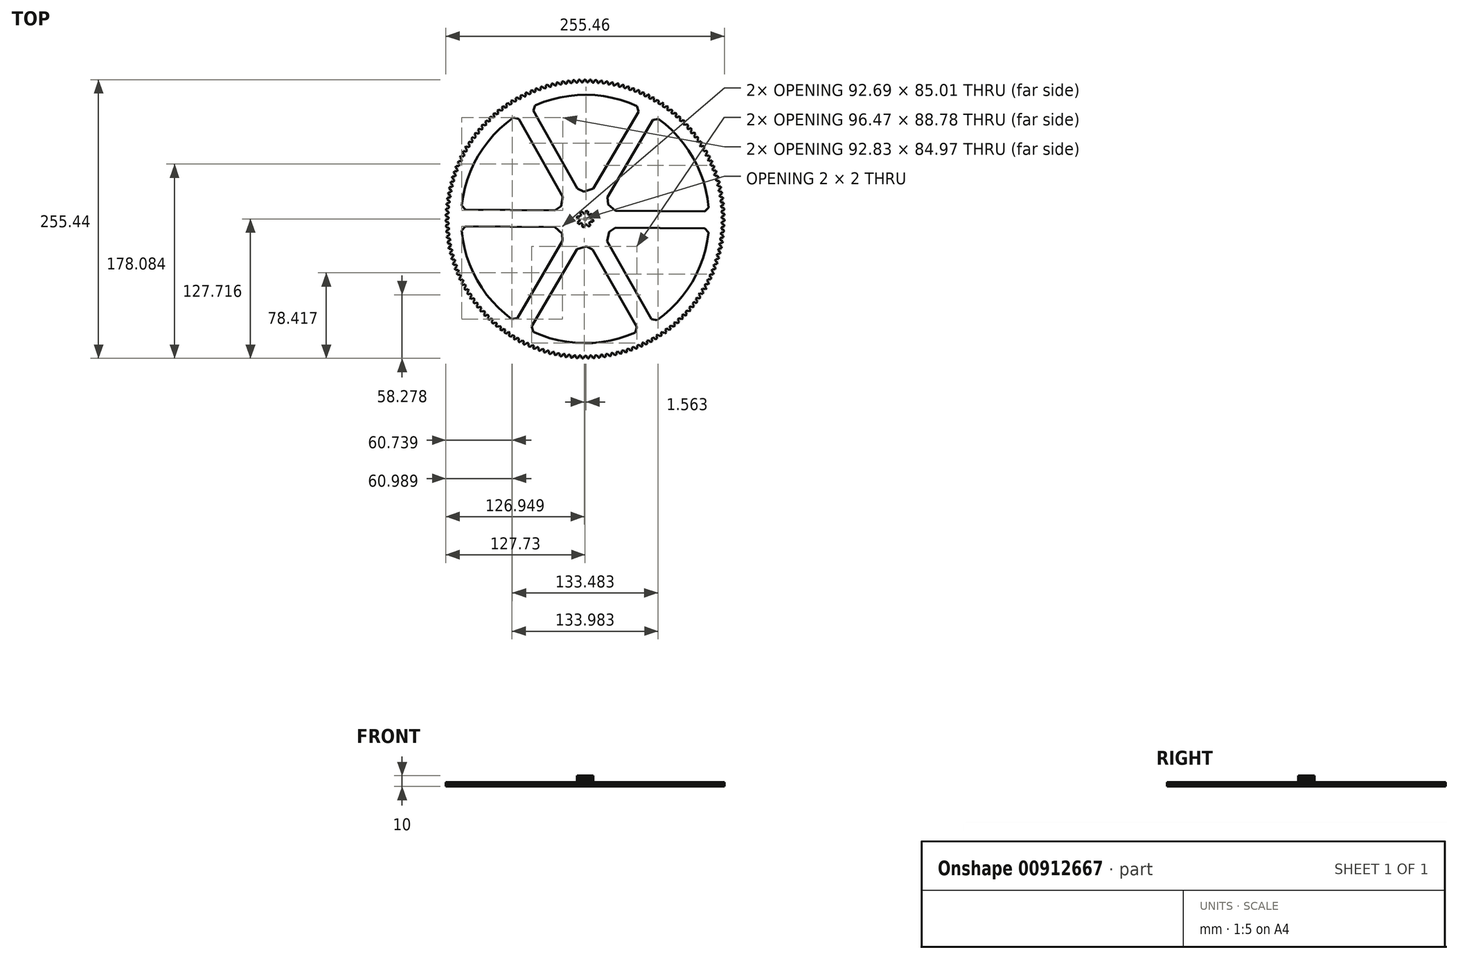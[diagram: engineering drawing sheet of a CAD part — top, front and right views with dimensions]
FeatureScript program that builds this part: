
annotation { "Feature Type Name" : "Feature", "Feature Type Description" : "" }
export const myFeature = defineFeature(function(context is Context, id is Id, definition is map)
    precondition{}
    {
        {
            var Q0;
            Q0=qCreatedBy(makeId("Top.planeOp"),FACE);
            var sketch = newSketch(context, id + "F0", { "sketchPlane" : qUnion([Q0])});
            skLineSegment(sketch, "E0", {"start": v(117.3, 0.66) * mm, "end": v(117.9, 0.46) * mm});
            skLineSegment(sketch, "E1", {"start": v(117.9, 0.46) * mm, "end": v(119.1, 0.02) * mm});
            skLineSegment(sketch, "E2", {"start": v(119.1, 0.02) * mm, "end": v(119.7, -0.2) * mm});
            skLineSegment(sketch, "E3", {"start": v(119.7, -0.2) * mm, "end": v(119.68, -1.82) * mm});
            skLineSegment(sketch, "E4", {"start": v(119.68, -1.82) * mm, "end": v(119.08, -2.04) * mm});
            skLineSegment(sketch, "E5", {"start": v(119.08, -2.04) * mm, "end": v(117.87, -2.46) * mm});
            skLineSegment(sketch, "E6", {"start": v(117.87, -2.46) * mm, "end": v(117.27, -2.65) * mm});
            skLineSegment(sketch, "E7", {"start": v(117.27, -2.65) * mm, "end": v(117.23, -4.3) * mm});
            skLineSegment(sketch, "E8", {"start": v(117.23, -4.3) * mm, "end": v(117.82, -4.52) * mm});
            skLineSegment(sketch, "E9", {"start": v(117.82, -4.52) * mm, "end": v(119, -5) * mm});
            skLineSegment(sketch, "E10", {"start": v(119, -5) * mm, "end": v(119.59, -5.25) * mm});
            skLineSegment(sketch, "E11", {"start": v(119.59, -5.25) * mm, "end": v(119.51, -6.86) * mm});
            skLineSegment(sketch, "E12", {"start": v(119.51, -6.86) * mm, "end": v(118.9, -7.06) * mm});
            skLineSegment(sketch, "E13", {"start": v(118.9, -7.06) * mm, "end": v(117.68, -7.43) * mm});
            skLineSegment(sketch, "E14", {"start": v(117.68, -7.43) * mm, "end": v(117.07, -7.6) * mm});
            skLineSegment(sketch, "E15", {"start": v(117.07, -7.6) * mm, "end": v(116.96, -9.24) * mm});
            skLineSegment(sketch, "E16", {"start": v(116.96, -9.24) * mm, "end": v(117.54, -9.49) * mm});
            skLineSegment(sketch, "E17", {"start": v(117.54, -9.49) * mm, "end": v(118.7, -10.01) * mm});
            skLineSegment(sketch, "E18", {"start": v(118.7, -10.01) * mm, "end": v(119.28, -10.3) * mm});
            skLineSegment(sketch, "E19", {"start": v(119.28, -10.3) * mm, "end": v(119.14, -11.9) * mm});
            skLineSegment(sketch, "E20", {"start": v(119.14, -11.9) * mm, "end": v(118.52, -12.07) * mm});
            skLineSegment(sketch, "E21", {"start": v(118.52, -12.07) * mm, "end": v(117.29, -12.39) * mm});
            skLineSegment(sketch, "E22", {"start": v(117.29, -12.39) * mm, "end": v(116.67, -12.53) * mm});
            skLineSegment(sketch, "E23", {"start": v(116.67, -12.53) * mm, "end": v(116.5, -14.17) * mm});
            skLineSegment(sketch, "E24", {"start": v(116.5, -14.17) * mm, "end": v(117.07, -14.44) * mm});
            skLineSegment(sketch, "E25", {"start": v(117.07, -14.44) * mm, "end": v(118.2, -15.01) * mm});
            skLineSegment(sketch, "E26", {"start": v(118.2, -15.01) * mm, "end": v(118.78, -15.31) * mm});
            skLineSegment(sketch, "E27", {"start": v(118.78, -15.31) * mm, "end": v(118.57, -16.91) * mm});
            skLineSegment(sketch, "E28", {"start": v(118.57, -16.91) * mm, "end": v(117.95, -17.06) * mm});
            skLineSegment(sketch, "E29", {"start": v(117.95, -17.06) * mm, "end": v(116.7, -17.33) * mm});
            skLineSegment(sketch, "E30", {"start": v(116.7, -17.33) * mm, "end": v(116.08, -17.45) * mm});
            skLineSegment(sketch, "E31", {"start": v(116.08, -17.45) * mm, "end": v(115.84, -19.08) * mm});
            skLineSegment(sketch, "E32", {"start": v(115.84, -19.08) * mm, "end": v(116.4, -19.37) * mm});
            skLineSegment(sketch, "E33", {"start": v(116.4, -19.37) * mm, "end": v(117.52, -19.99) * mm});
            skLineSegment(sketch, "E34", {"start": v(117.52, -19.99) * mm, "end": v(118.07, -20.31) * mm});
            skLineSegment(sketch, "E35", {"start": v(118.07, -20.31) * mm, "end": v(117.8, -21.9) * mm});
            skLineSegment(sketch, "E36", {"start": v(117.8, -21.9) * mm, "end": v(117.18, -22.02) * mm});
            skLineSegment(sketch, "E37", {"start": v(117.18, -22.02) * mm, "end": v(115.92, -22.24) * mm});
            skLineSegment(sketch, "E38", {"start": v(115.92, -22.24) * mm, "end": v(115.3, -22.34) * mm});
            skLineSegment(sketch, "E39", {"start": v(115.3, -22.34) * mm, "end": v(114.99, -23.95) * mm});
            skLineSegment(sketch, "E40", {"start": v(114.99, -23.95) * mm, "end": v(115.54, -24.27) * mm});
            skLineSegment(sketch, "E41", {"start": v(115.54, -24.27) * mm, "end": v(116.63, -24.93) * mm});
            skLineSegment(sketch, "E42", {"start": v(116.63, -24.93) * mm, "end": v(117.17, -25.28) * mm});
            skLineSegment(sketch, "E43", {"start": v(117.17, -25.28) * mm, "end": v(116.84, -26.85) * mm});
            skLineSegment(sketch, "E44", {"start": v(116.84, -26.85) * mm, "end": v(116.2, -26.95) * mm});
            skLineSegment(sketch, "E45", {"start": v(116.2, -26.95) * mm, "end": v(114.94, -27.12) * mm});
            skLineSegment(sketch, "E46", {"start": v(114.94, -27.12) * mm, "end": v(114.31, -27.2) * mm});
            skLineSegment(sketch, "E47", {"start": v(114.31, -27.2) * mm, "end": v(113.95, -28.8) * mm});
            skLineSegment(sketch, "E48", {"start": v(113.95, -28.8) * mm, "end": v(114.48, -29.13) * mm});
            skLineSegment(sketch, "E49", {"start": v(114.48, -29.13) * mm, "end": v(115.55, -29.84) * mm});
            skLineSegment(sketch, "E50", {"start": v(115.55, -29.84) * mm, "end": v(116.08, -30.2) * mm});
            skLineSegment(sketch, "E51", {"start": v(116.08, -30.2) * mm, "end": v(115.69, -31.77) * mm});
            skLineSegment(sketch, "E52", {"start": v(115.69, -31.77) * mm, "end": v(115.05, -31.84) * mm});
            skLineSegment(sketch, "E53", {"start": v(115.05, -31.84) * mm, "end": v(113.78, -31.96) * mm});
            skLineSegment(sketch, "E54", {"start": v(113.78, -31.96) * mm, "end": v(113.14, -32) * mm});
            skLineSegment(sketch, "E55", {"start": v(113.14, -32) * mm, "end": v(112.71, -33.6) * mm});
            skLineSegment(sketch, "E56", {"start": v(112.71, -33.6) * mm, "end": v(113.24, -33.95) * mm});
            skLineSegment(sketch, "E57", {"start": v(113.24, -33.95) * mm, "end": v(114.27, -34.7) * mm});
            skLineSegment(sketch, "E58", {"start": v(114.27, -34.7) * mm, "end": v(114.79, -35.08) * mm});
            skLineSegment(sketch, "E59", {"start": v(114.79, -35.08) * mm, "end": v(114.33, -36.63) * mm});
            skLineSegment(sketch, "E60", {"start": v(114.33, -36.63) * mm, "end": v(113.7, -36.68) * mm});
            skLineSegment(sketch, "E61", {"start": v(113.7, -36.68) * mm, "end": v(112.42, -36.75) * mm});
            skLineSegment(sketch, "E62", {"start": v(112.42, -36.75) * mm, "end": v(111.79, -36.77) * mm});
            skLineSegment(sketch, "E63", {"start": v(111.79, -36.77) * mm, "end": v(111.3, -38.34) * mm});
            skLineSegment(sketch, "E64", {"start": v(111.3, -38.34) * mm, "end": v(111.8, -38.71) * mm});
            skLineSegment(sketch, "E65", {"start": v(111.8, -38.71) * mm, "end": v(112.8, -39.5) * mm});
            skLineSegment(sketch, "E66", {"start": v(112.8, -39.5) * mm, "end": v(113.3, -39.9) * mm});
            skLineSegment(sketch, "E67", {"start": v(113.3, -39.9) * mm, "end": v(112.8, -41.43) * mm});
            skLineSegment(sketch, "E68", {"start": v(112.8, -41.43) * mm, "end": v(112.15, -41.46) * mm});
            skLineSegment(sketch, "E69", {"start": v(112.15, -41.46) * mm, "end": v(110.87, -41.48) * mm});
            skLineSegment(sketch, "E70", {"start": v(110.87, -41.48) * mm, "end": v(110.24, -41.47) * mm});
            skLineSegment(sketch, "E71", {"start": v(110.24, -41.47) * mm, "end": v(109.69, -43.02) * mm});
            skLineSegment(sketch, "E72", {"start": v(109.69, -43.02) * mm, "end": v(110.18, -43.42) * mm});
            skLineSegment(sketch, "E73", {"start": v(110.18, -43.42) * mm, "end": v(111.15, -44.24) * mm});
            skLineSegment(sketch, "E74", {"start": v(111.15, -44.24) * mm, "end": v(111.63, -44.67) * mm});
            skLineSegment(sketch, "E75", {"start": v(111.63, -44.67) * mm, "end": v(111.06, -46.18) * mm});
            skLineSegment(sketch, "E76", {"start": v(111.06, -46.18) * mm, "end": v(110.42, -46.17) * mm});
            skLineSegment(sketch, "E77", {"start": v(110.42, -46.17) * mm, "end": v(109.14, -46.14) * mm});
            skLineSegment(sketch, "E78", {"start": v(109.14, -46.14) * mm, "end": v(108.5, -46.11) * mm});
            skLineSegment(sketch, "E79", {"start": v(108.5, -46.11) * mm, "end": v(107.9, -47.64) * mm});
            skLineSegment(sketch, "E80", {"start": v(107.9, -47.64) * mm, "end": v(108.37, -48.05) * mm});
            skLineSegment(sketch, "E81", {"start": v(108.37, -48.05) * mm, "end": v(109.31, -48.92) * mm});
            skLineSegment(sketch, "E82", {"start": v(109.31, -48.92) * mm, "end": v(109.78, -49.36) * mm});
            skLineSegment(sketch, "E83", {"start": v(109.78, -49.36) * mm, "end": v(109.14, -50.84) * mm});
            skLineSegment(sketch, "E84", {"start": v(109.14, -50.84) * mm, "end": v(108.5, -50.82) * mm});
            skLineSegment(sketch, "E85", {"start": v(108.5, -50.82) * mm, "end": v(107.23, -50.74) * mm});
            skLineSegment(sketch, "E86", {"start": v(107.23, -50.74) * mm, "end": v(106.6, -50.68) * mm});
            skLineSegment(sketch, "E87", {"start": v(106.6, -50.68) * mm, "end": v(105.92, -52.18) * mm});
            skLineSegment(sketch, "E88", {"start": v(105.92, -52.18) * mm, "end": v(106.38, -52.62) * mm});
            skLineSegment(sketch, "E89", {"start": v(106.38, -52.62) * mm, "end": v(107.29, -53.52) * mm});
            skLineSegment(sketch, "E90", {"start": v(107.29, -53.52) * mm, "end": v(107.73, -53.98) * mm});
            skLineSegment(sketch, "E91", {"start": v(107.73, -53.98) * mm, "end": v(107.04, -55.43) * mm});
            skLineSegment(sketch, "E92", {"start": v(107.04, -55.43) * mm, "end": v(106.4, -55.38) * mm});
            skLineSegment(sketch, "E93", {"start": v(106.4, -55.38) * mm, "end": v(105.13, -55.25) * mm});
            skLineSegment(sketch, "E94", {"start": v(105.13, -55.25) * mm, "end": v(104.5, -55.17) * mm});
            skLineSegment(sketch, "E95", {"start": v(104.5, -55.17) * mm, "end": v(103.77, -56.64) * mm});
            skLineSegment(sketch, "E96", {"start": v(103.77, -56.64) * mm, "end": v(104.21, -57.1) * mm});
            skLineSegment(sketch, "E97", {"start": v(104.21, -57.1) * mm, "end": v(105.08, -58.03) * mm});
            skLineSegment(sketch, "E98", {"start": v(105.08, -58.03) * mm, "end": v(105.51, -58.5) * mm});
            skLineSegment(sketch, "E99", {"start": v(105.51, -58.5) * mm, "end": v(104.76, -59.94) * mm});
            skLineSegment(sketch, "E100", {"start": v(104.76, -59.94) * mm, "end": v(104.13, -59.86) * mm});
            skLineSegment(sketch, "E101", {"start": v(104.13, -59.86) * mm, "end": v(102.86, -59.68) * mm});
            skLineSegment(sketch, "E102", {"start": v(102.86, -59.68) * mm, "end": v(102.24, -59.57) * mm});
            skLineSegment(sketch, "E103", {"start": v(102.24, -59.57) * mm, "end": v(101.45, -61.01) * mm});
            skLineSegment(sketch, "E104", {"start": v(101.45, -61.01) * mm, "end": v(101.87, -61.48) * mm});
            skLineSegment(sketch, "E105", {"start": v(101.87, -61.48) * mm, "end": v(102.7, -62.45) * mm});
            skLineSegment(sketch, "E106", {"start": v(102.7, -62.45) * mm, "end": v(103.11, -62.95) * mm});
            skLineSegment(sketch, "E107", {"start": v(103.11, -62.95) * mm, "end": v(102.3, -64.35) * mm});
            skLineSegment(sketch, "E108", {"start": v(102.3, -64.35) * mm, "end": v(101.67, -64.24) * mm});
            skLineSegment(sketch, "E109", {"start": v(101.67, -64.24) * mm, "end": v(100.42, -64.01) * mm});
            skLineSegment(sketch, "E110", {"start": v(100.42, -64.01) * mm, "end": v(99.8, -63.88) * mm});
            skLineSegment(sketch, "E111", {"start": v(99.8, -63.88) * mm, "end": v(98.95, -65.3) * mm});
            skLineSegment(sketch, "E112", {"start": v(98.95, -65.3) * mm, "end": v(99.36, -65.78) * mm});
            skLineSegment(sketch, "E113", {"start": v(99.36, -65.78) * mm, "end": v(100.15, -66.78) * mm});
            skLineSegment(sketch, "E114", {"start": v(100.15, -66.78) * mm, "end": v(100.54, -67.3) * mm});
            skLineSegment(sketch, "E115", {"start": v(100.54, -67.3) * mm, "end": v(99.68, -68.66) * mm});
            skLineSegment(sketch, "E116", {"start": v(99.68, -68.66) * mm, "end": v(99.05, -68.53) * mm});
            skLineSegment(sketch, "E117", {"start": v(99.05, -68.53) * mm, "end": v(97.8, -68.25) * mm});
            skLineSegment(sketch, "E118", {"start": v(97.8, -68.25) * mm, "end": v(97.19, -68.1) * mm});
            skLineSegment(sketch, "E119", {"start": v(97.19, -68.1) * mm, "end": v(96.29, -69.47) * mm});
            skLineSegment(sketch, "E120", {"start": v(96.29, -69.47) * mm, "end": v(96.67, -69.97) * mm});
            skLineSegment(sketch, "E121", {"start": v(96.67, -69.97) * mm, "end": v(97.43, -71) * mm});
            skLineSegment(sketch, "E122", {"start": v(97.43, -71) * mm, "end": v(97.8, -71.53) * mm});
            skLineSegment(sketch, "E123", {"start": v(97.8, -71.53) * mm, "end": v(96.88, -72.86) * mm});
            skLineSegment(sketch, "E124", {"start": v(96.88, -72.86) * mm, "end": v(96.26, -72.7) * mm});
            skLineSegment(sketch, "E125", {"start": v(96.26, -72.7) * mm, "end": v(95.03, -72.37) * mm});
            skLineSegment(sketch, "E126", {"start": v(95.03, -72.37) * mm, "end": v(94.42, -72.2) * mm});
            skLineSegment(sketch, "E127", {"start": v(94.42, -72.2) * mm, "end": v(93.46, -73.53) * mm});
            skLineSegment(sketch, "E128", {"start": v(93.46, -73.53) * mm, "end": v(93.83, -74.05) * mm});
            skLineSegment(sketch, "E129", {"start": v(93.83, -74.05) * mm, "end": v(94.54, -75.11) * mm});
            skLineSegment(sketch, "E130", {"start": v(94.54, -75.11) * mm, "end": v(94.89, -75.65) * mm});
            skLineSegment(sketch, "E131", {"start": v(94.89, -75.65) * mm, "end": v(93.92, -76.94) * mm});
            skLineSegment(sketch, "E132", {"start": v(93.92, -76.94) * mm, "end": v(93.3, -76.77) * mm});
            skLineSegment(sketch, "E133", {"start": v(93.3, -76.77) * mm, "end": v(92.09, -76.39) * mm});
            skLineSegment(sketch, "E134", {"start": v(92.09, -76.39) * mm, "end": v(91.49, -76.19) * mm});
            skLineSegment(sketch, "E135", {"start": v(91.49, -76.19) * mm, "end": v(90.48, -77.49) * mm});
            skLineSegment(sketch, "E136", {"start": v(90.48, -77.49) * mm, "end": v(90.82, -78.02) * mm});
            skLineSegment(sketch, "E137", {"start": v(90.82, -78.02) * mm, "end": v(91.5, -79.1) * mm});
            skLineSegment(sketch, "E138", {"start": v(91.5, -79.1) * mm, "end": v(91.82, -79.66) * mm});
            skLineSegment(sketch, "E139", {"start": v(91.82, -79.66) * mm, "end": v(90.8, -80.91) * mm});
            skLineSegment(sketch, "E140", {"start": v(90.8, -80.91) * mm, "end": v(90.2, -80.71) * mm});
            skLineSegment(sketch, "E141", {"start": v(90.2, -80.71) * mm, "end": v(89, -80.28) * mm});
            skLineSegment(sketch, "E142", {"start": v(89, -80.28) * mm, "end": v(88.4, -80.06) * mm});
            skLineSegment(sketch, "E143", {"start": v(88.4, -80.06) * mm, "end": v(87.34, -81.32) * mm});
            skLineSegment(sketch, "E144", {"start": v(87.34, -81.32) * mm, "end": v(87.66, -81.86) * mm});
            skLineSegment(sketch, "E145", {"start": v(87.66, -81.86) * mm, "end": v(88.29, -82.97) * mm});
            skLineSegment(sketch, "E146", {"start": v(88.29, -82.97) * mm, "end": v(88.6, -83.54) * mm});
            skLineSegment(sketch, "E147", {"start": v(88.6, -83.54) * mm, "end": v(87.53, -84.75) * mm});
            skLineSegment(sketch, "E148", {"start": v(87.53, -84.75) * mm, "end": v(86.93, -84.53) * mm});
            skLineSegment(sketch, "E149", {"start": v(86.93, -84.53) * mm, "end": v(85.74, -84.05) * mm});
            skLineSegment(sketch, "E150", {"start": v(85.74, -84.05) * mm, "end": v(85.16, -83.8) * mm});
            skLineSegment(sketch, "E151", {"start": v(85.16, -83.8) * mm, "end": v(84.05, -85.02) * mm});
            skLineSegment(sketch, "E152", {"start": v(84.05, -85.02) * mm, "end": v(84.35, -85.58) * mm});
            skLineSegment(sketch, "E153", {"start": v(84.35, -85.58) * mm, "end": v(84.94, -86.71) * mm});
            skLineSegment(sketch, "E154", {"start": v(84.94, -86.71) * mm, "end": v(85.22, -87.3) * mm});
            skLineSegment(sketch, "E155", {"start": v(85.22, -87.3) * mm, "end": v(84.1, -88.46) * mm});
            skLineSegment(sketch, "E156", {"start": v(84.1, -88.46) * mm, "end": v(83.52, -88.21) * mm});
            skLineSegment(sketch, "E157", {"start": v(83.52, -88.21) * mm, "end": v(82.35, -87.7) * mm});
            skLineSegment(sketch, "E158", {"start": v(82.35, -87.7) * mm, "end": v(81.78, -87.42) * mm});
            skLineSegment(sketch, "E159", {"start": v(81.78, -87.42) * mm, "end": v(80.62, -88.6) * mm});
            skLineSegment(sketch, "E160", {"start": v(80.62, -88.6) * mm, "end": v(80.9, -89.16) * mm});
            skLineSegment(sketch, "E161", {"start": v(80.9, -89.16) * mm, "end": v(81.44, -90.32) * mm});
            skLineSegment(sketch, "E162", {"start": v(81.44, -90.32) * mm, "end": v(81.7, -90.9) * mm});
            skLineSegment(sketch, "E163", {"start": v(81.7, -90.9) * mm, "end": v(80.54, -92.03) * mm});
            skLineSegment(sketch, "E164", {"start": v(80.54, -92.03) * mm, "end": v(79.96, -91.76) * mm});
            skLineSegment(sketch, "E165", {"start": v(79.96, -91.76) * mm, "end": v(78.81, -91.2) * mm});
            skLineSegment(sketch, "E166", {"start": v(78.81, -91.2) * mm, "end": v(78.25, -90.9) * mm});
            skLineSegment(sketch, "E167", {"start": v(78.25, -90.9) * mm, "end": v(77.05, -92.03) * mm});
            skLineSegment(sketch, "E168", {"start": v(77.05, -92.03) * mm, "end": v(77.31, -92.6) * mm});
            skLineSegment(sketch, "E169", {"start": v(77.31, -92.6) * mm, "end": v(77.8, -93.78) * mm});
            skLineSegment(sketch, "E170", {"start": v(77.8, -93.78) * mm, "end": v(78.03, -94.38) * mm});
            skLineSegment(sketch, "E171", {"start": v(78.03, -94.38) * mm, "end": v(76.84, -95.46) * mm});
            skLineSegment(sketch, "E172", {"start": v(76.84, -95.46) * mm, "end": v(76.27, -95.17) * mm});
            skLineSegment(sketch, "E173", {"start": v(76.27, -95.17) * mm, "end": v(75.14, -94.56) * mm});
            skLineSegment(sketch, "E174", {"start": v(75.14, -94.56) * mm, "end": v(74.6, -94.24) * mm});
            skLineSegment(sketch, "E175", {"start": v(74.6, -94.24) * mm, "end": v(73.35, -95.32) * mm});
            skLineSegment(sketch, "E176", {"start": v(73.35, -95.32) * mm, "end": v(73.59, -95.9) * mm});
            skLineSegment(sketch, "E177", {"start": v(73.59, -95.9) * mm, "end": v(74.03, -97.1) * mm});
            skLineSegment(sketch, "E178", {"start": v(74.03, -97.1) * mm, "end": v(74.24, -97.7) * mm});
            skLineSegment(sketch, "E179", {"start": v(74.24, -97.7) * mm, "end": v(73, -98.74) * mm});
            skLineSegment(sketch, "E180", {"start": v(73, -98.74) * mm, "end": v(72.44, -98.42) * mm});
            skLineSegment(sketch, "E181", {"start": v(72.44, -98.42) * mm, "end": v(71.34, -97.77) * mm});
            skLineSegment(sketch, "E182", {"start": v(71.34, -97.77) * mm, "end": v(70.8, -97.43) * mm});
            skLineSegment(sketch, "E183", {"start": v(70.8, -97.43) * mm, "end": v(69.52, -98.46) * mm});
            skLineSegment(sketch, "E184", {"start": v(69.52, -98.46) * mm, "end": v(69.73, -99.05) * mm});
            skLineSegment(sketch, "E185", {"start": v(69.73, -99.05) * mm, "end": v(70.13, -100.27) * mm});
            skLineSegment(sketch, "E186", {"start": v(70.13, -100.27) * mm, "end": v(70.31, -100.88) * mm});
            skLineSegment(sketch, "E187", {"start": v(70.31, -100.88) * mm, "end": v(69.03, -101.86) * mm});
            skLineSegment(sketch, "E188", {"start": v(69.03, -101.86) * mm, "end": v(68.49, -101.52) * mm});
            skLineSegment(sketch, "E189", {"start": v(68.49, -101.52) * mm, "end": v(67.42, -100.83) * mm});
            skLineSegment(sketch, "E190", {"start": v(67.42, -100.83) * mm, "end": v(66.9, -100.47) * mm});
            skLineSegment(sketch, "E191", {"start": v(66.9, -100.47) * mm, "end": v(65.57, -101.44) * mm});
            skLineSegment(sketch, "E192", {"start": v(65.57, -101.44) * mm, "end": v(65.76, -102.05) * mm});
            skLineSegment(sketch, "E193", {"start": v(65.76, -102.05) * mm, "end": v(66.1, -103.28) * mm});
            skLineSegment(sketch, "E194", {"start": v(66.1, -103.28) * mm, "end": v(66.27, -103.9) * mm});
            skLineSegment(sketch, "E195", {"start": v(66.27, -103.9) * mm, "end": v(64.95, -104.83) * mm});
            skLineSegment(sketch, "E196", {"start": v(64.95, -104.83) * mm, "end": v(64.42, -104.47) * mm});
            skLineSegment(sketch, "E197", {"start": v(64.42, -104.47) * mm, "end": v(63.38, -103.73) * mm});
            skLineSegment(sketch, "E198", {"start": v(63.38, -103.73) * mm, "end": v(62.87, -103.35) * mm});
            skLineSegment(sketch, "E199", {"start": v(62.87, -103.35) * mm, "end": v(61.5, -104.27) * mm});
            skLineSegment(sketch, "E200", {"start": v(61.5, -104.27) * mm, "end": v(61.67, -104.88) * mm});
            skLineSegment(sketch, "E201", {"start": v(61.67, -104.88) * mm, "end": v(61.97, -106.13) * mm});
            skLineSegment(sketch, "E202", {"start": v(61.97, -106.13) * mm, "end": v(62.1, -106.75) * mm});
            skLineSegment(sketch, "E203", {"start": v(62.1, -106.75) * mm, "end": v(60.75, -107.63) * mm});
            skLineSegment(sketch, "E204", {"start": v(60.75, -107.63) * mm, "end": v(60.23, -107.25) * mm});
            skLineSegment(sketch, "E205", {"start": v(60.23, -107.25) * mm, "end": v(59.22, -106.47) * mm});
            skLineSegment(sketch, "E206", {"start": v(59.22, -106.47) * mm, "end": v(58.73, -106.07) * mm});
            skLineSegment(sketch, "E207", {"start": v(58.73, -106.07) * mm, "end": v(57.33, -106.94) * mm});
            skLineSegment(sketch, "E208", {"start": v(57.33, -106.94) * mm, "end": v(57.47, -107.56) * mm});
            skLineSegment(sketch, "E209", {"start": v(57.47, -107.56) * mm, "end": v(57.72, -108.8) * mm});
            skLineSegment(sketch, "E210", {"start": v(57.72, -108.8) * mm, "end": v(57.83, -109.44) * mm});
            skLineSegment(sketch, "E211", {"start": v(57.83, -109.44) * mm, "end": v(56.45, -110.26) * mm});
            skLineSegment(sketch, "E212", {"start": v(56.45, -110.26) * mm, "end": v(55.94, -109.86) * mm});
            skLineSegment(sketch, "E213", {"start": v(55.94, -109.86) * mm, "end": v(54.97, -109.04) * mm});
            skLineSegment(sketch, "E214", {"start": v(54.97, -109.04) * mm, "end": v(54.49, -108.63) * mm});
            skLineSegment(sketch, "E215", {"start": v(54.49, -108.63) * mm, "end": v(53.06, -109.44) * mm});
            skLineSegment(sketch, "E216", {"start": v(53.06, -109.44) * mm, "end": v(53.17, -110.06) * mm});
            skLineSegment(sketch, "E217", {"start": v(53.17, -110.06) * mm, "end": v(53.37, -111.32) * mm});
            skLineSegment(sketch, "E218", {"start": v(53.37, -111.32) * mm, "end": v(53.46, -111.96) * mm});
            skLineSegment(sketch, "E219", {"start": v(53.46, -111.96) * mm, "end": v(52.04, -112.72) * mm});
            skLineSegment(sketch, "E220", {"start": v(52.04, -112.72) * mm, "end": v(51.55, -112.3) * mm});
            skLineSegment(sketch, "E221", {"start": v(51.55, -112.3) * mm, "end": v(50.6, -111.45) * mm});
            skLineSegment(sketch, "E222", {"start": v(50.6, -111.45) * mm, "end": v(50.15, -111.01) * mm});
            skLineSegment(sketch, "E223", {"start": v(50.15, -111.01) * mm, "end": v(48.69, -111.76) * mm});
            skLineSegment(sketch, "E224", {"start": v(48.69, -111.76) * mm, "end": v(48.78, -112.4) * mm});
            skLineSegment(sketch, "E225", {"start": v(48.78, -112.4) * mm, "end": v(48.93, -113.66) * mm});
            skLineSegment(sketch, "E226", {"start": v(48.93, -113.66) * mm, "end": v(48.99, -114.3) * mm});
            skLineSegment(sketch, "E227", {"start": v(48.99, -114.3) * mm, "end": v(47.54, -115) * mm});
            skLineSegment(sketch, "E228", {"start": v(47.54, -115) * mm, "end": v(47.07, -114.57) * mm});
            skLineSegment(sketch, "E229", {"start": v(47.07, -114.57) * mm, "end": v(46.16, -113.68) * mm});
            skLineSegment(sketch, "E230", {"start": v(46.16, -113.68) * mm, "end": v(45.72, -113.22) * mm});
            skLineSegment(sketch, "E231", {"start": v(45.72, -113.22) * mm, "end": v(44.23, -113.92) * mm});
            skLineSegment(sketch, "E232", {"start": v(44.23, -113.92) * mm, "end": v(44.3, -114.55) * mm});
            skLineSegment(sketch, "E233", {"start": v(44.3, -114.55) * mm, "end": v(44.4, -115.82) * mm});
            skLineSegment(sketch, "E234", {"start": v(44.4, -115.82) * mm, "end": v(44.43, -116.46) * mm});
            skLineSegment(sketch, "E235", {"start": v(44.43, -116.46) * mm, "end": v(42.95, -117.12) * mm});
            skLineSegment(sketch, "E236", {"start": v(42.95, -117.12) * mm, "end": v(42.5, -116.66) * mm});
            skLineSegment(sketch, "E237", {"start": v(42.5, -116.66) * mm, "end": v(41.63, -115.73) * mm});
            skLineSegment(sketch, "E238", {"start": v(41.63, -115.73) * mm, "end": v(41.2, -115.26) * mm});
            skLineSegment(sketch, "E239", {"start": v(41.2, -115.26) * mm, "end": v(39.69, -115.9) * mm});
            skLineSegment(sketch, "E240", {"start": v(39.69, -115.9) * mm, "end": v(39.73, -116.53) * mm});
            skLineSegment(sketch, "E241", {"start": v(39.73, -116.53) * mm, "end": v(39.77, -117.8) * mm});
            skLineSegment(sketch, "E242", {"start": v(39.77, -117.8) * mm, "end": v(39.79, -118.44) * mm});
            skLineSegment(sketch, "E243", {"start": v(39.79, -118.44) * mm, "end": v(38.29, -119.04) * mm});
            skLineSegment(sketch, "E244", {"start": v(38.29, -119.04) * mm, "end": v(37.85, -118.56) * mm});
            skLineSegment(sketch, "E245", {"start": v(37.85, -118.56) * mm, "end": v(37.02, -117.6) * mm});
            skLineSegment(sketch, "E246", {"start": v(37.02, -117.6) * mm, "end": v(36.61, -117.11) * mm});
            skLineSegment(sketch, "E247", {"start": v(36.61, -117.11) * mm, "end": v(35.07, -117.69) * mm});
            skLineSegment(sketch, "E248", {"start": v(35.07, -117.69) * mm, "end": v(35.08, -118.32) * mm});
            skLineSegment(sketch, "E249", {"start": v(35.08, -118.32) * mm, "end": v(35.08, -119.6) * mm});
            skLineSegment(sketch, "E250", {"start": v(35.08, -119.6) * mm, "end": v(35.07, -120.24) * mm});
            skLineSegment(sketch, "E251", {"start": v(35.07, -120.24) * mm, "end": v(33.55, -120.77) * mm});
            skLineSegment(sketch, "E252", {"start": v(33.55, -120.77) * mm, "end": v(33.13, -120.28) * mm});
            skLineSegment(sketch, "E253", {"start": v(33.13, -120.28) * mm, "end": v(32.33, -119.29) * mm});
            skLineSegment(sketch, "E254", {"start": v(32.33, -119.29) * mm, "end": v(31.95, -118.78) * mm});
            skLineSegment(sketch, "E255", {"start": v(31.95, -118.78) * mm, "end": v(30.39, -119.3) * mm});
            skLineSegment(sketch, "E256", {"start": v(30.39, -119.3) * mm, "end": v(30.38, -119.93) * mm});
            skLineSegment(sketch, "E257", {"start": v(30.38, -119.93) * mm, "end": v(30.32, -121.2) * mm});
            skLineSegment(sketch, "E258", {"start": v(30.32, -121.2) * mm, "end": v(30.28, -121.85) * mm});
            skLineSegment(sketch, "E259", {"start": v(30.28, -121.85) * mm, "end": v(28.74, -122.32) * mm});
            skLineSegment(sketch, "E260", {"start": v(28.74, -122.32) * mm, "end": v(28.35, -121.81) * mm});
            skLineSegment(sketch, "E261", {"start": v(28.35, -121.81) * mm, "end": v(27.6, -120.79) * mm});
            skLineSegment(sketch, "E262", {"start": v(27.6, -120.79) * mm, "end": v(27.23, -120.27) * mm});
            skLineSegment(sketch, "E263", {"start": v(27.23, -120.27) * mm, "end": v(25.65, -120.72) * mm});
            skLineSegment(sketch, "E264", {"start": v(25.65, -120.72) * mm, "end": v(25.6, -121.36) * mm});
            skLineSegment(sketch, "E265", {"start": v(25.6, -121.36) * mm, "end": v(25.5, -122.63) * mm});
            skLineSegment(sketch, "E266", {"start": v(25.5, -122.63) * mm, "end": v(25.44, -123.27) * mm});
            skLineSegment(sketch, "E267", {"start": v(25.44, -123.27) * mm, "end": v(23.88, -123.68) * mm});
            skLineSegment(sketch, "E268", {"start": v(23.88, -123.68) * mm, "end": v(23.5, -123.16) * mm});
            skLineSegment(sketch, "E269", {"start": v(23.5, -123.16) * mm, "end": v(22.8, -122.1) * mm});
            skLineSegment(sketch, "E270", {"start": v(22.8, -122.1) * mm, "end": v(22.45, -121.57) * mm});
            skLineSegment(sketch, "E271", {"start": v(22.45, -121.57) * mm, "end": v(20.85, -121.96) * mm});
            skLineSegment(sketch, "E272", {"start": v(20.85, -121.96) * mm, "end": v(20.79, -122.6) * mm});
            skLineSegment(sketch, "E273", {"start": v(20.79, -122.6) * mm, "end": v(20.64, -123.86) * mm});
            skLineSegment(sketch, "E274", {"start": v(20.64, -123.86) * mm, "end": v(20.55, -124.5) * mm});
            skLineSegment(sketch, "E275", {"start": v(20.55, -124.5) * mm, "end": v(18.97, -124.84) * mm});
            skLineSegment(sketch, "E276", {"start": v(18.97, -124.84) * mm, "end": v(18.62, -124.3) * mm});
            skLineSegment(sketch, "E277", {"start": v(18.62, -124.3) * mm, "end": v(17.94, -123.22) * mm});
            skLineSegment(sketch, "E278", {"start": v(17.94, -123.22) * mm, "end": v(17.62, -122.68) * mm});
            skLineSegment(sketch, "E279", {"start": v(17.62, -122.68) * mm, "end": v(16, -123) * mm});
            skLineSegment(sketch, "E280", {"start": v(16, -123) * mm, "end": v(15.92, -123.63) * mm});
            skLineSegment(sketch, "E281", {"start": v(15.92, -123.63) * mm, "end": v(15.72, -124.9) * mm});
            skLineSegment(sketch, "E282", {"start": v(15.72, -124.9) * mm, "end": v(15.6, -125.53) * mm});
            skLineSegment(sketch, "E283", {"start": v(15.6, -125.53) * mm, "end": v(14.02, -125.81) * mm});
            skLineSegment(sketch, "E284", {"start": v(14.02, -125.81) * mm, "end": v(13.69, -125.26) * mm});
            skLineSegment(sketch, "E285", {"start": v(13.69, -125.26) * mm, "end": v(13.06, -124.15) * mm});
            skLineSegment(sketch, "E286", {"start": v(13.06, -124.15) * mm, "end": v(12.75, -123.6) * mm});
            skLineSegment(sketch, "E287", {"start": v(12.75, -123.6) * mm, "end": v(11.13, -123.86) * mm});
            skLineSegment(sketch, "E288", {"start": v(11.13, -123.86) * mm, "end": v(11.02, -124.48) * mm});
            skLineSegment(sketch, "E289", {"start": v(11.02, -124.48) * mm, "end": v(10.77, -125.73) * mm});
            skLineSegment(sketch, "E290", {"start": v(10.77, -125.73) * mm, "end": v(10.63, -126.36) * mm});
            skLineSegment(sketch, "E291", {"start": v(10.63, -126.36) * mm, "end": v(9.03, -126.59) * mm});
            skLineSegment(sketch, "E292", {"start": v(9.03, -126.59) * mm, "end": v(8.72, -126.02) * mm});
            skLineSegment(sketch, "E293", {"start": v(8.72, -126.02) * mm, "end": v(8.13, -124.9) * mm});
            skLineSegment(sketch, "E294", {"start": v(8.13, -124.9) * mm, "end": v(7.85, -124.32) * mm});
            skLineSegment(sketch, "E295", {"start": v(7.85, -124.32) * mm, "end": v(6.22, -124.52) * mm});
            skLineSegment(sketch, "E296", {"start": v(6.22, -124.52) * mm, "end": v(6.09, -125.14) * mm});
            skLineSegment(sketch, "E297", {"start": v(6.09, -125.14) * mm, "end": v(5.79, -126.38) * mm});
            skLineSegment(sketch, "E298", {"start": v(5.79, -126.38) * mm, "end": v(5.62, -127) * mm});
            skLineSegment(sketch, "E299", {"start": v(5.62, -127) * mm, "end": v(4.02, -127.16) * mm});
            skLineSegment(sketch, "E300", {"start": v(4.02, -127.16) * mm, "end": v(3.73, -126.59) * mm});
            skLineSegment(sketch, "E301", {"start": v(3.73, -126.59) * mm, "end": v(3.19, -125.43) * mm});
            skLineSegment(sketch, "E302", {"start": v(3.19, -125.43) * mm, "end": v(2.93, -124.85) * mm});
            skLineSegment(sketch, "E303", {"start": v(2.93, -124.85) * mm, "end": v(1.3, -124.99) * mm});
            skLineSegment(sketch, "E304", {"start": v(1.3, -124.99) * mm, "end": v(1.13, -125.6) * mm});
            skLineSegment(sketch, "E305", {"start": v(1.13, -125.6) * mm, "end": v(0.78, -126.83) * mm});
            skLineSegment(sketch, "E306", {"start": v(0.78, -126.83) * mm, "end": v(0.6, -127.44) * mm});
            skLineSegment(sketch, "E307", {"start": v(0.6, -127.44) * mm, "end": v(-1.02, -127.54) * mm});
            skLineSegment(sketch, "E308", {"start": v(-1.02, -127.54) * mm, "end": v(-1.28, -126.95) * mm});
            skLineSegment(sketch, "E309", {"start": v(-1.28, -126.95) * mm, "end": v(-1.78, -125.78) * mm});
            skLineSegment(sketch, "E310", {"start": v(-1.78, -125.78) * mm, "end": v(-2.01, -125.19) * mm});
            skLineSegment(sketch, "E311", {"start": v(-2.01, -125.19) * mm, "end": v(-3.65, -125.26) * mm});
            skLineSegment(sketch, "E312", {"start": v(-3.65, -125.26) * mm, "end": v(-3.84, -125.86) * mm});
            skLineSegment(sketch, "E313", {"start": v(-3.84, -125.86) * mm, "end": v(-4.23, -127.07) * mm});
            skLineSegment(sketch, "E314", {"start": v(-4.23, -127.07) * mm, "end": v(-4.45, -127.68) * mm});
            skLineSegment(sketch, "E315", {"start": v(-4.45, -127.68) * mm, "end": v(-6.06, -127.72) * mm});
            skLineSegment(sketch, "E316", {"start": v(-6.06, -127.72) * mm, "end": v(-6.3, -127.12) * mm});
            skLineSegment(sketch, "E317", {"start": v(-6.3, -127.12) * mm, "end": v(-6.75, -125.93) * mm});
            skLineSegment(sketch, "E318", {"start": v(-6.75, -125.93) * mm, "end": v(-6.96, -125.33) * mm});
            skLineSegment(sketch, "E319", {"start": v(-6.96, -125.33) * mm, "end": v(-8.6, -125.33) * mm});
            skLineSegment(sketch, "E320", {"start": v(-8.6, -125.33) * mm, "end": v(-8.81, -125.93) * mm});
            skLineSegment(sketch, "E321", {"start": v(-8.81, -125.93) * mm, "end": v(-9.26, -127.13) * mm});
            skLineSegment(sketch, "E322", {"start": v(-9.26, -127.13) * mm, "end": v(-9.5, -127.72) * mm});
            skLineSegment(sketch, "E323", {"start": v(-9.5, -127.72) * mm, "end": v(-11.1, -127.7) * mm});
            skLineSegment(sketch, "E324", {"start": v(-11.1, -127.7) * mm, "end": v(-11.32, -127.09) * mm});
            skLineSegment(sketch, "E325", {"start": v(-11.32, -127.09) * mm, "end": v(-11.73, -125.88) * mm});
            skLineSegment(sketch, "E326", {"start": v(-11.73, -125.88) * mm, "end": v(-11.91, -125.27) * mm});
            skLineSegment(sketch, "E327", {"start": v(-11.91, -125.27) * mm, "end": v(-13.55, -125.21) * mm});
            skLineSegment(sketch, "E328", {"start": v(-13.55, -125.21) * mm, "end": v(-13.79, -125.8) * mm});
            skLineSegment(sketch, "E329", {"start": v(-13.79, -125.8) * mm, "end": v(-14.28, -126.98) * mm});
            skLineSegment(sketch, "E330", {"start": v(-14.28, -126.98) * mm, "end": v(-14.54, -127.57) * mm});
            skLineSegment(sketch, "E331", {"start": v(-14.54, -127.57) * mm, "end": v(-16.15, -127.47) * mm});
            skLineSegment(sketch, "E332", {"start": v(-16.15, -127.47) * mm, "end": v(-16.34, -126.86) * mm});
            skLineSegment(sketch, "E333", {"start": v(-16.34, -126.86) * mm, "end": v(-16.7, -125.63) * mm});
            skLineSegment(sketch, "E334", {"start": v(-16.7, -125.63) * mm, "end": v(-16.86, -125.02) * mm});
            skLineSegment(sketch, "E335", {"start": v(-16.86, -125.02) * mm, "end": v(-18.5, -124.9) * mm});
            skLineSegment(sketch, "E336", {"start": v(-18.5, -124.9) * mm, "end": v(-18.75, -125.47) * mm});
            skLineSegment(sketch, "E337", {"start": v(-18.75, -125.47) * mm, "end": v(-19.3, -126.63) * mm});
            skLineSegment(sketch, "E338", {"start": v(-19.3, -126.63) * mm, "end": v(-19.57, -127.2) * mm});
            skLineSegment(sketch, "E339", {"start": v(-19.57, -127.2) * mm, "end": v(-21.18, -127.05) * mm});
            skLineSegment(sketch, "E340", {"start": v(-21.18, -127.05) * mm, "end": v(-21.35, -126.43) * mm});
            skLineSegment(sketch, "E341", {"start": v(-21.35, -126.43) * mm, "end": v(-21.65, -125.2) * mm});
            skLineSegment(sketch, "E342", {"start": v(-21.65, -125.2) * mm, "end": v(-21.8, -124.57) * mm});
            skLineSegment(sketch, "E343", {"start": v(-21.8, -124.57) * mm, "end": v(-23.42, -124.38) * mm});
            skLineSegment(sketch, "E344", {"start": v(-23.42, -124.38) * mm, "end": v(-23.7, -124.95) * mm});
            skLineSegment(sketch, "E345", {"start": v(-23.7, -124.95) * mm, "end": v(-24.28, -126.09) * mm});
            skLineSegment(sketch, "E346", {"start": v(-24.28, -126.09) * mm, "end": v(-24.6, -126.65) * mm});
            skLineSegment(sketch, "E347", {"start": v(-24.6, -126.65) * mm, "end": v(-26.19, -126.43) * mm});
            skLineSegment(sketch, "E348", {"start": v(-26.19, -126.43) * mm, "end": v(-26.33, -125.8) * mm});
            skLineSegment(sketch, "E349", {"start": v(-26.33, -125.8) * mm, "end": v(-26.59, -124.56) * mm});
            skLineSegment(sketch, "E350", {"start": v(-26.59, -124.56) * mm, "end": v(-26.7, -123.93) * mm});
            skLineSegment(sketch, "E351", {"start": v(-26.7, -123.93) * mm, "end": v(-28.32, -123.68) * mm});
            skLineSegment(sketch, "E352", {"start": v(-28.32, -123.68) * mm, "end": v(-28.62, -124.24) * mm});
            skLineSegment(sketch, "E353", {"start": v(-28.62, -124.24) * mm, "end": v(-29.25, -125.35) * mm});
            skLineSegment(sketch, "E354", {"start": v(-29.25, -125.35) * mm, "end": v(-29.58, -125.9) * mm});
            skLineSegment(sketch, "E355", {"start": v(-29.58, -125.9) * mm, "end": v(-31.17, -125.62) * mm});
            skLineSegment(sketch, "E356", {"start": v(-31.17, -125.62) * mm, "end": v(-31.29, -124.99) * mm});
            skLineSegment(sketch, "E357", {"start": v(-31.29, -124.99) * mm, "end": v(-31.5, -123.73) * mm});
            skLineSegment(sketch, "E358", {"start": v(-31.5, -123.73) * mm, "end": v(-31.58, -123.1) * mm});
            skLineSegment(sketch, "E359", {"start": v(-31.58, -123.1) * mm, "end": v(-33.2, -122.78) * mm});
            skLineSegment(sketch, "E360", {"start": v(-33.2, -122.78) * mm, "end": v(-33.52, -123.33) * mm});
            skLineSegment(sketch, "E361", {"start": v(-33.52, -123.33) * mm, "end": v(-34.19, -124.41) * mm});
            skLineSegment(sketch, "E362", {"start": v(-34.19, -124.41) * mm, "end": v(-34.54, -124.95) * mm});
            skLineSegment(sketch, "E363", {"start": v(-34.54, -124.95) * mm, "end": v(-36.11, -124.6) * mm});
            skLineSegment(sketch, "E364", {"start": v(-36.11, -124.6) * mm, "end": v(-36.2, -123.97) * mm});
            skLineSegment(sketch, "E365", {"start": v(-36.2, -123.97) * mm, "end": v(-36.36, -122.7) * mm});
            skLineSegment(sketch, "E366", {"start": v(-36.36, -122.7) * mm, "end": v(-36.43, -122.07) * mm});
            skLineSegment(sketch, "E367", {"start": v(-36.43, -122.07) * mm, "end": v(-38.03, -121.69) * mm});
            skLineSegment(sketch, "E368", {"start": v(-38.03, -121.69) * mm, "end": v(-38.37, -122.22) * mm});
            skLineSegment(sketch, "E369", {"start": v(-38.37, -122.22) * mm, "end": v(-39.08, -123.28) * mm});
            skLineSegment(sketch, "E370", {"start": v(-39.08, -123.28) * mm, "end": v(-39.45, -123.8) * mm});
            skLineSegment(sketch, "E371", {"start": v(-39.45, -123.8) * mm, "end": v(-41.01, -123.4) * mm});
            skLineSegment(sketch, "E372", {"start": v(-41.01, -123.4) * mm, "end": v(-41.08, -122.76) * mm});
            skLineSegment(sketch, "E373", {"start": v(-41.08, -122.76) * mm, "end": v(-41.19, -121.49) * mm});
            skLineSegment(sketch, "E374", {"start": v(-41.19, -121.49) * mm, "end": v(-41.23, -120.86) * mm});
            skLineSegment(sketch, "E375", {"start": v(-41.23, -120.86) * mm, "end": v(-42.8, -120.4) * mm});
            skLineSegment(sketch, "E376", {"start": v(-42.8, -120.4) * mm, "end": v(-43.17, -120.93) * mm});
            skLineSegment(sketch, "E377", {"start": v(-43.17, -120.93) * mm, "end": v(-43.93, -121.96) * mm});
            skLineSegment(sketch, "E378", {"start": v(-43.93, -121.96) * mm, "end": v(-44.32, -122.47) * mm});
            skLineSegment(sketch, "E379", {"start": v(-44.32, -122.47) * mm, "end": v(-45.86, -122) * mm});
            skLineSegment(sketch, "E380", {"start": v(-45.86, -122) * mm, "end": v(-45.9, -121.36) * mm});
            skLineSegment(sketch, "E381", {"start": v(-45.9, -121.36) * mm, "end": v(-45.96, -120.08) * mm});
            skLineSegment(sketch, "E382", {"start": v(-45.96, -120.08) * mm, "end": v(-45.98, -119.45) * mm});
            skLineSegment(sketch, "E383", {"start": v(-45.98, -119.45) * mm, "end": v(-47.54, -118.94) * mm});
            skLineSegment(sketch, "E384", {"start": v(-47.54, -118.94) * mm, "end": v(-47.92, -119.45) * mm});
            skLineSegment(sketch, "E385", {"start": v(-47.92, -119.45) * mm, "end": v(-48.72, -120.44) * mm});
            skLineSegment(sketch, "E386", {"start": v(-48.72, -120.44) * mm, "end": v(-49.13, -120.94) * mm});
            skLineSegment(sketch, "E387", {"start": v(-49.13, -120.94) * mm, "end": v(-50.65, -120.4) * mm});
            skLineSegment(sketch, "E388", {"start": v(-50.65, -120.4) * mm, "end": v(-50.67, -119.77) * mm});
            skLineSegment(sketch, "E389", {"start": v(-50.67, -119.77) * mm, "end": v(-50.68, -118.5) * mm});
            skLineSegment(sketch, "E390", {"start": v(-50.68, -118.5) * mm, "end": v(-50.67, -117.86) * mm});
            skLineSegment(sketch, "E391", {"start": v(-50.67, -117.86) * mm, "end": v(-52.2, -117.29) * mm});
            skLineSegment(sketch, "E392", {"start": v(-52.2, -117.29) * mm, "end": v(-52.61, -117.78) * mm});
            skLineSegment(sketch, "E393", {"start": v(-52.61, -117.78) * mm, "end": v(-53.44, -118.74) * mm});
            skLineSegment(sketch, "E394", {"start": v(-53.44, -118.74) * mm, "end": v(-53.88, -119.22) * mm});
            skLineSegment(sketch, "E395", {"start": v(-53.88, -119.22) * mm, "end": v(-55.38, -118.63) * mm});
            skLineSegment(sketch, "E396", {"start": v(-55.38, -118.63) * mm, "end": v(-55.37, -117.99) * mm});
            skLineSegment(sketch, "E397", {"start": v(-55.37, -117.99) * mm, "end": v(-55.32, -116.71) * mm});
            skLineSegment(sketch, "E398", {"start": v(-55.32, -116.71) * mm, "end": v(-55.29, -116.08) * mm});
            skLineSegment(sketch, "E399", {"start": v(-55.29, -116.08) * mm, "end": v(-56.8, -115.45) * mm});
            skLineSegment(sketch, "E400", {"start": v(-56.8, -115.45) * mm, "end": v(-57.23, -115.92) * mm});
            skLineSegment(sketch, "E401", {"start": v(-57.23, -115.92) * mm, "end": v(-58.1, -116.86) * mm});
            skLineSegment(sketch, "E402", {"start": v(-58.1, -116.86) * mm, "end": v(-58.55, -117.32) * mm});
            skLineSegment(sketch, "E403", {"start": v(-58.55, -117.32) * mm, "end": v(-60.03, -116.67) * mm});
            skLineSegment(sketch, "E404", {"start": v(-60.03, -116.67) * mm, "end": v(-60, -116.03) * mm});
            skLineSegment(sketch, "E405", {"start": v(-60, -116.03) * mm, "end": v(-59.9, -114.75) * mm});
            skLineSegment(sketch, "E406", {"start": v(-59.9, -114.75) * mm, "end": v(-59.84, -114.12) * mm});
            skLineSegment(sketch, "E407", {"start": v(-59.84, -114.12) * mm, "end": v(-61.33, -113.43) * mm});
            skLineSegment(sketch, "E408", {"start": v(-61.33, -113.43) * mm, "end": v(-61.77, -113.89) * mm});
            skLineSegment(sketch, "E409", {"start": v(-61.77, -113.89) * mm, "end": v(-62.68, -114.79) * mm});
            skLineSegment(sketch, "E410", {"start": v(-62.68, -114.79) * mm, "end": v(-63.14, -115.23) * mm});
            skLineSegment(sketch, "E411", {"start": v(-63.14, -115.23) * mm, "end": v(-64.6, -114.52) * mm});
            skLineSegment(sketch, "E412", {"start": v(-64.6, -114.52) * mm, "end": v(-64.54, -113.88) * mm});
            skLineSegment(sketch, "E413", {"start": v(-64.54, -113.88) * mm, "end": v(-64.4, -112.62) * mm});
            skLineSegment(sketch, "E414", {"start": v(-64.4, -112.62) * mm, "end": v(-64.3, -111.99) * mm});
            skLineSegment(sketch, "E415", {"start": v(-64.3, -111.99) * mm, "end": v(-65.77, -111.24) * mm});
            skLineSegment(sketch, "E416", {"start": v(-65.77, -111.24) * mm, "end": v(-66.23, -111.68) * mm});
            skLineSegment(sketch, "E417", {"start": v(-66.23, -111.68) * mm, "end": v(-67.17, -112.54) * mm});
            skLineSegment(sketch, "E418", {"start": v(-67.17, -112.54) * mm, "end": v(-67.65, -112.96) * mm});
            skLineSegment(sketch, "E419", {"start": v(-67.65, -112.96) * mm, "end": v(-69.07, -112.2) * mm});
            skLineSegment(sketch, "E420", {"start": v(-69.07, -112.2) * mm, "end": v(-69, -111.56) * mm});
            skLineSegment(sketch, "E421", {"start": v(-69, -111.56) * mm, "end": v(-68.8, -110.3) * mm});
            skLineSegment(sketch, "E422", {"start": v(-68.8, -110.3) * mm, "end": v(-68.69, -109.68) * mm});
            skLineSegment(sketch, "E423", {"start": v(-68.69, -109.68) * mm, "end": v(-70.12, -108.87) * mm});
            skLineSegment(sketch, "E424", {"start": v(-70.12, -108.87) * mm, "end": v(-70.6, -109.3) * mm});
            skLineSegment(sketch, "E425", {"start": v(-70.6, -109.3) * mm, "end": v(-71.57, -110.11) * mm});
            skLineSegment(sketch, "E426", {"start": v(-71.57, -110.11) * mm, "end": v(-72.07, -110.52) * mm});
            skLineSegment(sketch, "E427", {"start": v(-72.07, -110.52) * mm, "end": v(-73.46, -109.7) * mm});
            skLineSegment(sketch, "E428", {"start": v(-73.46, -109.7) * mm, "end": v(-73.35, -109.07) * mm});
            skLineSegment(sketch, "E429", {"start": v(-73.35, -109.07) * mm, "end": v(-73.1, -107.81) * mm});
            skLineSegment(sketch, "E430", {"start": v(-73.1, -107.81) * mm, "end": v(-72.97, -107.2) * mm});
            skLineSegment(sketch, "E431", {"start": v(-72.97, -107.2) * mm, "end": v(-74.37, -106.33) * mm});
            skLineSegment(sketch, "E432", {"start": v(-74.37, -106.33) * mm, "end": v(-74.86, -106.73) * mm});
            skLineSegment(sketch, "E433", {"start": v(-74.86, -106.73) * mm, "end": v(-75.87, -107.52) * mm});
            skLineSegment(sketch, "E434", {"start": v(-75.87, -107.52) * mm, "end": v(-76.39, -107.9) * mm});
            skLineSegment(sketch, "E435", {"start": v(-76.39, -107.9) * mm, "end": v(-77.74, -107.03) * mm});
            skLineSegment(sketch, "E436", {"start": v(-77.74, -107.03) * mm, "end": v(-77.6, -106.4) * mm});
            skLineSegment(sketch, "E437", {"start": v(-77.6, -106.4) * mm, "end": v(-77.31, -105.16) * mm});
            skLineSegment(sketch, "E438", {"start": v(-77.31, -105.16) * mm, "end": v(-77.15, -104.55) * mm});
            skLineSegment(sketch, "E439", {"start": v(-77.15, -104.55) * mm, "end": v(-78.52, -103.63) * mm});
            skLineSegment(sketch, "E440", {"start": v(-78.52, -103.63) * mm, "end": v(-79.03, -104.01) * mm});
            skLineSegment(sketch, "E441", {"start": v(-79.03, -104.01) * mm, "end": v(-80.06, -104.75) * mm});
            skLineSegment(sketch, "E442", {"start": v(-80.06, -104.75) * mm, "end": v(-80.6, -105.12) * mm});
            skLineSegment(sketch, "E443", {"start": v(-80.6, -105.12) * mm, "end": v(-81.92, -104.2) * mm});
            skLineSegment(sketch, "E444", {"start": v(-81.92, -104.2) * mm, "end": v(-81.76, -103.57) * mm});
            skLineSegment(sketch, "E445", {"start": v(-81.76, -103.57) * mm, "end": v(-81.41, -102.34) * mm});
            skLineSegment(sketch, "E446", {"start": v(-81.41, -102.34) * mm, "end": v(-81.23, -101.73) * mm});
            skLineSegment(sketch, "E447", {"start": v(-81.23, -101.73) * mm, "end": v(-82.56, -100.76) * mm});
            skLineSegment(sketch, "E448", {"start": v(-82.56, -100.76) * mm, "end": v(-83.08, -101.12) * mm});
            skLineSegment(sketch, "E449", {"start": v(-83.08, -101.12) * mm, "end": v(-84.15, -101.83) * mm});
            skLineSegment(sketch, "E450", {"start": v(-84.15, -101.83) * mm, "end": v(-84.7, -102.17) * mm});
            skLineSegment(sketch, "E451", {"start": v(-84.7, -102.17) * mm, "end": v(-85.97, -101.2) * mm});
            skLineSegment(sketch, "E452", {"start": v(-85.97, -101.2) * mm, "end": v(-85.8, -100.58) * mm});
            skLineSegment(sketch, "E453", {"start": v(-85.8, -100.58) * mm, "end": v(-85.4, -99.36) * mm});
            skLineSegment(sketch, "E454", {"start": v(-85.4, -99.36) * mm, "end": v(-85.2, -98.76) * mm});
            skLineSegment(sketch, "E455", {"start": v(-85.2, -98.76) * mm, "end": v(-86.48, -97.74) * mm});
            skLineSegment(sketch, "E456", {"start": v(-86.48, -97.74) * mm, "end": v(-87.02, -98.08) * mm});
            skLineSegment(sketch, "E457", {"start": v(-87.02, -98.08) * mm, "end": v(-88.1, -98.74) * mm});
            skLineSegment(sketch, "E458", {"start": v(-88.1, -98.74) * mm, "end": v(-88.67, -99.06) * mm});
            skLineSegment(sketch, "E459", {"start": v(-88.67, -99.06) * mm, "end": v(-89.91, -98.03) * mm});
            skLineSegment(sketch, "E460", {"start": v(-89.91, -98.03) * mm, "end": v(-89.7, -97.43) * mm});
            skLineSegment(sketch, "E461", {"start": v(-89.7, -97.43) * mm, "end": v(-89.27, -96.23) * mm});
            skLineSegment(sketch, "E462", {"start": v(-89.27, -96.23) * mm, "end": v(-89.03, -95.64) * mm});
            skLineSegment(sketch, "E463", {"start": v(-89.03, -95.64) * mm, "end": v(-90.28, -94.57) * mm});
            skLineSegment(sketch, "E464", {"start": v(-90.28, -94.57) * mm, "end": v(-90.83, -94.88) * mm});
            skLineSegment(sketch, "E465", {"start": v(-90.83, -94.88) * mm, "end": v(-91.95, -95.5) * mm});
            skLineSegment(sketch, "E466", {"start": v(-91.95, -95.5) * mm, "end": v(-92.52, -95.8) * mm});
            skLineSegment(sketch, "E467", {"start": v(-92.52, -95.8) * mm, "end": v(-93.72, -94.72) * mm});
            skLineSegment(sketch, "E468", {"start": v(-93.72, -94.72) * mm, "end": v(-93.49, -94.12) * mm});
            skLineSegment(sketch, "E469", {"start": v(-93.49, -94.12) * mm, "end": v(-93, -92.94) * mm});
            skLineSegment(sketch, "E470", {"start": v(-93, -92.94) * mm, "end": v(-92.75, -92.36) * mm});
            skLineSegment(sketch, "E471", {"start": v(-92.75, -92.36) * mm, "end": v(-93.95, -91.24) * mm});
            skLineSegment(sketch, "E472", {"start": v(-93.95, -91.24) * mm, "end": v(-94.51, -91.54) * mm});
            skLineSegment(sketch, "E473", {"start": v(-94.51, -91.54) * mm, "end": v(-95.66, -92.1) * mm});
            skLineSegment(sketch, "E474", {"start": v(-95.66, -92.1) * mm, "end": v(-96.24, -92.38) * mm});
            skLineSegment(sketch, "E475", {"start": v(-96.24, -92.38) * mm, "end": v(-97.4, -91.26) * mm});
            skLineSegment(sketch, "E476", {"start": v(-97.4, -91.26) * mm, "end": v(-97.14, -90.67) * mm});
            skLineSegment(sketch, "E477", {"start": v(-97.14, -90.67) * mm, "end": v(-96.6, -89.51) * mm});
            skLineSegment(sketch, "E478", {"start": v(-96.6, -89.51) * mm, "end": v(-96.33, -88.94) * mm});
            skLineSegment(sketch, "E479", {"start": v(-96.33, -88.94) * mm, "end": v(-97.5, -87.78) * mm});
            skLineSegment(sketch, "E480", {"start": v(-97.5, -87.78) * mm, "end": v(-98.06, -88.05) * mm});
            skLineSegment(sketch, "E481", {"start": v(-98.06, -88.05) * mm, "end": v(-99.23, -88.57) * mm});
            skLineSegment(sketch, "E482", {"start": v(-99.23, -88.57) * mm, "end": v(-99.82, -88.83) * mm});
            skLineSegment(sketch, "E483", {"start": v(-99.82, -88.83) * mm, "end": v(-100.93, -87.66) * mm});
            skLineSegment(sketch, "E484", {"start": v(-100.93, -87.66) * mm, "end": v(-100.65, -87.08) * mm});
            skLineSegment(sketch, "E485", {"start": v(-100.65, -87.08) * mm, "end": v(-100.08, -85.94) * mm});
            skLineSegment(sketch, "E486", {"start": v(-100.08, -85.94) * mm, "end": v(-99.78, -85.38) * mm});
            skLineSegment(sketch, "E487", {"start": v(-99.78, -85.38) * mm, "end": v(-100.89, -84.17) * mm});
            skLineSegment(sketch, "E488", {"start": v(-100.89, -84.17) * mm, "end": v(-101.47, -84.42) * mm});
            skLineSegment(sketch, "E489", {"start": v(-101.47, -84.42) * mm, "end": v(-102.65, -84.9) * mm});
            skLineSegment(sketch, "E490", {"start": v(-102.65, -84.9) * mm, "end": v(-103.25, -85.13) * mm});
            skLineSegment(sketch, "E491", {"start": v(-103.25, -85.13) * mm, "end": v(-104.32, -83.92) * mm});
            skLineSegment(sketch, "E492", {"start": v(-104.32, -83.92) * mm, "end": v(-104.02, -83.35) * mm});
            skLineSegment(sketch, "E493", {"start": v(-104.02, -83.35) * mm, "end": v(-103.4, -82.24) * mm});
            skLineSegment(sketch, "E494", {"start": v(-103.4, -82.24) * mm, "end": v(-103.08, -81.7) * mm});
            skLineSegment(sketch, "E495", {"start": v(-103.08, -81.7) * mm, "end": v(-104.14, -80.44) * mm});
            skLineSegment(sketch, "E496", {"start": v(-104.14, -80.44) * mm, "end": v(-104.73, -80.67) * mm});
            skLineSegment(sketch, "E497", {"start": v(-104.73, -80.67) * mm, "end": v(-105.93, -81.1) * mm});
            skLineSegment(sketch, "E498", {"start": v(-105.93, -81.1) * mm, "end": v(-106.54, -81.3) * mm});
            skLineSegment(sketch, "E499", {"start": v(-106.54, -81.3) * mm, "end": v(-107.56, -80.05) * mm});
            skLineSegment(sketch, "E500", {"start": v(-107.56, -80.05) * mm, "end": v(-107.24, -79.5) * mm});
            skLineSegment(sketch, "E501", {"start": v(-107.24, -79.5) * mm, "end": v(-106.57, -78.4) * mm});
            skLineSegment(sketch, "E502", {"start": v(-106.57, -78.4) * mm, "end": v(-106.23, -77.87) * mm});
            skLineSegment(sketch, "E503", {"start": v(-106.23, -77.87) * mm, "end": v(-107.24, -76.58) * mm});
            skLineSegment(sketch, "E504", {"start": v(-107.24, -76.58) * mm, "end": v(-107.84, -76.78) * mm});
            skLineSegment(sketch, "E505", {"start": v(-107.84, -76.78) * mm, "end": v(-109.06, -77.17) * mm});
            skLineSegment(sketch, "E506", {"start": v(-109.06, -77.17) * mm, "end": v(-109.68, -77.35) * mm});
            skLineSegment(sketch, "E507", {"start": v(-109.68, -77.35) * mm, "end": v(-110.65, -76.06) * mm});
            skLineSegment(sketch, "E508", {"start": v(-110.65, -76.06) * mm, "end": v(-110.3, -75.52) * mm});
            skLineSegment(sketch, "E509", {"start": v(-110.3, -75.52) * mm, "end": v(-109.6, -74.45) * mm});
            skLineSegment(sketch, "E510", {"start": v(-109.6, -74.45) * mm, "end": v(-109.23, -73.93) * mm});
            skLineSegment(sketch, "E511", {"start": v(-109.23, -73.93) * mm, "end": v(-110.2, -72.6) * mm});
            skLineSegment(sketch, "E512", {"start": v(-110.2, -72.6) * mm, "end": v(-110.8, -72.78) * mm});
            skLineSegment(sketch, "E513", {"start": v(-110.8, -72.78) * mm, "end": v(-112.03, -73.12) * mm});
            skLineSegment(sketch, "E514", {"start": v(-112.03, -73.12) * mm, "end": v(-112.65, -73.27) * mm});
            skLineSegment(sketch, "E515", {"start": v(-112.65, -73.27) * mm, "end": v(-113.57, -71.94) * mm});
            skLineSegment(sketch, "E516", {"start": v(-113.57, -71.94) * mm, "end": v(-113.2, -71.42) * mm});
            skLineSegment(sketch, "E517", {"start": v(-113.2, -71.42) * mm, "end": v(-112.46, -70.38) * mm});
            skLineSegment(sketch, "E518", {"start": v(-112.46, -70.38) * mm, "end": v(-112.07, -69.88) * mm});
            skLineSegment(sketch, "E519", {"start": v(-112.07, -69.88) * mm, "end": v(-112.98, -68.5) * mm});
            skLineSegment(sketch, "E520", {"start": v(-112.98, -68.5) * mm, "end": v(-113.6, -68.66) * mm});
            skLineSegment(sketch, "E521", {"start": v(-113.6, -68.66) * mm, "end": v(-114.84, -68.95) * mm});
            skLineSegment(sketch, "E522", {"start": v(-114.84, -68.95) * mm, "end": v(-115.47, -69.08) * mm});
            skLineSegment(sketch, "E523", {"start": v(-115.47, -69.08) * mm, "end": v(-116.33, -67.72) * mm});
            skLineSegment(sketch, "E524", {"start": v(-116.33, -67.72) * mm, "end": v(-115.94, -67.2) * mm});
            skLineSegment(sketch, "E525", {"start": v(-115.94, -67.2) * mm, "end": v(-115.15, -66.2) * mm});
            skLineSegment(sketch, "E526", {"start": v(-115.15, -66.2) * mm, "end": v(-114.75, -65.71) * mm});
            skLineSegment(sketch, "E527", {"start": v(-114.75, -65.71) * mm, "end": v(-115.6, -64.3) * mm});
            skLineSegment(sketch, "E528", {"start": v(-115.6, -64.3) * mm, "end": v(-116.22, -64.44) * mm});
            skLineSegment(sketch, "E529", {"start": v(-116.22, -64.44) * mm, "end": v(-117.48, -64.68) * mm});
            skLineSegment(sketch, "E530", {"start": v(-117.48, -64.68) * mm, "end": v(-118.11, -64.78) * mm});
            skLineSegment(sketch, "E531", {"start": v(-118.11, -64.78) * mm, "end": v(-118.92, -63.39) * mm});
            skLineSegment(sketch, "E532", {"start": v(-118.92, -63.39) * mm, "end": v(-118.51, -62.89) * mm});
            skLineSegment(sketch, "E533", {"start": v(-118.51, -62.89) * mm, "end": v(-117.69, -61.92) * mm});
            skLineSegment(sketch, "E534", {"start": v(-117.69, -61.92) * mm, "end": v(-117.26, -61.45) * mm});
            skLineSegment(sketch, "E535", {"start": v(-117.26, -61.45) * mm, "end": v(-118.06, -60) * mm});
            skLineSegment(sketch, "E536", {"start": v(-118.06, -60) * mm, "end": v(-118.69, -60.11) * mm});
            skLineSegment(sketch, "E537", {"start": v(-118.69, -60.11) * mm, "end": v(-119.95, -60.3) * mm});
            skLineSegment(sketch, "E538", {"start": v(-119.95, -60.3) * mm, "end": v(-120.59, -60.38) * mm});
            skLineSegment(sketch, "E539", {"start": v(-120.59, -60.38) * mm, "end": v(-121.34, -58.96) * mm});
            skLineSegment(sketch, "E540", {"start": v(-121.34, -58.96) * mm, "end": v(-120.91, -58.48) * mm});
            skLineSegment(sketch, "E541", {"start": v(-120.91, -58.48) * mm, "end": v(-120.05, -57.54) * mm});
            skLineSegment(sketch, "E542", {"start": v(-120.05, -57.54) * mm, "end": v(-119.6, -57.08) * mm});
            skLineSegment(sketch, "E543", {"start": v(-119.6, -57.08) * mm, "end": v(-120.35, -55.61) * mm});
            skLineSegment(sketch, "E544", {"start": v(-120.35, -55.61) * mm, "end": v(-120.97, -55.7) * mm});
            skLineSegment(sketch, "E545", {"start": v(-120.97, -55.7) * mm, "end": v(-122.24, -55.83) * mm});
            skLineSegment(sketch, "E546", {"start": v(-122.24, -55.83) * mm, "end": v(-122.88, -55.89) * mm});
            skLineSegment(sketch, "E547", {"start": v(-122.88, -55.89) * mm, "end": v(-123.58, -54.43) * mm});
            skLineSegment(sketch, "E548", {"start": v(-123.58, -54.43) * mm, "end": v(-123.13, -53.97) * mm});
            skLineSegment(sketch, "E549", {"start": v(-123.13, -53.97) * mm, "end": v(-122.23, -53.07) * mm});
            skLineSegment(sketch, "E550", {"start": v(-122.23, -53.07) * mm, "end": v(-121.77, -52.63) * mm});
            skLineSegment(sketch, "E551", {"start": v(-121.77, -52.63) * mm, "end": v(-122.45, -51.13) * mm});
            skLineSegment(sketch, "E552", {"start": v(-122.45, -51.13) * mm, "end": v(-123.09, -51.2) * mm});
            skLineSegment(sketch, "E553", {"start": v(-123.09, -51.2) * mm, "end": v(-124.36, -51.28) * mm});
            skLineSegment(sketch, "E554", {"start": v(-124.36, -51.28) * mm, "end": v(-125, -51.3) * mm});
            skLineSegment(sketch, "E555", {"start": v(-125, -51.3) * mm, "end": v(-125.64, -49.83) * mm});
            skLineSegment(sketch, "E556", {"start": v(-125.64, -49.83) * mm, "end": v(-125.18, -49.38) * mm});
            skLineSegment(sketch, "E557", {"start": v(-125.18, -49.38) * mm, "end": v(-124.24, -48.51) * mm});
            skLineSegment(sketch, "E558", {"start": v(-124.24, -48.51) * mm, "end": v(-123.76, -48.1) * mm});
            skLineSegment(sketch, "E559", {"start": v(-123.76, -48.1) * mm, "end": v(-124.39, -46.57) * mm});
            skLineSegment(sketch, "E560", {"start": v(-124.39, -46.57) * mm, "end": v(-125.02, -46.6) * mm});
            skLineSegment(sketch, "E561", {"start": v(-125.02, -46.6) * mm, "end": v(-126.3, -46.64) * mm});
            skLineSegment(sketch, "E562", {"start": v(-126.3, -46.64) * mm, "end": v(-126.94, -46.65) * mm});
            skLineSegment(sketch, "E563", {"start": v(-126.94, -46.65) * mm, "end": v(-127.52, -45.14) * mm});
            skLineSegment(sketch, "E564", {"start": v(-127.52, -45.14) * mm, "end": v(-127.04, -44.71) * mm});
            skLineSegment(sketch, "E565", {"start": v(-127.04, -44.71) * mm, "end": v(-126.07, -43.89) * mm});
            skLineSegment(sketch, "E566", {"start": v(-126.07, -43.89) * mm, "end": v(-125.57, -43.48) * mm});
            skLineSegment(sketch, "E567", {"start": v(-125.57, -43.48) * mm, "end": v(-126.13, -41.94) * mm});
            skLineSegment(sketch, "E568", {"start": v(-126.13, -41.94) * mm, "end": v(-126.77, -41.95) * mm});
            skLineSegment(sketch, "E569", {"start": v(-126.77, -41.95) * mm, "end": v(-128.04, -41.93) * mm});
            skLineSegment(sketch, "E570", {"start": v(-128.04, -41.93) * mm, "end": v(-128.69, -41.91) * mm});
            skLineSegment(sketch, "E571", {"start": v(-128.69, -41.91) * mm, "end": v(-129.2, -40.39) * mm});
            skLineSegment(sketch, "E572", {"start": v(-129.2, -40.39) * mm, "end": v(-128.7, -39.98) * mm});
            skLineSegment(sketch, "E573", {"start": v(-128.7, -39.98) * mm, "end": v(-127.7, -39.19) * mm});
            skLineSegment(sketch, "E574", {"start": v(-127.7, -39.19) * mm, "end": v(-127.2, -38.8) * mm});
            skLineSegment(sketch, "E575", {"start": v(-127.2, -38.8) * mm, "end": v(-127.7, -37.24) * mm});
            skLineSegment(sketch, "E576", {"start": v(-127.7, -37.24) * mm, "end": v(-128.33, -37.22) * mm});
            skLineSegment(sketch, "E577", {"start": v(-128.33, -37.22) * mm, "end": v(-129.6, -37.16) * mm});
            skLineSegment(sketch, "E578", {"start": v(-129.6, -37.16) * mm, "end": v(-130.25, -37.11) * mm});
            skLineSegment(sketch, "E579", {"start": v(-130.25, -37.11) * mm, "end": v(-130.7, -35.57) * mm});
            skLineSegment(sketch, "E580", {"start": v(-130.7, -35.57) * mm, "end": v(-130.2, -35.18) * mm});
            skLineSegment(sketch, "E581", {"start": v(-130.2, -35.18) * mm, "end": v(-129.16, -34.43) * mm});
            skLineSegment(sketch, "E582", {"start": v(-129.16, -34.43) * mm, "end": v(-128.64, -34.07) * mm});
            skLineSegment(sketch, "E583", {"start": v(-128.64, -34.07) * mm, "end": v(-129.08, -32.48) * mm});
            skLineSegment(sketch, "E584", {"start": v(-129.08, -32.48) * mm, "end": v(-129.7, -32.44) * mm});
            skLineSegment(sketch, "E585", {"start": v(-129.7, -32.44) * mm, "end": v(-130.98, -32.33) * mm});
            skLineSegment(sketch, "E586", {"start": v(-130.98, -32.33) * mm, "end": v(-131.62, -32.26) * mm});
            skLineSegment(sketch, "E587", {"start": v(-131.62, -32.26) * mm, "end": v(-132.02, -30.7) * mm});
            skLineSegment(sketch, "E588", {"start": v(-132.02, -30.7) * mm, "end": v(-131.49, -30.33) * mm});
            skLineSegment(sketch, "E589", {"start": v(-131.49, -30.33) * mm, "end": v(-130.43, -29.62) * mm});
            skLineSegment(sketch, "E590", {"start": v(-130.43, -29.62) * mm, "end": v(-129.9, -29.28) * mm});
            skLineSegment(sketch, "E591", {"start": v(-129.9, -29.28) * mm, "end": v(-130.27, -27.68) * mm});
            skLineSegment(sketch, "E592", {"start": v(-130.27, -27.68) * mm, "end": v(-130.9, -27.6) * mm});
            skLineSegment(sketch, "E593", {"start": v(-130.9, -27.6) * mm, "end": v(-132.16, -27.44) * mm});
            skLineSegment(sketch, "E594", {"start": v(-132.16, -27.44) * mm, "end": v(-132.8, -27.35) * mm});
            skLineSegment(sketch, "E595", {"start": v(-132.8, -27.35) * mm, "end": v(-133.13, -25.77) * mm});
            skLineSegment(sketch, "E596", {"start": v(-133.13, -25.77) * mm, "end": v(-132.6, -25.42) * mm});
            skLineSegment(sketch, "E597", {"start": v(-132.6, -25.42) * mm, "end": v(-131.5, -24.76) * mm});
            skLineSegment(sketch, "E598", {"start": v(-131.5, -24.76) * mm, "end": v(-130.95, -24.44) * mm});
            skLineSegment(sketch, "E599", {"start": v(-130.95, -24.44) * mm, "end": v(-131.26, -22.83) * mm});
            skLineSegment(sketch, "E600", {"start": v(-131.26, -22.83) * mm, "end": v(-131.89, -22.73) * mm});
            skLineSegment(sketch, "E601", {"start": v(-131.89, -22.73) * mm, "end": v(-133.15, -22.52) * mm});
            skLineSegment(sketch, "E602", {"start": v(-133.15, -22.52) * mm, "end": v(-133.78, -22.4) * mm});
            skLineSegment(sketch, "E603", {"start": v(-133.78, -22.4) * mm, "end": v(-134.05, -20.8) * mm});
            skLineSegment(sketch, "E604", {"start": v(-134.05, -20.8) * mm, "end": v(-133.5, -20.48) * mm});
            skLineSegment(sketch, "E605", {"start": v(-133.5, -20.48) * mm, "end": v(-132.38, -19.86) * mm});
            skLineSegment(sketch, "E606", {"start": v(-132.38, -19.86) * mm, "end": v(-131.82, -19.56) * mm});
            skLineSegment(sketch, "E607", {"start": v(-131.82, -19.56) * mm, "end": v(-132.07, -17.94) * mm});
            skLineSegment(sketch, "E608", {"start": v(-132.07, -17.94) * mm, "end": v(-132.7, -17.82) * mm});
            skLineSegment(sketch, "E609", {"start": v(-132.7, -17.82) * mm, "end": v(-133.94, -17.56) * mm});
            skLineSegment(sketch, "E610", {"start": v(-133.94, -17.56) * mm, "end": v(-134.57, -17.41) * mm});
            skLineSegment(sketch, "E611", {"start": v(-134.57, -17.41) * mm, "end": v(-134.78, -15.81) * mm});
            skLineSegment(sketch, "E612", {"start": v(-134.78, -15.81) * mm, "end": v(-134.2, -15.51) * mm});
            skLineSegment(sketch, "E613", {"start": v(-134.2, -15.51) * mm, "end": v(-133.07, -14.93) * mm});
            skLineSegment(sketch, "E614", {"start": v(-133.07, -14.93) * mm, "end": v(-132.5, -14.66) * mm});
            skLineSegment(sketch, "E615", {"start": v(-132.5, -14.66) * mm, "end": v(-132.68, -13.03) * mm});
            skLineSegment(sketch, "E616", {"start": v(-132.68, -13.03) * mm, "end": v(-133.3, -12.88) * mm});
            skLineSegment(sketch, "E617", {"start": v(-133.3, -12.88) * mm, "end": v(-134.54, -12.57) * mm});
            skLineSegment(sketch, "E618", {"start": v(-134.54, -12.57) * mm, "end": v(-135.15, -12.4) * mm});
            skLineSegment(sketch, "E619", {"start": v(-135.15, -12.4) * mm, "end": v(-135.3, -10.8) * mm});
            skLineSegment(sketch, "E620", {"start": v(-135.3, -10.8) * mm, "end": v(-134.72, -10.51) * mm});
            skLineSegment(sketch, "E621", {"start": v(-134.72, -10.51) * mm, "end": v(-133.56, -9.98) * mm});
            skLineSegment(sketch, "E622", {"start": v(-133.56, -9.98) * mm, "end": v(-132.98, -9.73) * mm});
            skLineSegment(sketch, "E623", {"start": v(-132.98, -9.73) * mm, "end": v(-133.1, -8.1) * mm});
            skLineSegment(sketch, "E624", {"start": v(-133.1, -8.1) * mm, "end": v(-133.7, -7.92) * mm});
            skLineSegment(sketch, "E625", {"start": v(-133.7, -7.92) * mm, "end": v(-134.93, -7.56) * mm});
            skLineSegment(sketch, "E626", {"start": v(-134.93, -7.56) * mm, "end": v(-135.55, -7.37) * mm});
            skLineSegment(sketch, "E627", {"start": v(-135.55, -7.37) * mm, "end": v(-135.63, -5.76) * mm});
            skLineSegment(sketch, "E628", {"start": v(-135.63, -5.76) * mm, "end": v(-135.04, -5.5) * mm});
            skLineSegment(sketch, "E629", {"start": v(-135.04, -5.5) * mm, "end": v(-133.86, -5.01) * mm});
            skLineSegment(sketch, "E630", {"start": v(-133.86, -5.01) * mm, "end": v(-133.27, -4.79) * mm});
            skLineSegment(sketch, "E631", {"start": v(-133.27, -4.79) * mm, "end": v(-133.32, -3.14) * mm});
            skLineSegment(sketch, "E632", {"start": v(-133.32, -3.14) * mm, "end": v(-133.92, -2.95) * mm});
            skLineSegment(sketch, "E633", {"start": v(-133.92, -2.95) * mm, "end": v(-135.13, -2.54) * mm});
            skLineSegment(sketch, "E634", {"start": v(-135.13, -2.54) * mm, "end": v(-135.74, -2.32) * mm});
            skLineSegment(sketch, "E635", {"start": v(-135.74, -2.32) * mm, "end": v(-135.76, -0.71) * mm});
            skLineSegment(sketch, "E636", {"start": v(-135.76, -0.71) * mm, "end": v(-135.16, -0.48) * mm});
            skLineSegment(sketch, "E637", {"start": v(-135.16, -0.48) * mm, "end": v(-133.96, -0.04) * mm});
            skLineSegment(sketch, "E638", {"start": v(-133.96, -0.04) * mm, "end": v(-133.36, 0.17) * mm});
            skLineSegment(sketch, "E639", {"start": v(-133.36, 0.17) * mm, "end": v(-133.35, 1.8) * mm});
            skLineSegment(sketch, "E640", {"start": v(-133.35, 1.8) * mm, "end": v(-133.94, 2.02) * mm});
            skLineSegment(sketch, "E641", {"start": v(-133.94, 2.02) * mm, "end": v(-135.13, 2.48) * mm});
            skLineSegment(sketch, "E642", {"start": v(-135.13, 2.48) * mm, "end": v(-135.73, 2.72) * mm});
            skLineSegment(sketch, "E643", {"start": v(-135.73, 2.72) * mm, "end": v(-135.68, 4.33) * mm});
            skLineSegment(sketch, "E644", {"start": v(-135.68, 4.33) * mm, "end": v(-135.08, 4.54) * mm});
            skLineSegment(sketch, "E645", {"start": v(-135.08, 4.54) * mm, "end": v(-133.86, 4.94) * mm});
            skLineSegment(sketch, "E646", {"start": v(-133.86, 4.94) * mm, "end": v(-133.25, 5.12) * mm});
            skLineSegment(sketch, "E647", {"start": v(-133.25, 5.12) * mm, "end": v(-133.18, 6.76) * mm});
            skLineSegment(sketch, "E648", {"start": v(-133.18, 6.76) * mm, "end": v(-133.76, 7) * mm});
            skLineSegment(sketch, "E649", {"start": v(-133.76, 7) * mm, "end": v(-134.94, 7.5) * mm});
            skLineSegment(sketch, "E650", {"start": v(-134.94, 7.5) * mm, "end": v(-135.52, 7.77) * mm});
            skLineSegment(sketch, "E651", {"start": v(-135.52, 7.77) * mm, "end": v(-135.41, 9.37) * mm});
            skLineSegment(sketch, "E652", {"start": v(-135.41, 9.37) * mm, "end": v(-134.8, 9.56) * mm});
            skLineSegment(sketch, "E653", {"start": v(-134.8, 9.56) * mm, "end": v(-133.57, 9.9) * mm});
            skLineSegment(sketch, "E654", {"start": v(-133.57, 9.9) * mm, "end": v(-132.95, 10.06) * mm});
            skLineSegment(sketch, "E655", {"start": v(-132.95, 10.06) * mm, "end": v(-132.81, 11.7) * mm});
            skLineSegment(sketch, "E656", {"start": v(-132.81, 11.7) * mm, "end": v(-133.39, 11.96) * mm});
            skLineSegment(sketch, "E657", {"start": v(-133.39, 11.96) * mm, "end": v(-134.54, 12.5) * mm});
            skLineSegment(sketch, "E658", {"start": v(-134.54, 12.5) * mm, "end": v(-135.11, 12.8) * mm});
            skLineSegment(sketch, "E659", {"start": v(-135.11, 12.8) * mm, "end": v(-134.94, 14.4) * mm});
            skLineSegment(sketch, "E660", {"start": v(-134.94, 14.4) * mm, "end": v(-134.32, 14.56) * mm});
            skLineSegment(sketch, "E661", {"start": v(-134.32, 14.56) * mm, "end": v(-133.08, 14.86) * mm});
            skLineSegment(sketch, "E662", {"start": v(-133.08, 14.86) * mm, "end": v(-132.46, 14.99) * mm});
            skLineSegment(sketch, "E663", {"start": v(-132.46, 14.99) * mm, "end": v(-132.25, 16.62) * mm});
            skLineSegment(sketch, "E664", {"start": v(-132.25, 16.62) * mm, "end": v(-132.82, 16.9) * mm});
            skLineSegment(sketch, "E665", {"start": v(-132.82, 16.9) * mm, "end": v(-133.95, 17.5) * mm});
            skLineSegment(sketch, "E666", {"start": v(-133.95, 17.5) * mm, "end": v(-134.5, 17.8) * mm});
            skLineSegment(sketch, "E667", {"start": v(-134.5, 17.8) * mm, "end": v(-134.27, 19.4) * mm});
            skLineSegment(sketch, "E668", {"start": v(-134.27, 19.4) * mm, "end": v(-133.65, 19.54) * mm});
            skLineSegment(sketch, "E669", {"start": v(-133.65, 19.54) * mm, "end": v(-132.4, 19.78) * mm});
            skLineSegment(sketch, "E670", {"start": v(-132.4, 19.78) * mm, "end": v(-131.77, 19.9) * mm});
            skLineSegment(sketch, "E671", {"start": v(-131.77, 19.9) * mm, "end": v(-131.5, 21.51) * mm});
            skLineSegment(sketch, "E672", {"start": v(-131.5, 21.51) * mm, "end": v(-132.05, 21.82) * mm});
            skLineSegment(sketch, "E673", {"start": v(-132.05, 21.82) * mm, "end": v(-133.16, 22.46) * mm});
            skLineSegment(sketch, "E674", {"start": v(-133.16, 22.46) * mm, "end": v(-133.7, 22.8) * mm});
            skLineSegment(sketch, "E675", {"start": v(-133.7, 22.8) * mm, "end": v(-133.4, 24.37) * mm});
            skLineSegment(sketch, "E676", {"start": v(-133.4, 24.37) * mm, "end": v(-132.78, 24.49) * mm});
            skLineSegment(sketch, "E677", {"start": v(-132.78, 24.49) * mm, "end": v(-131.52, 24.68) * mm});
            skLineSegment(sketch, "E678", {"start": v(-131.52, 24.68) * mm, "end": v(-130.89, 24.76) * mm});
            skLineSegment(sketch, "E679", {"start": v(-130.89, 24.76) * mm, "end": v(-130.55, 26.37) * mm});
            skLineSegment(sketch, "E680", {"start": v(-130.55, 26.37) * mm, "end": v(-131.1, 26.7) * mm});
            skLineSegment(sketch, "E681", {"start": v(-131.1, 26.7) * mm, "end": v(-132.17, 27.38) * mm});
            skLineSegment(sketch, "E682", {"start": v(-132.17, 27.38) * mm, "end": v(-132.7, 27.74) * mm});
            skLineSegment(sketch, "E683", {"start": v(-132.7, 27.74) * mm, "end": v(-132.35, 29.3) * mm});
            skLineSegment(sketch, "E684", {"start": v(-132.35, 29.3) * mm, "end": v(-131.71, 29.4) * mm});
            skLineSegment(sketch, "E685", {"start": v(-131.71, 29.4) * mm, "end": v(-130.44, 29.54) * mm});
            skLineSegment(sketch, "E686", {"start": v(-130.44, 29.54) * mm, "end": v(-129.81, 29.6) * mm});
            skLineSegment(sketch, "E687", {"start": v(-129.81, 29.6) * mm, "end": v(-129.41, 31.2) * mm});
            skLineSegment(sketch, "E688", {"start": v(-129.41, 31.2) * mm, "end": v(-129.94, 31.54) * mm});
            skLineSegment(sketch, "E689", {"start": v(-129.94, 31.54) * mm, "end": v(-131, 32.27) * mm});
            skLineSegment(sketch, "E690", {"start": v(-131, 32.27) * mm, "end": v(-131.52, 32.64) * mm});
            skLineSegment(sketch, "E691", {"start": v(-131.52, 32.64) * mm, "end": v(-131.1, 34.2) * mm});
            skLineSegment(sketch, "E692", {"start": v(-131.1, 34.2) * mm, "end": v(-130.45, 34.26) * mm});
            skLineSegment(sketch, "E693", {"start": v(-130.45, 34.26) * mm, "end": v(-129.18, 34.35) * mm});
            skLineSegment(sketch, "E694", {"start": v(-129.18, 34.35) * mm, "end": v(-128.55, 34.39) * mm});
            skLineSegment(sketch, "E695", {"start": v(-128.55, 34.39) * mm, "end": v(-128.09, 35.96) * mm});
            skLineSegment(sketch, "E696", {"start": v(-128.09, 35.96) * mm, "end": v(-128.6, 36.33) * mm});
            skLineSegment(sketch, "E697", {"start": v(-128.6, 36.33) * mm, "end": v(-129.62, 37.1) * mm});
            skLineSegment(sketch, "E698", {"start": v(-129.62, 37.1) * mm, "end": v(-130.13, 37.5) * mm});
            skLineSegment(sketch, "E699", {"start": v(-130.13, 37.5) * mm, "end": v(-129.65, 39.03) * mm});
            skLineSegment(sketch, "E700", {"start": v(-129.65, 39.03) * mm, "end": v(-129, 39.07) * mm});
            skLineSegment(sketch, "E701", {"start": v(-129, 39.07) * mm, "end": v(-127.73, 39.11) * mm});
            skLineSegment(sketch, "E702", {"start": v(-127.73, 39.11) * mm, "end": v(-127.1, 39.12) * mm});
            skLineSegment(sketch, "E703", {"start": v(-127.1, 39.12) * mm, "end": v(-126.57, 40.68) * mm});
            skLineSegment(sketch, "E704", {"start": v(-126.57, 40.68) * mm, "end": v(-127.07, 41.07) * mm});
            skLineSegment(sketch, "E705", {"start": v(-127.07, 41.07) * mm, "end": v(-128.06, 41.87) * mm});
            skLineSegment(sketch, "E706", {"start": v(-128.06, 41.87) * mm, "end": v(-128.55, 42.29) * mm});
            skLineSegment(sketch, "E707", {"start": v(-128.55, 42.29) * mm, "end": v(-128, 43.8) * mm});
            skLineSegment(sketch, "E708", {"start": v(-128, 43.8) * mm, "end": v(-127.37, 43.82) * mm});
            skLineSegment(sketch, "E709", {"start": v(-127.37, 43.82) * mm, "end": v(-126.09, 43.81) * mm});
            skLineSegment(sketch, "E710", {"start": v(-126.09, 43.81) * mm, "end": v(-125.46, 43.8) * mm});
            skLineSegment(sketch, "E711", {"start": v(-125.46, 43.8) * mm, "end": v(-124.87, 45.33) * mm});
            skLineSegment(sketch, "E712", {"start": v(-124.87, 45.33) * mm, "end": v(-125.36, 45.74) * mm});
            skLineSegment(sketch, "E713", {"start": v(-125.36, 45.74) * mm, "end": v(-126.31, 46.58) * mm});
            skLineSegment(sketch, "E714", {"start": v(-126.31, 46.58) * mm, "end": v(-126.79, 47.02) * mm});
            skLineSegment(sketch, "E715", {"start": v(-126.79, 47.02) * mm, "end": v(-126.18, 48.51) * mm});
            skLineSegment(sketch, "E716", {"start": v(-126.18, 48.51) * mm, "end": v(-125.54, 48.5) * mm});
            skLineSegment(sketch, "E717", {"start": v(-125.54, 48.5) * mm, "end": v(-124.27, 48.44) * mm});
            skLineSegment(sketch, "E718", {"start": v(-124.27, 48.44) * mm, "end": v(-123.63, 48.4) * mm});
            skLineSegment(sketch, "E719", {"start": v(-123.63, 48.4) * mm, "end": v(-122.99, 49.91) * mm});
            skLineSegment(sketch, "E720", {"start": v(-122.99, 49.91) * mm, "end": v(-123.46, 50.34) * mm});
            skLineSegment(sketch, "E721", {"start": v(-123.46, 50.34) * mm, "end": v(-124.38, 51.22) * mm});
            skLineSegment(sketch, "E722", {"start": v(-124.38, 51.22) * mm, "end": v(-124.84, 51.67) * mm});
            skLineSegment(sketch, "E723", {"start": v(-124.84, 51.67) * mm, "end": v(-124.18, 53.14) * mm});
            skLineSegment(sketch, "E724", {"start": v(-124.18, 53.14) * mm, "end": v(-123.53, 53.1) * mm});
            skLineSegment(sketch, "E725", {"start": v(-123.53, 53.1) * mm, "end": v(-122.26, 53) * mm});
            skLineSegment(sketch, "E726", {"start": v(-122.26, 53) * mm, "end": v(-121.63, 52.93) * mm});
            skLineSegment(sketch, "E727", {"start": v(-121.63, 52.93) * mm, "end": v(-120.93, 54.41) * mm});
            skLineSegment(sketch, "E728", {"start": v(-120.93, 54.41) * mm, "end": v(-121.38, 54.86) * mm});
            skLineSegment(sketch, "E729", {"start": v(-121.38, 54.86) * mm, "end": v(-122.27, 55.78) * mm});
            skLineSegment(sketch, "E730", {"start": v(-122.27, 55.78) * mm, "end": v(-122.7, 56.25) * mm});
            skLineSegment(sketch, "E731", {"start": v(-122.7, 56.25) * mm, "end": v(-121.99, 57.69) * mm});
            skLineSegment(sketch, "E732", {"start": v(-121.99, 57.69) * mm, "end": v(-121.35, 57.62) * mm});
            skLineSegment(sketch, "E733", {"start": v(-121.35, 57.62) * mm, "end": v(-120.08, 57.47) * mm});
            skLineSegment(sketch, "E734", {"start": v(-120.08, 57.47) * mm, "end": v(-119.45, 57.38) * mm});
            skLineSegment(sketch, "E735", {"start": v(-119.45, 57.38) * mm, "end": v(-118.7, 58.83) * mm});
            skLineSegment(sketch, "E736", {"start": v(-118.7, 58.83) * mm, "end": v(-119.12, 59.3) * mm});
            skLineSegment(sketch, "E737", {"start": v(-119.12, 59.3) * mm, "end": v(-119.97, 60.25) * mm});
            skLineSegment(sketch, "E738", {"start": v(-119.97, 60.25) * mm, "end": v(-120.4, 60.73) * mm});
            skLineSegment(sketch, "E739", {"start": v(-120.4, 60.73) * mm, "end": v(-119.62, 62.15) * mm});
            skLineSegment(sketch, "E740", {"start": v(-119.62, 62.15) * mm, "end": v(-118.98, 62.06) * mm});
            skLineSegment(sketch, "E741", {"start": v(-118.98, 62.06) * mm, "end": v(-117.72, 61.85) * mm});
            skLineSegment(sketch, "E742", {"start": v(-117.72, 61.85) * mm, "end": v(-117.1, 61.73) * mm});
            skLineSegment(sketch, "E743", {"start": v(-117.1, 61.73) * mm, "end": v(-116.28, 63.16) * mm});
            skLineSegment(sketch, "E744", {"start": v(-116.28, 63.16) * mm, "end": v(-116.7, 63.64) * mm});
            skLineSegment(sketch, "E745", {"start": v(-116.7, 63.64) * mm, "end": v(-117.5, 64.62) * mm});
            skLineSegment(sketch, "E746", {"start": v(-117.5, 64.62) * mm, "end": v(-117.9, 65.13) * mm});
            skLineSegment(sketch, "E747", {"start": v(-117.9, 65.13) * mm, "end": v(-117.07, 66.5) * mm});
            skLineSegment(sketch, "E748", {"start": v(-117.07, 66.5) * mm, "end": v(-116.44, 66.4) * mm});
            skLineSegment(sketch, "E749", {"start": v(-116.44, 66.4) * mm, "end": v(-115.2, 66.13) * mm});
            skLineSegment(sketch, "E750", {"start": v(-115.2, 66.13) * mm, "end": v(-114.57, 66) * mm});
            skLineSegment(sketch, "E751", {"start": v(-114.57, 66) * mm, "end": v(-113.7, 67.38) * mm});
            skLineSegment(sketch, "E752", {"start": v(-113.7, 67.38) * mm, "end": v(-114.1, 67.88) * mm});
            skLineSegment(sketch, "E753", {"start": v(-114.1, 67.88) * mm, "end": v(-114.87, 68.9) * mm});
            skLineSegment(sketch, "E754", {"start": v(-114.87, 68.9) * mm, "end": v(-115.25, 69.42) * mm});
            skLineSegment(sketch, "E755", {"start": v(-115.25, 69.42) * mm, "end": v(-114.36, 70.76) * mm});
            skLineSegment(sketch, "E756", {"start": v(-114.36, 70.76) * mm, "end": v(-113.73, 70.62) * mm});
            skLineSegment(sketch, "E757", {"start": v(-113.73, 70.62) * mm, "end": v(-112.5, 70.32) * mm});
            skLineSegment(sketch, "E758", {"start": v(-112.5, 70.32) * mm, "end": v(-111.88, 70.15) * mm});
            skLineSegment(sketch, "E759", {"start": v(-111.88, 70.15) * mm, "end": v(-110.95, 71.5) * mm});
            skLineSegment(sketch, "E760", {"start": v(-110.95, 71.5) * mm, "end": v(-111.33, 72.02) * mm});
            skLineSegment(sketch, "E761", {"start": v(-111.33, 72.02) * mm, "end": v(-112.06, 73.06) * mm});
            skLineSegment(sketch, "E762", {"start": v(-112.06, 73.06) * mm, "end": v(-112.42, 73.6) * mm});
            skLineSegment(sketch, "E763", {"start": v(-112.42, 73.6) * mm, "end": v(-111.48, 74.9) * mm});
            skLineSegment(sketch, "E764", {"start": v(-111.48, 74.9) * mm, "end": v(-110.86, 74.74) * mm});
            skLineSegment(sketch, "E765", {"start": v(-110.86, 74.74) * mm, "end": v(-109.64, 74.39) * mm});
            skLineSegment(sketch, "E766", {"start": v(-109.64, 74.39) * mm, "end": v(-109.03, 74.2) * mm});
            skLineSegment(sketch, "E767", {"start": v(-109.03, 74.2) * mm, "end": v(-108.05, 75.52) * mm});
            skLineSegment(sketch, "E768", {"start": v(-108.05, 75.52) * mm, "end": v(-108.4, 76.04) * mm});
            skLineSegment(sketch, "E769", {"start": v(-108.4, 76.04) * mm, "end": v(-109.1, 77.12) * mm});
            skLineSegment(sketch, "E770", {"start": v(-109.1, 77.12) * mm, "end": v(-109.43, 77.66) * mm});
            skLineSegment(sketch, "E771", {"start": v(-109.43, 77.66) * mm, "end": v(-108.44, 78.94) * mm});
            skLineSegment(sketch, "E772", {"start": v(-108.44, 78.94) * mm, "end": v(-107.83, 78.75) * mm});
            skLineSegment(sketch, "E773", {"start": v(-107.83, 78.75) * mm, "end": v(-106.62, 78.34) * mm});
            skLineSegment(sketch, "E774", {"start": v(-106.62, 78.34) * mm, "end": v(-106.02, 78.13) * mm});
            skLineSegment(sketch, "E775", {"start": v(-106.02, 78.13) * mm, "end": v(-104.99, 79.4) * mm});
            skLineSegment(sketch, "E776", {"start": v(-104.99, 79.4) * mm, "end": v(-105.32, 79.95) * mm});
            skLineSegment(sketch, "E777", {"start": v(-105.32, 79.95) * mm, "end": v(-105.97, 81.05) * mm});
            skLineSegment(sketch, "E778", {"start": v(-105.97, 81.05) * mm, "end": v(-106.28, 81.6) * mm});
            skLineSegment(sketch, "E779", {"start": v(-106.28, 81.6) * mm, "end": v(-105.25, 82.84) * mm});
            skLineSegment(sketch, "E780", {"start": v(-105.25, 82.84) * mm, "end": v(-104.64, 82.63) * mm});
            skLineSegment(sketch, "E781", {"start": v(-104.64, 82.63) * mm, "end": v(-103.45, 82.18) * mm});
            skLineSegment(sketch, "E782", {"start": v(-103.45, 82.18) * mm, "end": v(-102.86, 81.94) * mm});
            skLineSegment(sketch, "E783", {"start": v(-102.86, 81.94) * mm, "end": v(-101.77, 83.18) * mm});
            skLineSegment(sketch, "E784", {"start": v(-101.77, 83.18) * mm, "end": v(-102.09, 83.73) * mm});
            skLineSegment(sketch, "E785", {"start": v(-102.09, 83.73) * mm, "end": v(-102.7, 84.85) * mm});
            skLineSegment(sketch, "E786", {"start": v(-102.7, 84.85) * mm, "end": v(-102.98, 85.43) * mm});
            skLineSegment(sketch, "E787", {"start": v(-102.98, 85.43) * mm, "end": v(-101.9, 86.62) * mm});
            skLineSegment(sketch, "E788", {"start": v(-101.9, 86.62) * mm, "end": v(-101.3, 86.38) * mm});
            skLineSegment(sketch, "E789", {"start": v(-101.3, 86.38) * mm, "end": v(-100.12, 85.88) * mm});
            skLineSegment(sketch, "E790", {"start": v(-100.12, 85.88) * mm, "end": v(-99.55, 85.62) * mm});
            skLineSegment(sketch, "E791", {"start": v(-99.55, 85.62) * mm, "end": v(-98.42, 86.82) * mm});
            skLineSegment(sketch, "E792", {"start": v(-98.42, 86.82) * mm, "end": v(-98.7, 87.38) * mm});
            skLineSegment(sketch, "E793", {"start": v(-98.7, 87.38) * mm, "end": v(-99.26, 88.53) * mm});
            skLineSegment(sketch, "E794", {"start": v(-99.26, 88.53) * mm, "end": v(-99.53, 89.11) * mm});
            skLineSegment(sketch, "E795", {"start": v(-99.53, 89.11) * mm, "end": v(-98.4, 90.26) * mm});
            skLineSegment(sketch, "E796", {"start": v(-98.4, 90.26) * mm, "end": v(-97.81, 90) * mm});
            skLineSegment(sketch, "E797", {"start": v(-97.81, 90) * mm, "end": v(-96.66, 89.46) * mm});
            skLineSegment(sketch, "E798", {"start": v(-96.66, 89.46) * mm, "end": v(-96.1, 89.17) * mm});
            skLineSegment(sketch, "E799", {"start": v(-96.1, 89.17) * mm, "end": v(-94.91, 90.32) * mm});
            skLineSegment(sketch, "E800", {"start": v(-94.91, 90.32) * mm, "end": v(-95.18, 90.9) * mm});
            skLineSegment(sketch, "E801", {"start": v(-95.18, 90.9) * mm, "end": v(-95.7, 92.06) * mm});
            skLineSegment(sketch, "E802", {"start": v(-95.7, 92.06) * mm, "end": v(-95.94, 92.66) * mm});
            skLineSegment(sketch, "E803", {"start": v(-95.94, 92.66) * mm, "end": v(-94.77, 93.76) * mm});
            skLineSegment(sketch, "E804", {"start": v(-94.77, 93.76) * mm, "end": v(-94.19, 93.47) * mm});
            skLineSegment(sketch, "E805", {"start": v(-94.19, 93.47) * mm, "end": v(-93.06, 92.89) * mm});
            skLineSegment(sketch, "E806", {"start": v(-93.06, 92.89) * mm, "end": v(-92.5, 92.58) * mm});
            skLineSegment(sketch, "E807", {"start": v(-92.5, 92.58) * mm, "end": v(-91.28, 93.68) * mm});
            skLineSegment(sketch, "E808", {"start": v(-91.28, 93.68) * mm, "end": v(-91.52, 94.27) * mm});
            skLineSegment(sketch, "E809", {"start": v(-91.52, 94.27) * mm, "end": v(-92, 95.45) * mm});
            skLineSegment(sketch, "E810", {"start": v(-92, 95.45) * mm, "end": v(-92.21, 96.06) * mm});
            skLineSegment(sketch, "E811", {"start": v(-92.21, 96.06) * mm, "end": v(-91, 97.11) * mm});
            skLineSegment(sketch, "E812", {"start": v(-91, 97.11) * mm, "end": v(-90.43, 96.8) * mm});
            skLineSegment(sketch, "E813", {"start": v(-90.43, 96.8) * mm, "end": v(-89.32, 96.17) * mm});
            skLineSegment(sketch, "E814", {"start": v(-89.32, 96.17) * mm, "end": v(-88.78, 95.85) * mm});
            skLineSegment(sketch, "E815", {"start": v(-88.78, 95.85) * mm, "end": v(-87.51, 96.9) * mm});
            skLineSegment(sketch, "E816", {"start": v(-87.51, 96.9) * mm, "end": v(-87.73, 97.5) * mm});
            skLineSegment(sketch, "E817", {"start": v(-87.73, 97.5) * mm, "end": v(-88.15, 98.7) * mm});
            skLineSegment(sketch, "E818", {"start": v(-88.15, 98.7) * mm, "end": v(-88.35, 99.3) * mm});
            skLineSegment(sketch, "E819", {"start": v(-88.35, 99.3) * mm, "end": v(-87.1, 100.31) * mm});
            skLineSegment(sketch, "E820", {"start": v(-87.1, 100.31) * mm, "end": v(-86.54, 99.99) * mm});
            skLineSegment(sketch, "E821", {"start": v(-86.54, 99.99) * mm, "end": v(-85.46, 99.3) * mm});
            skLineSegment(sketch, "E822", {"start": v(-85.46, 99.3) * mm, "end": v(-84.93, 98.96) * mm});
            skLineSegment(sketch, "E823", {"start": v(-84.93, 98.96) * mm, "end": v(-83.62, 99.96) * mm});
            skLineSegment(sketch, "E824", {"start": v(-83.62, 99.96) * mm, "end": v(-83.82, 100.56) * mm});
            skLineSegment(sketch, "E825", {"start": v(-83.82, 100.56) * mm, "end": v(-84.2, 101.78) * mm});
            skLineSegment(sketch, "E826", {"start": v(-84.2, 101.78) * mm, "end": v(-84.37, 102.4) * mm});
            skLineSegment(sketch, "E827", {"start": v(-84.37, 102.4) * mm, "end": v(-83.07, 103.36) * mm});
            skLineSegment(sketch, "E828", {"start": v(-83.07, 103.36) * mm, "end": v(-82.53, 103) * mm});
            skLineSegment(sketch, "E829", {"start": v(-82.53, 103) * mm, "end": v(-81.47, 102.3) * mm});
            skLineSegment(sketch, "E830", {"start": v(-81.47, 102.3) * mm, "end": v(-80.96, 101.92) * mm});
            skLineSegment(sketch, "E831", {"start": v(-80.96, 101.92) * mm, "end": v(-79.61, 102.87) * mm});
            skLineSegment(sketch, "E832", {"start": v(-79.61, 102.87) * mm, "end": v(-79.79, 103.48) * mm});
            skLineSegment(sketch, "E833", {"start": v(-79.79, 103.48) * mm, "end": v(-80.11, 104.71) * mm});
            skLineSegment(sketch, "E834", {"start": v(-80.11, 104.71) * mm, "end": v(-80.26, 105.34) * mm});
            skLineSegment(sketch, "E835", {"start": v(-80.26, 105.34) * mm, "end": v(-78.92, 106.24) * mm});
            skLineSegment(sketch, "E836", {"start": v(-78.92, 106.24) * mm, "end": v(-78.4, 105.87) * mm});
            skLineSegment(sketch, "E837", {"start": v(-78.4, 105.87) * mm, "end": v(-77.37, 105.11) * mm});
            skLineSegment(sketch, "E838", {"start": v(-77.37, 105.11) * mm, "end": v(-76.87, 104.72) * mm});
            skLineSegment(sketch, "E839", {"start": v(-76.87, 104.72) * mm, "end": v(-75.5, 105.62) * mm});
            skLineSegment(sketch, "E840", {"start": v(-75.5, 105.62) * mm, "end": v(-75.64, 106.23) * mm});
            skLineSegment(sketch, "E841", {"start": v(-75.64, 106.23) * mm, "end": v(-75.92, 107.48) * mm});
            skLineSegment(sketch, "E842", {"start": v(-75.92, 107.48) * mm, "end": v(-76.04, 108.11) * mm});
            skLineSegment(sketch, "E843", {"start": v(-76.04, 108.11) * mm, "end": v(-74.67, 108.96) * mm});
            skLineSegment(sketch, "E844", {"start": v(-74.67, 108.96) * mm, "end": v(-74.16, 108.57) * mm});
            skLineSegment(sketch, "E845", {"start": v(-74.16, 108.57) * mm, "end": v(-73.17, 107.77) * mm});
            skLineSegment(sketch, "E846", {"start": v(-73.17, 107.77) * mm, "end": v(-72.68, 107.36) * mm});
            skLineSegment(sketch, "E847", {"start": v(-72.68, 107.36) * mm, "end": v(-71.27, 108.2) * mm});
            skLineSegment(sketch, "E848", {"start": v(-71.27, 108.2) * mm, "end": v(-71.4, 108.82) * mm});
            skLineSegment(sketch, "E849", {"start": v(-71.4, 108.82) * mm, "end": v(-71.62, 110.08) * mm});
            skLineSegment(sketch, "E850", {"start": v(-71.62, 110.08) * mm, "end": v(-71.72, 110.71) * mm});
            skLineSegment(sketch, "E851", {"start": v(-71.72, 110.71) * mm, "end": v(-70.32, 111.5) * mm});
            skLineSegment(sketch, "E852", {"start": v(-70.32, 111.5) * mm, "end": v(-69.82, 111.1) * mm});
            skLineSegment(sketch, "E853", {"start": v(-69.82, 111.1) * mm, "end": v(-68.86, 110.26) * mm});
            skLineSegment(sketch, "E854", {"start": v(-68.86, 110.26) * mm, "end": v(-68.39, 109.83) * mm});
            skLineSegment(sketch, "E855", {"start": v(-68.39, 109.83) * mm, "end": v(-66.94, 110.61) * mm});
            skLineSegment(sketch, "E856", {"start": v(-66.94, 110.61) * mm, "end": v(-67.05, 111.24) * mm});
            skLineSegment(sketch, "E857", {"start": v(-67.05, 111.24) * mm, "end": v(-67.22, 112.5) * mm});
            skLineSegment(sketch, "E858", {"start": v(-67.22, 112.5) * mm, "end": v(-67.3, 113.14) * mm});
            skLineSegment(sketch, "E859", {"start": v(-67.3, 113.14) * mm, "end": v(-65.86, 113.88) * mm});
            skLineSegment(sketch, "E860", {"start": v(-65.86, 113.88) * mm, "end": v(-65.38, 113.45) * mm});
            skLineSegment(sketch, "E861", {"start": v(-65.38, 113.45) * mm, "end": v(-64.45, 112.58) * mm});
            skLineSegment(sketch, "E862", {"start": v(-64.45, 112.58) * mm, "end": v(-64, 112.13) * mm});
            skLineSegment(sketch, "E863", {"start": v(-64, 112.13) * mm, "end": v(-62.53, 112.86) * mm});
            skLineSegment(sketch, "E864", {"start": v(-62.53, 112.86) * mm, "end": v(-62.6, 113.48) * mm});
            skLineSegment(sketch, "E865", {"start": v(-62.6, 113.48) * mm, "end": v(-62.73, 114.76) * mm});
            skLineSegment(sketch, "E866", {"start": v(-62.73, 114.76) * mm, "end": v(-62.78, 115.4) * mm});
            skLineSegment(sketch, "E867", {"start": v(-62.78, 115.4) * mm, "end": v(-61.32, 116.08) * mm});
            skLineSegment(sketch, "E868", {"start": v(-61.32, 116.08) * mm, "end": v(-60.86, 115.63) * mm});
            skLineSegment(sketch, "E869", {"start": v(-60.86, 115.63) * mm, "end": v(-59.96, 114.72) * mm});
            skLineSegment(sketch, "E870", {"start": v(-59.96, 114.72) * mm, "end": v(-59.53, 114.26) * mm});
            skLineSegment(sketch, "E871", {"start": v(-59.53, 114.26) * mm, "end": v(-58.03, 114.92) * mm});
            skLineSegment(sketch, "E872", {"start": v(-58.03, 114.92) * mm, "end": v(-58.08, 115.55) * mm});
            skLineSegment(sketch, "E873", {"start": v(-58.08, 115.55) * mm, "end": v(-58.15, 116.83) * mm});
            skLineSegment(sketch, "E874", {"start": v(-58.15, 116.83) * mm, "end": v(-58.18, 117.47) * mm});
            skLineSegment(sketch, "E875", {"start": v(-58.18, 117.47) * mm, "end": v(-56.69, 118.1) * mm});
            skLineSegment(sketch, "E876", {"start": v(-56.69, 118.1) * mm, "end": v(-56.25, 117.63) * mm});
            skLineSegment(sketch, "E877", {"start": v(-56.25, 117.63) * mm, "end": v(-55.4, 116.68) * mm});
            skLineSegment(sketch, "E878", {"start": v(-55.4, 116.68) * mm, "end": v(-54.98, 116.2) * mm});
            skLineSegment(sketch, "E879", {"start": v(-54.98, 116.2) * mm, "end": v(-53.45, 116.8) * mm});
            skLineSegment(sketch, "E880", {"start": v(-53.45, 116.8) * mm, "end": v(-53.47, 117.44) * mm});
            skLineSegment(sketch, "E881", {"start": v(-53.47, 117.44) * mm, "end": v(-53.5, 118.72) * mm});
            skLineSegment(sketch, "E882", {"start": v(-53.5, 118.72) * mm, "end": v(-53.5, 119.36) * mm});
            skLineSegment(sketch, "E883", {"start": v(-53.5, 119.36) * mm, "end": v(-51.99, 119.92) * mm});
            skLineSegment(sketch, "E884", {"start": v(-51.99, 119.92) * mm, "end": v(-51.56, 119.44) * mm});
            skLineSegment(sketch, "E885", {"start": v(-51.56, 119.44) * mm, "end": v(-50.74, 118.46) * mm});
            skLineSegment(sketch, "E886", {"start": v(-50.74, 118.46) * mm, "end": v(-50.35, 117.96) * mm});
            skLineSegment(sketch, "E887", {"start": v(-50.35, 117.96) * mm, "end": v(-48.8, 118.5) * mm});
            skLineSegment(sketch, "E888", {"start": v(-48.8, 118.5) * mm, "end": v(-48.8, 119.14) * mm});
            skLineSegment(sketch, "E889", {"start": v(-48.8, 119.14) * mm, "end": v(-48.77, 120.42) * mm});
            skLineSegment(sketch, "E890", {"start": v(-48.77, 120.42) * mm, "end": v(-48.74, 121.06) * mm});
            skLineSegment(sketch, "E891", {"start": v(-48.74, 121.06) * mm, "end": v(-47.21, 121.57) * mm});
            skLineSegment(sketch, "E892", {"start": v(-47.21, 121.57) * mm, "end": v(-46.8, 121.07) * mm});
            skLineSegment(sketch, "E893", {"start": v(-46.8, 121.07) * mm, "end": v(-46.03, 120.05) * mm});
            skLineSegment(sketch, "E894", {"start": v(-46.03, 120.05) * mm, "end": v(-45.65, 119.54) * mm});
            skLineSegment(sketch, "E895", {"start": v(-45.65, 119.54) * mm, "end": v(-44.08, 120.03) * mm});
            skLineSegment(sketch, "E896", {"start": v(-44.08, 120.03) * mm, "end": v(-44.06, 120.66) * mm});
            skLineSegment(sketch, "E897", {"start": v(-44.06, 120.66) * mm, "end": v(-43.98, 121.93) * mm});
            skLineSegment(sketch, "E898", {"start": v(-43.98, 121.93) * mm, "end": v(-43.93, 122.58) * mm});
            skLineSegment(sketch, "E899", {"start": v(-43.93, 122.58) * mm, "end": v(-42.38, 123.02) * mm});
            skLineSegment(sketch, "E900", {"start": v(-42.38, 123.02) * mm, "end": v(-42, 122.5) * mm});
            skLineSegment(sketch, "E901", {"start": v(-42, 122.5) * mm, "end": v(-41.26, 121.46) * mm});
            skLineSegment(sketch, "E902", {"start": v(-41.26, 121.46) * mm, "end": v(-40.9, 120.94) * mm});
            skLineSegment(sketch, "E903", {"start": v(-40.9, 120.94) * mm, "end": v(-39.31, 121.36) * mm});
            skLineSegment(sketch, "E904", {"start": v(-39.31, 121.36) * mm, "end": v(-39.26, 121.99) * mm});
            skLineSegment(sketch, "E905", {"start": v(-39.26, 121.99) * mm, "end": v(-39.14, 123.26) * mm});
            skLineSegment(sketch, "E906", {"start": v(-39.14, 123.26) * mm, "end": v(-39.06, 123.9) * mm});
            skLineSegment(sketch, "E907", {"start": v(-39.06, 123.9) * mm, "end": v(-37.5, 124.28) * mm});
            skLineSegment(sketch, "E908", {"start": v(-37.5, 124.28) * mm, "end": v(-37.13, 123.75) * mm});
            skLineSegment(sketch, "E909", {"start": v(-37.13, 123.75) * mm, "end": v(-36.43, 122.68) * mm});
            skLineSegment(sketch, "E910", {"start": v(-36.43, 122.68) * mm, "end": v(-36.1, 122.14) * mm});
            skLineSegment(sketch, "E911", {"start": v(-36.1, 122.14) * mm, "end": v(-34.5, 122.5) * mm});
            skLineSegment(sketch, "E912", {"start": v(-34.5, 122.5) * mm, "end": v(-34.42, 123.13) * mm});
            skLineSegment(sketch, "E913", {"start": v(-34.42, 123.13) * mm, "end": v(-34.24, 124.4) * mm});
            skLineSegment(sketch, "E914", {"start": v(-34.24, 124.4) * mm, "end": v(-34.14, 125.03) * mm});
            skLineSegment(sketch, "E915", {"start": v(-34.14, 125.03) * mm, "end": v(-32.56, 125.35) * mm});
            skLineSegment(sketch, "E916", {"start": v(-32.56, 125.35) * mm, "end": v(-32.22, 124.8) * mm});
            skLineSegment(sketch, "E917", {"start": v(-32.22, 124.8) * mm, "end": v(-31.56, 123.7) * mm});
            skLineSegment(sketch, "E918", {"start": v(-31.56, 123.7) * mm, "end": v(-31.25, 123.16) * mm});
            skLineSegment(sketch, "E919", {"start": v(-31.25, 123.16) * mm, "end": v(-29.63, 123.45) * mm});
            skLineSegment(sketch, "E920", {"start": v(-29.63, 123.45) * mm, "end": v(-29.54, 124.07) * mm});
            skLineSegment(sketch, "E921", {"start": v(-29.54, 124.07) * mm, "end": v(-29.3, 125.33) * mm});
            skLineSegment(sketch, "E922", {"start": v(-29.3, 125.33) * mm, "end": v(-29.18, 125.96) * mm});
            skLineSegment(sketch, "E923", {"start": v(-29.18, 125.96) * mm, "end": v(-27.59, 126.22) * mm});
            skLineSegment(sketch, "E924", {"start": v(-27.59, 126.22) * mm, "end": v(-27.27, 125.66) * mm});
            skLineSegment(sketch, "E925", {"start": v(-27.27, 125.66) * mm, "end": v(-26.66, 124.54) * mm});
            skLineSegment(sketch, "E926", {"start": v(-26.66, 124.54) * mm, "end": v(-26.37, 123.98) * mm});
            skLineSegment(sketch, "E927", {"start": v(-26.37, 123.98) * mm, "end": v(-24.74, 124.2) * mm});
            skLineSegment(sketch, "E928", {"start": v(-24.74, 124.2) * mm, "end": v(-24.62, 124.83) * mm});
            skLineSegment(sketch, "E929", {"start": v(-24.62, 124.83) * mm, "end": v(-24.34, 126.07) * mm});
            skLineSegment(sketch, "E930", {"start": v(-24.34, 126.07) * mm, "end": v(-24.19, 126.7) * mm});
            skLineSegment(sketch, "E931", {"start": v(-24.19, 126.7) * mm, "end": v(-22.59, 126.9) * mm});
            skLineSegment(sketch, "E932", {"start": v(-22.59, 126.9) * mm, "end": v(-22.29, 126.32) * mm});
            skLineSegment(sketch, "E933", {"start": v(-22.29, 126.32) * mm, "end": v(-21.72, 125.18) * mm});
            skLineSegment(sketch, "E934", {"start": v(-21.72, 125.18) * mm, "end": v(-21.45, 124.6) * mm});
            skLineSegment(sketch, "E935", {"start": v(-21.45, 124.6) * mm, "end": v(-19.82, 124.77) * mm});
            skLineSegment(sketch, "E936", {"start": v(-19.82, 124.77) * mm, "end": v(-19.67, 125.39) * mm});
            skLineSegment(sketch, "E937", {"start": v(-19.67, 125.39) * mm, "end": v(-19.35, 126.62) * mm});
            skLineSegment(sketch, "E938", {"start": v(-19.35, 126.62) * mm, "end": v(-19.17, 127.24) * mm});
            skLineSegment(sketch, "E939", {"start": v(-19.17, 127.24) * mm, "end": v(-17.56, 127.37) * mm});
            skLineSegment(sketch, "E940", {"start": v(-17.56, 127.37) * mm, "end": v(-17.29, 126.79) * mm});
            skLineSegment(sketch, "E941", {"start": v(-17.29, 126.79) * mm, "end": v(-16.77, 125.62) * mm});
            skLineSegment(sketch, "E942", {"start": v(-16.77, 125.62) * mm, "end": v(-16.52, 125.04) * mm});
            skLineSegment(sketch, "E943", {"start": v(-16.52, 125.04) * mm, "end": v(-14.88, 125.14) * mm});
            skLineSegment(sketch, "E944", {"start": v(-14.88, 125.14) * mm, "end": v(-14.7, 125.75) * mm});
            skLineSegment(sketch, "E945", {"start": v(-14.7, 125.75) * mm, "end": v(-14.33, 126.97) * mm});
            skLineSegment(sketch, "E946", {"start": v(-14.33, 126.97) * mm, "end": v(-14.13, 127.58) * mm});
            skLineSegment(sketch, "E947", {"start": v(-14.13, 127.58) * mm, "end": v(-12.52, 127.65) * mm});
            skLineSegment(sketch, "E948", {"start": v(-12.52, 127.65) * mm, "end": v(-12.27, 127.05) * mm});
            skLineSegment(sketch, "E949", {"start": v(-12.27, 127.05) * mm, "end": v(-11.8, 125.87) * mm});
            skLineSegment(sketch, "E950", {"start": v(-11.8, 125.87) * mm, "end": v(-11.57, 125.27) * mm});
            skLineSegment(sketch, "E951", {"start": v(-11.57, 125.27) * mm, "end": v(-9.93, 125.31) * mm});
            skLineSegment(sketch, "E952", {"start": v(-9.93, 125.31) * mm, "end": v(-9.74, 125.91) * mm});
            skLineSegment(sketch, "E953", {"start": v(-9.74, 125.91) * mm, "end": v(-9.31, 127.12) * mm});
            skLineSegment(sketch, "E954", {"start": v(-9.31, 127.12) * mm, "end": v(-9.09, 127.72) * mm});
            skLineSegment(sketch, "E955", {"start": v(-9.09, 127.72) * mm, "end": v(-7.48, 127.72) * mm});
            skLineSegment(sketch, "E956", {"start": v(-7.48, 127.72) * mm, "end": v(-7.25, 127.12) * mm});
            skLineSegment(sketch, "E957", {"start": v(-7.25, 127.12) * mm, "end": v(-6.82, 125.92) * mm});
            skLineSegment(sketch, "E958", {"start": v(-6.82, 125.92) * mm, "end": v(-6.62, 125.32) * mm});
            skLineSegment(sketch, "E959", {"start": v(-6.62, 125.32) * mm, "end": v(-4.98, 125.29) * mm});
            skLineSegment(sketch, "E960", {"start": v(-4.98, 125.29) * mm, "end": v(-4.76, 125.88) * mm});
            skLineSegment(sketch, "E961", {"start": v(-4.76, 125.88) * mm, "end": v(-4.3, 127.07) * mm});
            skLineSegment(sketch, "E962", {"start": v(-4.3, 127.07) * mm, "end": v(-4.04, 127.66) * mm});
            skLineSegment(sketch, "E963", {"start": v(-4.04, 127.66) * mm, "end": v(-2.43, 127.6) * mm});
            skLineSegment(sketch, "E964", {"start": v(-2.43, 127.6) * mm, "end": v(-2.23, 127) * mm});
            skLineSegment(sketch, "E965", {"start": v(-2.23, 127) * mm, "end": v(-1.85, 125.77) * mm});
            skLineSegment(sketch, "E966", {"start": v(-1.85, 125.77) * mm, "end": v(-1.67, 125.16) * mm});
            skLineSegment(sketch, "E967", {"start": v(-1.67, 125.16) * mm, "end": v(-0.03, 125.07) * mm});
            skLineSegment(sketch, "E968", {"start": v(-0.03, 125.07) * mm, "end": v(0.21, 125.65) * mm});
            skLineSegment(sketch, "E969", {"start": v(0.21, 125.65) * mm, "end": v(0.73, 126.82) * mm});
            skLineSegment(sketch, "E970", {"start": v(0.73, 126.82) * mm, "end": v(1, 127.4) * mm});
            skLineSegment(sketch, "E971", {"start": v(1, 127.4) * mm, "end": v(2.6, 127.28) * mm});
            skLineSegment(sketch, "E972", {"start": v(2.6, 127.28) * mm, "end": v(2.79, 126.66) * mm});
            skLineSegment(sketch, "E973", {"start": v(2.79, 126.66) * mm, "end": v(3.12, 125.43) * mm});
            skLineSegment(sketch, "E974", {"start": v(3.12, 125.43) * mm, "end": v(3.27, 124.81) * mm});
            skLineSegment(sketch, "E975", {"start": v(3.27, 124.81) * mm, "end": v(4.9, 124.66) * mm});
            skLineSegment(sketch, "E976", {"start": v(4.9, 124.66) * mm, "end": v(5.17, 125.23) * mm});
            skLineSegment(sketch, "E977", {"start": v(5.17, 125.23) * mm, "end": v(5.73, 126.38) * mm});
            skLineSegment(sketch, "E978", {"start": v(5.73, 126.38) * mm, "end": v(6.03, 126.95) * mm});
            skLineSegment(sketch, "E979", {"start": v(6.03, 126.95) * mm, "end": v(7.63, 126.76) * mm});
            skLineSegment(sketch, "E980", {"start": v(7.63, 126.76) * mm, "end": v(7.78, 126.14) * mm});
            skLineSegment(sketch, "E981", {"start": v(7.78, 126.14) * mm, "end": v(8.06, 124.9) * mm});
            skLineSegment(sketch, "E982", {"start": v(8.06, 124.9) * mm, "end": v(8.19, 124.27) * mm});
            skLineSegment(sketch, "E983", {"start": v(8.19, 124.27) * mm, "end": v(9.82, 124.05) * mm});
            skLineSegment(sketch, "E984", {"start": v(9.82, 124.05) * mm, "end": v(10.1, 124.61) * mm});
            skLineSegment(sketch, "E985", {"start": v(10.1, 124.61) * mm, "end": v(10.71, 125.74) * mm});
            skLineSegment(sketch, "E986", {"start": v(10.71, 125.74) * mm, "end": v(11.03, 126.3) * mm});
            skLineSegment(sketch, "E987", {"start": v(11.03, 126.3) * mm, "end": v(12.62, 126.04) * mm});
            skLineSegment(sketch, "E988", {"start": v(12.62, 126.04) * mm, "end": v(12.75, 125.41) * mm});
            skLineSegment(sketch, "E989", {"start": v(12.75, 125.41) * mm, "end": v(12.99, 124.16) * mm});
            skLineSegment(sketch, "E990", {"start": v(12.99, 124.16) * mm, "end": v(13.09, 123.53) * mm});
            skLineSegment(sketch, "E991", {"start": v(13.09, 123.53) * mm, "end": v(14.7, 123.25) * mm});
            skLineSegment(sketch, "E992", {"start": v(14.7, 123.25) * mm, "end": v(15.01, 123.8) * mm});
            skLineSegment(sketch, "E993", {"start": v(15.01, 123.8) * mm, "end": v(15.67, 124.9) * mm});
            skLineSegment(sketch, "E994", {"start": v(15.67, 124.9) * mm, "end": v(16, 125.44) * mm});
            skLineSegment(sketch, "E995", {"start": v(16, 125.44) * mm, "end": v(17.59, 125.13) * mm});
            skLineSegment(sketch, "E996", {"start": v(17.59, 125.13) * mm, "end": v(17.7, 124.5) * mm});
            skLineSegment(sketch, "E997", {"start": v(17.7, 124.5) * mm, "end": v(17.87, 123.23) * mm});
            skLineSegment(sketch, "E998", {"start": v(17.87, 123.23) * mm, "end": v(17.95, 122.6) * mm});
            skLineSegment(sketch, "E999", {"start": v(17.95, 122.6) * mm, "end": v(19.56, 122.25) * mm});
            skLineSegment(sketch, "E1000", {"start": v(19.56, 122.25) * mm, "end": v(19.89, 122.8) * mm});
            skLineSegment(sketch, "E1001", {"start": v(19.89, 122.8) * mm, "end": v(20.58, 123.86) * mm});
            skLineSegment(sketch, "E1002", {"start": v(20.58, 123.86) * mm, "end": v(20.94, 124.4) * mm});
            skLineSegment(sketch, "E1003", {"start": v(20.94, 124.4) * mm, "end": v(22.5, 124.02) * mm});
            skLineSegment(sketch, "E1004", {"start": v(22.5, 124.02) * mm, "end": v(22.59, 123.38) * mm});
            skLineSegment(sketch, "E1005", {"start": v(22.59, 123.38) * mm, "end": v(22.72, 122.11) * mm});
            skLineSegment(sketch, "E1006", {"start": v(22.72, 122.11) * mm, "end": v(22.77, 121.48) * mm});
            skLineSegment(sketch, "E1007", {"start": v(22.77, 121.48) * mm, "end": v(24.36, 121.07) * mm});
            skLineSegment(sketch, "E1008", {"start": v(24.36, 121.07) * mm, "end": v(24.72, 121.6) * mm});
            skLineSegment(sketch, "E1009", {"start": v(24.72, 121.6) * mm, "end": v(25.45, 122.64) * mm});
            skLineSegment(sketch, "E1010", {"start": v(25.45, 122.64) * mm, "end": v(25.83, 123.15) * mm});
            skLineSegment(sketch, "E1011", {"start": v(25.83, 123.15) * mm, "end": v(27.39, 122.72) * mm});
            skLineSegment(sketch, "E1012", {"start": v(27.39, 122.72) * mm, "end": v(27.44, 122.08) * mm});
            skLineSegment(sketch, "E1013", {"start": v(27.44, 122.08) * mm, "end": v(27.52, 120.8) * mm});
            skLineSegment(sketch, "E1014", {"start": v(27.52, 120.8) * mm, "end": v(27.55, 120.17) * mm});
            skLineSegment(sketch, "E1015", {"start": v(27.55, 120.17) * mm, "end": v(29.12, 119.7) * mm});
            skLineSegment(sketch, "E1016", {"start": v(29.12, 119.7) * mm, "end": v(29.5, 120.2) * mm});
            skLineSegment(sketch, "E1017", {"start": v(29.5, 120.2) * mm, "end": v(30.27, 121.22) * mm});
            skLineSegment(sketch, "E1018", {"start": v(30.27, 121.22) * mm, "end": v(30.67, 121.72) * mm});
            skLineSegment(sketch, "E1019", {"start": v(30.67, 121.72) * mm, "end": v(32.2, 121.22) * mm});
            skLineSegment(sketch, "E1020", {"start": v(32.2, 121.22) * mm, "end": v(32.24, 120.58) * mm});
            skLineSegment(sketch, "E1021", {"start": v(32.24, 120.58) * mm, "end": v(32.27, 119.3) * mm});
            skLineSegment(sketch, "E1022", {"start": v(32.27, 119.3) * mm, "end": v(32.27, 118.67) * mm});
            skLineSegment(sketch, "E1023", {"start": v(32.27, 118.67) * mm, "end": v(33.82, 118.13) * mm});
            skLineSegment(sketch, "E1024", {"start": v(33.82, 118.13) * mm, "end": v(34.22, 118.63) * mm});
            skLineSegment(sketch, "E1025", {"start": v(34.22, 118.63) * mm, "end": v(35.03, 119.6) * mm});
            skLineSegment(sketch, "E1026", {"start": v(35.03, 119.6) * mm, "end": v(35.45, 120.1) * mm});
            skLineSegment(sketch, "E1027", {"start": v(35.45, 120.1) * mm, "end": v(36.96, 119.54) * mm});
            skLineSegment(sketch, "E1028", {"start": v(36.96, 119.54) * mm, "end": v(36.97, 118.9) * mm});
            skLineSegment(sketch, "E1029", {"start": v(36.97, 118.9) * mm, "end": v(36.95, 117.62) * mm});
            skLineSegment(sketch, "E1030", {"start": v(36.95, 117.62) * mm, "end": v(36.93, 116.98) * mm});
            skLineSegment(sketch, "E1031", {"start": v(36.93, 116.98) * mm, "end": v(38.46, 116.39) * mm});
            skLineSegment(sketch, "E1032", {"start": v(38.46, 116.39) * mm, "end": v(38.87, 116.87) * mm});
            skLineSegment(sketch, "E1033", {"start": v(38.87, 116.87) * mm, "end": v(39.72, 117.82) * mm});
            skLineSegment(sketch, "E1034", {"start": v(39.72, 117.82) * mm, "end": v(40.16, 118.28) * mm});
            skLineSegment(sketch, "E1035", {"start": v(40.16, 118.28) * mm, "end": v(41.65, 117.67) * mm});
            skLineSegment(sketch, "E1036", {"start": v(41.65, 117.67) * mm, "end": v(41.63, 117.02) * mm});
            skLineSegment(sketch, "E1037", {"start": v(41.63, 117.02) * mm, "end": v(41.56, 115.75) * mm});
            skLineSegment(sketch, "E1038", {"start": v(41.56, 115.75) * mm, "end": v(41.51, 115.12) * mm});
            skLineSegment(sketch, "E1039", {"start": v(41.51, 115.12) * mm, "end": v(43.02, 114.46) * mm});
            skLineSegment(sketch, "E1040", {"start": v(43.02, 114.46) * mm, "end": v(43.45, 114.92) * mm});
            skLineSegment(sketch, "E1041", {"start": v(43.45, 114.92) * mm, "end": v(44.34, 115.84) * mm});
            skLineSegment(sketch, "E1042", {"start": v(44.34, 115.84) * mm, "end": v(44.8, 116.29) * mm});
            skLineSegment(sketch, "E1043", {"start": v(44.8, 116.29) * mm, "end": v(46.26, 115.61) * mm});
            skLineSegment(sketch, "E1044", {"start": v(46.26, 115.61) * mm, "end": v(46.21, 114.97) * mm});
            skLineSegment(sketch, "E1045", {"start": v(46.21, 114.97) * mm, "end": v(46.1, 113.7) * mm});
            skLineSegment(sketch, "E1046", {"start": v(46.1, 113.7) * mm, "end": v(46.02, 113.07) * mm});
            skLineSegment(sketch, "E1047", {"start": v(46.02, 113.07) * mm, "end": v(47.5, 112.35) * mm});
            skLineSegment(sketch, "E1048", {"start": v(47.5, 112.35) * mm, "end": v(47.95, 112.8) * mm});
            skLineSegment(sketch, "E1049", {"start": v(47.95, 112.8) * mm, "end": v(48.88, 113.68) * mm});
            skLineSegment(sketch, "E1050", {"start": v(48.88, 113.68) * mm, "end": v(49.35, 114.1) * mm});
            skLineSegment(sketch, "E1051", {"start": v(49.35, 114.1) * mm, "end": v(50.79, 113.38) * mm});
            skLineSegment(sketch, "E1052", {"start": v(50.79, 113.38) * mm, "end": v(50.71, 112.74) * mm});
            skLineSegment(sketch, "E1053", {"start": v(50.71, 112.74) * mm, "end": v(50.55, 111.47) * mm});
            skLineSegment(sketch, "E1054", {"start": v(50.55, 111.47) * mm, "end": v(50.45, 110.85) * mm});
            skLineSegment(sketch, "E1055", {"start": v(50.45, 110.85) * mm, "end": v(51.9, 110.07) * mm});
            skLineSegment(sketch, "E1056", {"start": v(51.9, 110.07) * mm, "end": v(52.36, 110.5) * mm});
            skLineSegment(sketch, "E1057", {"start": v(52.36, 110.5) * mm, "end": v(53.32, 111.34) * mm});
            skLineSegment(sketch, "E1058", {"start": v(53.32, 111.34) * mm, "end": v(53.81, 111.75) * mm});
            skLineSegment(sketch, "E1059", {"start": v(53.81, 111.75) * mm, "end": v(55.22, 110.96) * mm});
            skLineSegment(sketch, "E1060", {"start": v(55.22, 110.96) * mm, "end": v(55.12, 110.33) * mm});
            skLineSegment(sketch, "E1061", {"start": v(55.12, 110.33) * mm, "end": v(54.9, 109.07) * mm});
            skLineSegment(sketch, "E1062", {"start": v(54.9, 109.07) * mm, "end": v(54.78, 108.45) * mm});
            skLineSegment(sketch, "E1063", {"start": v(54.78, 108.45) * mm, "end": v(56.2, 107.62) * mm});
            skLineSegment(sketch, "E1064", {"start": v(56.2, 107.62) * mm, "end": v(56.68, 108.03) * mm});
            skLineSegment(sketch, "E1065", {"start": v(56.68, 108.03) * mm, "end": v(57.67, 108.83) * mm});
            skLineSegment(sketch, "E1066", {"start": v(57.67, 108.83) * mm, "end": v(58.18, 109.22) * mm});
            skLineSegment(sketch, "E1067", {"start": v(58.18, 109.22) * mm, "end": v(59.55, 108.38) * mm});
            skLineSegment(sketch, "E1068", {"start": v(59.55, 108.38) * mm, "end": v(59.43, 107.75) * mm});
            skLineSegment(sketch, "E1069", {"start": v(59.43, 107.75) * mm, "end": v(59.16, 106.5) * mm});
            skLineSegment(sketch, "E1070", {"start": v(59.16, 106.5) * mm, "end": v(59.02, 105.88) * mm});
            skLineSegment(sketch, "E1071", {"start": v(59.02, 105.88) * mm, "end": v(60.4, 105) * mm});
            skLineSegment(sketch, "E1072", {"start": v(60.4, 105) * mm, "end": v(60.9, 105.39) * mm});
            skLineSegment(sketch, "E1073", {"start": v(60.9, 105.39) * mm, "end": v(61.92, 106.15) * mm});
            skLineSegment(sketch, "E1074", {"start": v(61.92, 106.15) * mm, "end": v(62.44, 106.52) * mm});
            skLineSegment(sketch, "E1075", {"start": v(62.44, 106.52) * mm, "end": v(63.78, 105.62) * mm});
            skLineSegment(sketch, "E1076", {"start": v(63.78, 105.62) * mm, "end": v(63.64, 105) * mm});
            skLineSegment(sketch, "E1077", {"start": v(63.64, 105) * mm, "end": v(63.32, 103.76) * mm});
            skLineSegment(sketch, "E1078", {"start": v(63.32, 103.76) * mm, "end": v(63.15, 103.15) * mm});
            skLineSegment(sketch, "E1079", {"start": v(63.15, 103.15) * mm, "end": v(64.5, 102.21) * mm});
            skLineSegment(sketch, "E1080", {"start": v(64.5, 102.21) * mm, "end": v(65, 102.58) * mm});
            skLineSegment(sketch, "E1081", {"start": v(65, 102.58) * mm, "end": v(66.06, 103.3) * mm});
            skLineSegment(sketch, "E1082", {"start": v(66.06, 103.3) * mm, "end": v(66.6, 103.65) * mm});
            skLineSegment(sketch, "E1083", {"start": v(66.6, 103.65) * mm, "end": v(67.9, 102.7) * mm});
            skLineSegment(sketch, "E1084", {"start": v(67.9, 102.7) * mm, "end": v(67.73, 102.09) * mm});
            skLineSegment(sketch, "E1085", {"start": v(67.73, 102.09) * mm, "end": v(67.36, 100.86) * mm});
            skLineSegment(sketch, "E1086", {"start": v(67.36, 100.86) * mm, "end": v(67.17, 100.26) * mm});
            skLineSegment(sketch, "E1087", {"start": v(67.17, 100.26) * mm, "end": v(68.48, 99.27) * mm});
            skLineSegment(sketch, "E1088", {"start": v(68.48, 99.27) * mm, "end": v(69, 99.61) * mm});
            skLineSegment(sketch, "E1089", {"start": v(69, 99.61) * mm, "end": v(70.08, 100.3) * mm});
            skLineSegment(sketch, "E1090", {"start": v(70.08, 100.3) * mm, "end": v(70.64, 100.63) * mm});
            skLineSegment(sketch, "E1091", {"start": v(70.64, 100.63) * mm, "end": v(71.9, 99.62) * mm});
            skLineSegment(sketch, "E1092", {"start": v(71.9, 99.62) * mm, "end": v(71.7, 99.01) * mm});
            skLineSegment(sketch, "E1093", {"start": v(71.7, 99.01) * mm, "end": v(71.29, 97.8) * mm});
            skLineSegment(sketch, "E1094", {"start": v(71.29, 97.8) * mm, "end": v(71.07, 97.21) * mm});
            skLineSegment(sketch, "E1095", {"start": v(71.07, 97.21) * mm, "end": v(72.34, 96.17) * mm});
            skLineSegment(sketch, "E1096", {"start": v(72.34, 96.17) * mm, "end": v(72.88, 96.5) * mm});
            skLineSegment(sketch, "E1097", {"start": v(72.88, 96.5) * mm, "end": v(73.99, 97.13) * mm});
            skLineSegment(sketch, "E1098", {"start": v(73.99, 97.13) * mm, "end": v(74.55, 97.44) * mm});
            skLineSegment(sketch, "E1099", {"start": v(74.55, 97.44) * mm, "end": v(75.77, 96.39) * mm});
            skLineSegment(sketch, "E1100", {"start": v(75.77, 96.39) * mm, "end": v(75.55, 95.79) * mm});
            skLineSegment(sketch, "E1101", {"start": v(75.55, 95.79) * mm, "end": v(75.1, 94.6) * mm});
            skLineSegment(sketch, "E1102", {"start": v(75.1, 94.6) * mm, "end": v(74.85, 94) * mm});
            skLineSegment(sketch, "E1103", {"start": v(74.85, 94) * mm, "end": v(76.07, 92.91) * mm});
            skLineSegment(sketch, "E1104", {"start": v(76.07, 92.91) * mm, "end": v(76.63, 93.22) * mm});
            skLineSegment(sketch, "E1105", {"start": v(76.63, 93.22) * mm, "end": v(77.76, 93.81) * mm});
            skLineSegment(sketch, "E1106", {"start": v(77.76, 93.81) * mm, "end": v(78.33, 94.1) * mm});
            skLineSegment(sketch, "E1107", {"start": v(78.33, 94.1) * mm, "end": v(79.51, 93) * mm});
            skLineSegment(sketch, "E1108", {"start": v(79.51, 93) * mm, "end": v(79.27, 92.4) * mm});
            skLineSegment(sketch, "E1109", {"start": v(79.27, 92.4) * mm, "end": v(78.76, 91.24) * mm});
            skLineSegment(sketch, "E1110", {"start": v(78.76, 91.24) * mm, "end": v(78.5, 90.66) * mm});
            skLineSegment(sketch, "E1111", {"start": v(78.5, 90.66) * mm, "end": v(79.68, 89.52) * mm});
            skLineSegment(sketch, "E1112", {"start": v(79.68, 89.52) * mm, "end": v(80.25, 89.8) * mm});
            skLineSegment(sketch, "E1113", {"start": v(80.25, 89.8) * mm, "end": v(81.4, 90.35) * mm});
            skLineSegment(sketch, "E1114", {"start": v(81.4, 90.35) * mm, "end": v(81.98, 90.62) * mm});
            skLineSegment(sketch, "E1115", {"start": v(81.98, 90.62) * mm, "end": v(83.12, 89.47) * mm});
            skLineSegment(sketch, "E1116", {"start": v(83.12, 89.47) * mm, "end": v(82.85, 88.89) * mm});
            skLineSegment(sketch, "E1117", {"start": v(82.85, 88.89) * mm, "end": v(82.3, 87.74) * mm});
            skLineSegment(sketch, "E1118", {"start": v(82.3, 87.74) * mm, "end": v(82.01, 87.17) * mm});
            skLineSegment(sketch, "E1119", {"start": v(82.01, 87.17) * mm, "end": v(83.15, 85.98) * mm});
            skLineSegment(sketch, "E1120", {"start": v(83.15, 85.98) * mm, "end": v(83.72, 86.25) * mm});
            skLineSegment(sketch, "E1121", {"start": v(83.72, 86.25) * mm, "end": v(84.9, 86.75) * mm});
            skLineSegment(sketch, "E1122", {"start": v(84.9, 86.75) * mm, "end": v(85.5, 86.99) * mm});
            skLineSegment(sketch, "E1123", {"start": v(85.5, 86.99) * mm, "end": v(86.58, 85.8) * mm});
            skLineSegment(sketch, "E1124", {"start": v(86.58, 85.8) * mm, "end": v(86.3, 85.23) * mm});
            skLineSegment(sketch, "E1125", {"start": v(86.3, 85.23) * mm, "end": v(85.7, 84.1) * mm});
            skLineSegment(sketch, "E1126", {"start": v(85.7, 84.1) * mm, "end": v(85.39, 83.55) * mm});
            skLineSegment(sketch, "E1127", {"start": v(85.39, 83.55) * mm, "end": v(86.47, 82.32) * mm});
            skLineSegment(sketch, "E1128", {"start": v(86.47, 82.32) * mm, "end": v(87.06, 82.55) * mm});
            skLineSegment(sketch, "E1129", {"start": v(87.06, 82.55) * mm, "end": v(88.25, 83) * mm});
            skLineSegment(sketch, "E1130", {"start": v(88.25, 83) * mm, "end": v(88.86, 83.23) * mm});
            skLineSegment(sketch, "E1131", {"start": v(88.86, 83.23) * mm, "end": v(89.9, 82) * mm});
            skLineSegment(sketch, "E1132", {"start": v(89.9, 82) * mm, "end": v(89.59, 81.43) * mm});
            skLineSegment(sketch, "E1133", {"start": v(89.59, 81.43) * mm, "end": v(88.95, 80.33) * mm});
            skLineSegment(sketch, "E1134", {"start": v(88.95, 80.33) * mm, "end": v(88.61, 79.8) * mm});
            skLineSegment(sketch, "E1135", {"start": v(88.61, 79.8) * mm, "end": v(89.65, 78.52) * mm});
            skLineSegment(sketch, "E1136", {"start": v(89.65, 78.52) * mm, "end": v(90.25, 78.73) * mm});
            skLineSegment(sketch, "E1137", {"start": v(90.25, 78.73) * mm, "end": v(91.46, 79.14) * mm});
            skLineSegment(sketch, "E1138", {"start": v(91.46, 79.14) * mm, "end": v(92.07, 79.33) * mm});
            skLineSegment(sketch, "E1139", {"start": v(92.07, 79.33) * mm, "end": v(93.06, 78.06) * mm});
            skLineSegment(sketch, "E1140", {"start": v(93.06, 78.06) * mm, "end": v(92.73, 77.51) * mm});
            skLineSegment(sketch, "E1141", {"start": v(92.73, 77.51) * mm, "end": v(92.04, 76.44) * mm});
            skLineSegment(sketch, "E1142", {"start": v(92.04, 76.44) * mm, "end": v(91.7, 75.91) * mm});
            skLineSegment(sketch, "E1143", {"start": v(91.7, 75.91) * mm, "end": v(92.68, 74.6) * mm});
            skLineSegment(sketch, "E1144", {"start": v(92.68, 74.6) * mm, "end": v(93.28, 74.79) * mm});
            skLineSegment(sketch, "E1145", {"start": v(93.28, 74.79) * mm, "end": v(94.5, 75.15) * mm});
            skLineSegment(sketch, "E1146", {"start": v(94.5, 75.15) * mm, "end": v(95.13, 75.32) * mm});
            skLineSegment(sketch, "E1147", {"start": v(95.13, 75.32) * mm, "end": v(96.07, 74) * mm});
            skLineSegment(sketch, "E1148", {"start": v(96.07, 74) * mm, "end": v(95.71, 73.47) * mm});
            skLineSegment(sketch, "E1149", {"start": v(95.71, 73.47) * mm, "end": v(94.99, 72.42) * mm});
            skLineSegment(sketch, "E1150", {"start": v(94.99, 72.42) * mm, "end": v(94.61, 71.91) * mm});
            skLineSegment(sketch, "E1151", {"start": v(94.61, 71.91) * mm, "end": v(95.55, 70.56) * mm});
            skLineSegment(sketch, "E1152", {"start": v(95.55, 70.56) * mm, "end": v(96.16, 70.73) * mm});
            skLineSegment(sketch, "E1153", {"start": v(96.16, 70.73) * mm, "end": v(97.4, 71.04) * mm});
            skLineSegment(sketch, "E1154", {"start": v(97.4, 71.04) * mm, "end": v(98.02, 71.18) * mm});
            skLineSegment(sketch, "E1155", {"start": v(98.02, 71.18) * mm, "end": v(98.91, 69.84) * mm});
            skLineSegment(sketch, "E1156", {"start": v(98.91, 69.84) * mm, "end": v(98.54, 69.32) * mm});
            skLineSegment(sketch, "E1157", {"start": v(98.54, 69.32) * mm, "end": v(97.77, 68.3) * mm});
            skLineSegment(sketch, "E1158", {"start": v(97.77, 68.3) * mm, "end": v(97.37, 67.8) * mm});
            skLineSegment(sketch, "E1159", {"start": v(97.37, 67.8) * mm, "end": v(98.25, 66.41) * mm});
            skLineSegment(sketch, "E1160", {"start": v(98.25, 66.41) * mm, "end": v(98.87, 66.56) * mm});
            skLineSegment(sketch, "E1161", {"start": v(98.87, 66.56) * mm, "end": v(100.12, 66.82) * mm});
            skLineSegment(sketch, "E1162", {"start": v(100.12, 66.82) * mm, "end": v(100.75, 66.94) * mm});
            skLineSegment(sketch, "E1163", {"start": v(100.75, 66.94) * mm, "end": v(101.59, 65.56) * mm});
            skLineSegment(sketch, "E1164", {"start": v(101.59, 65.56) * mm, "end": v(101.2, 65.05) * mm});
            skLineSegment(sketch, "E1165", {"start": v(101.2, 65.05) * mm, "end": v(100.38, 64.07) * mm});
            skLineSegment(sketch, "E1166", {"start": v(100.38, 64.07) * mm, "end": v(99.97, 63.58) * mm});
            skLineSegment(sketch, "E1167", {"start": v(99.97, 63.58) * mm, "end": v(100.8, 62.16) * mm});
            skLineSegment(sketch, "E1168", {"start": v(100.8, 62.16) * mm, "end": v(101.42, 62.28) * mm});
            skLineSegment(sketch, "E1169", {"start": v(101.42, 62.28) * mm, "end": v(102.68, 62.5) * mm});
            skLineSegment(sketch, "E1170", {"start": v(102.68, 62.5) * mm, "end": v(103.31, 62.59) * mm});
            skLineSegment(sketch, "E1171", {"start": v(103.31, 62.59) * mm, "end": v(104.1, 61.18) * mm});
            skLineSegment(sketch, "E1172", {"start": v(104.1, 61.18) * mm, "end": v(103.68, 60.69) * mm});
            skLineSegment(sketch, "E1173", {"start": v(103.68, 60.69) * mm, "end": v(102.83, 59.73) * mm});
            skLineSegment(sketch, "E1174", {"start": v(102.83, 59.73) * mm, "end": v(102.4, 59.27) * mm});
            skLineSegment(sketch, "E1175", {"start": v(102.4, 59.27) * mm, "end": v(103.16, 57.82) * mm});
            skLineSegment(sketch, "E1176", {"start": v(103.16, 57.82) * mm, "end": v(103.8, 57.9) * mm});
            skLineSegment(sketch, "E1177", {"start": v(103.8, 57.9) * mm, "end": v(105.06, 58.07) * mm});
            skLineSegment(sketch, "E1178", {"start": v(105.06, 58.07) * mm, "end": v(105.7, 58.14) * mm});
            skLineSegment(sketch, "E1179", {"start": v(105.7, 58.14) * mm, "end": v(106.42, 56.7) * mm});
            skLineSegment(sketch, "E1180", {"start": v(106.42, 56.7) * mm, "end": v(105.99, 56.23) * mm});
            skLineSegment(sketch, "E1181", {"start": v(105.99, 56.23) * mm, "end": v(105.1, 55.3) * mm});
            skLineSegment(sketch, "E1182", {"start": v(105.1, 55.3) * mm, "end": v(104.65, 54.86) * mm});
            skLineSegment(sketch, "E1183", {"start": v(104.65, 54.86) * mm, "end": v(105.36, 53.38) * mm});
            skLineSegment(sketch, "E1184", {"start": v(105.36, 53.38) * mm, "end": v(106, 53.45) * mm});
            skLineSegment(sketch, "E1185", {"start": v(106, 53.45) * mm, "end": v(107.26, 53.56) * mm});
            skLineSegment(sketch, "E1186", {"start": v(107.26, 53.56) * mm, "end": v(107.9, 53.6) * mm});
            skLineSegment(sketch, "E1187", {"start": v(107.9, 53.6) * mm, "end": v(108.57, 52.13) * mm});
            skLineSegment(sketch, "E1188", {"start": v(108.57, 52.13) * mm, "end": v(108.12, 51.68) * mm});
            skLineSegment(sketch, "E1189", {"start": v(108.12, 51.68) * mm, "end": v(107.2, 50.8) * mm});
            skLineSegment(sketch, "E1190", {"start": v(107.2, 50.8) * mm, "end": v(106.73, 50.36) * mm});
            skLineSegment(sketch, "E1191", {"start": v(106.73, 50.36) * mm, "end": v(107.38, 48.86) * mm});
            skLineSegment(sketch, "E1192", {"start": v(107.38, 48.86) * mm, "end": v(108.01, 48.9) * mm});
            skLineSegment(sketch, "E1193", {"start": v(108.01, 48.9) * mm, "end": v(109.29, 48.96) * mm});
            skLineSegment(sketch, "E1194", {"start": v(109.29, 48.96) * mm, "end": v(109.93, 48.98) * mm});
            skLineSegment(sketch, "E1195", {"start": v(109.93, 48.98) * mm, "end": v(110.54, 47.49) * mm});
            skLineSegment(sketch, "E1196", {"start": v(110.54, 47.49) * mm, "end": v(110.07, 47.05) * mm});
            skLineSegment(sketch, "E1197", {"start": v(110.07, 47.05) * mm, "end": v(109.12, 46.2) * mm});
            skLineSegment(sketch, "E1198", {"start": v(109.12, 46.2) * mm, "end": v(108.63, 45.8) * mm});
            skLineSegment(sketch, "E1199", {"start": v(108.63, 45.8) * mm, "end": v(109.22, 44.26) * mm});
            skLineSegment(sketch, "E1200", {"start": v(109.22, 44.26) * mm, "end": v(109.86, 44.28) * mm});
            skLineSegment(sketch, "E1201", {"start": v(109.86, 44.28) * mm, "end": v(111.13, 44.29) * mm});
            skLineSegment(sketch, "E1202", {"start": v(111.13, 44.29) * mm, "end": v(111.78, 44.28) * mm});
            skLineSegment(sketch, "E1203", {"start": v(111.78, 44.28) * mm, "end": v(112.32, 42.77) * mm});
            skLineSegment(sketch, "E1204", {"start": v(112.32, 42.77) * mm, "end": v(111.84, 42.35) * mm});
            skLineSegment(sketch, "E1205", {"start": v(111.84, 42.35) * mm, "end": v(110.85, 41.54) * mm});
            skLineSegment(sketch, "E1206", {"start": v(110.85, 41.54) * mm, "end": v(110.35, 41.15) * mm});
            skLineSegment(sketch, "E1207", {"start": v(110.35, 41.15) * mm, "end": v(110.88, 39.6) * mm});
            skLineSegment(sketch, "E1208", {"start": v(110.88, 39.6) * mm, "end": v(111.51, 39.59) * mm});
            skLineSegment(sketch, "E1209", {"start": v(111.51, 39.59) * mm, "end": v(112.79, 39.55) * mm});
            skLineSegment(sketch, "E1210", {"start": v(112.79, 39.55) * mm, "end": v(113.43, 39.51) * mm});
            skLineSegment(sketch, "E1211", {"start": v(113.43, 39.51) * mm, "end": v(113.92, 37.98) * mm});
            skLineSegment(sketch, "E1212", {"start": v(113.92, 37.98) * mm, "end": v(113.42, 37.58) * mm});
            skLineSegment(sketch, "E1213", {"start": v(113.42, 37.58) * mm, "end": v(112.4, 36.8) * mm});
            skLineSegment(sketch, "E1214", {"start": v(112.4, 36.8) * mm, "end": v(111.88, 36.44) * mm});
            skLineSegment(sketch, "E1215", {"start": v(111.88, 36.44) * mm, "end": v(112.35, 34.86) * mm});
            skLineSegment(sketch, "E1216", {"start": v(112.35, 34.86) * mm, "end": v(112.98, 34.83) * mm});
            skLineSegment(sketch, "E1217", {"start": v(112.98, 34.83) * mm, "end": v(114.26, 34.74) * mm});
            skLineSegment(sketch, "E1218", {"start": v(114.26, 34.74) * mm, "end": v(114.9, 34.68) * mm});
            skLineSegment(sketch, "E1219", {"start": v(114.9, 34.68) * mm, "end": v(115.33, 33.13) * mm});
            skLineSegment(sketch, "E1220", {"start": v(115.33, 33.13) * mm, "end": v(114.8, 32.75) * mm});
            skLineSegment(sketch, "E1221", {"start": v(114.8, 32.75) * mm, "end": v(113.76, 32.02) * mm});
            skLineSegment(sketch, "E1222", {"start": v(113.76, 32.02) * mm, "end": v(113.23, 31.67) * mm});
            skLineSegment(sketch, "E1223", {"start": v(113.23, 31.67) * mm, "end": v(113.63, 30.08) * mm});
            skLineSegment(sketch, "E1224", {"start": v(113.63, 30.08) * mm, "end": v(114.27, 30.02) * mm});
            skLineSegment(sketch, "E1225", {"start": v(114.27, 30.02) * mm, "end": v(115.53, 29.88) * mm});
            skLineSegment(sketch, "E1226", {"start": v(115.53, 29.88) * mm, "end": v(116.17, 29.8) * mm});
            skLineSegment(sketch, "E1227", {"start": v(116.17, 29.8) * mm, "end": v(116.54, 28.23) * mm});
            skLineSegment(sketch, "E1228", {"start": v(116.54, 28.23) * mm, "end": v(116, 27.87) * mm});
            skLineSegment(sketch, "E1229", {"start": v(116, 27.87) * mm, "end": v(114.93, 27.19) * mm});
            skLineSegment(sketch, "E1230", {"start": v(114.93, 27.19) * mm, "end": v(114.39, 26.86) * mm});
            skLineSegment(sketch, "E1231", {"start": v(114.39, 26.86) * mm, "end": v(114.73, 25.25) * mm});
            skLineSegment(sketch, "E1232", {"start": v(114.73, 25.25) * mm, "end": v(115.36, 25.17) * mm});
            skLineSegment(sketch, "E1233", {"start": v(115.36, 25.17) * mm, "end": v(116.62, 24.98) * mm});
            skLineSegment(sketch, "E1234", {"start": v(116.62, 24.98) * mm, "end": v(117.25, 24.87) * mm});
            skLineSegment(sketch, "E1235", {"start": v(117.25, 24.87) * mm, "end": v(117.56, 23.29) * mm});
            skLineSegment(sketch, "E1236", {"start": v(117.56, 23.29) * mm, "end": v(117, 22.95) * mm});
            skLineSegment(sketch, "E1237", {"start": v(117, 22.95) * mm, "end": v(115.9, 22.3) * mm});
            skLineSegment(sketch, "E1238", {"start": v(115.9, 22.3) * mm, "end": v(115.35, 22) * mm});
            skLineSegment(sketch, "E1239", {"start": v(115.35, 22) * mm, "end": v(115.63, 20.38) * mm});
            skLineSegment(sketch, "E1240", {"start": v(115.63, 20.38) * mm, "end": v(116.26, 20.28) * mm});
            skLineSegment(sketch, "E1241", {"start": v(116.26, 20.28) * mm, "end": v(117.5, 20.04) * mm});
            skLineSegment(sketch, "E1242", {"start": v(117.5, 20.04) * mm, "end": v(118.14, 19.9) * mm});
            skLineSegment(sketch, "E1243", {"start": v(118.14, 19.9) * mm, "end": v(118.38, 18.3) * mm});
            skLineSegment(sketch, "E1244", {"start": v(118.38, 18.3) * mm, "end": v(117.82, 18) * mm});
            skLineSegment(sketch, "E1245", {"start": v(117.82, 18) * mm, "end": v(116.7, 17.4) * mm});
            skLineSegment(sketch, "E1246", {"start": v(116.7, 17.4) * mm, "end": v(116.13, 17.1) * mm});
            skLineSegment(sketch, "E1247", {"start": v(116.13, 17.1) * mm, "end": v(116.34, 15.48) * mm});
            skLineSegment(sketch, "E1248", {"start": v(116.34, 15.48) * mm, "end": v(116.96, 15.35) * mm});
            skLineSegment(sketch, "E1249", {"start": v(116.96, 15.35) * mm, "end": v(118.2, 15.06) * mm});
            skLineSegment(sketch, "E1250", {"start": v(118.2, 15.06) * mm, "end": v(118.83, 14.9) * mm});
            skLineSegment(sketch, "E1251", {"start": v(118.83, 14.9) * mm, "end": v(119, 13.3) * mm});
            skLineSegment(sketch, "E1252", {"start": v(119, 13.3) * mm, "end": v(118.43, 13) * mm});
            skLineSegment(sketch, "E1253", {"start": v(118.43, 13) * mm, "end": v(117.28, 12.45) * mm});
            skLineSegment(sketch, "E1254", {"start": v(117.28, 12.45) * mm, "end": v(116.7, 12.19) * mm});
            skLineSegment(sketch, "E1255", {"start": v(116.7, 12.19) * mm, "end": v(116.85, 10.55) * mm});
            skLineSegment(sketch, "E1256", {"start": v(116.85, 10.55) * mm, "end": v(117.47, 10.4) * mm});
            skLineSegment(sketch, "E1257", {"start": v(117.47, 10.4) * mm, "end": v(118.7, 10.06) * mm});
            skLineSegment(sketch, "E1258", {"start": v(118.7, 10.06) * mm, "end": v(119.32, 9.88) * mm});
            skLineSegment(sketch, "E1259", {"start": v(119.32, 9.88) * mm, "end": v(119.43, 8.27) * mm});
            skLineSegment(sketch, "E1260", {"start": v(119.43, 8.27) * mm, "end": v(118.85, 8) * mm});
            skLineSegment(sketch, "E1261", {"start": v(118.85, 8) * mm, "end": v(117.68, 7.5) * mm});
            skLineSegment(sketch, "E1262", {"start": v(117.68, 7.5) * mm, "end": v(117.09, 7.25) * mm});
            skLineSegment(sketch, "E1263", {"start": v(117.09, 7.25) * mm, "end": v(117.17, 5.61) * mm});
            skLineSegment(sketch, "E1264", {"start": v(117.17, 5.61) * mm, "end": v(117.78, 5.43) * mm});
            skLineSegment(sketch, "E1265", {"start": v(117.78, 5.43) * mm, "end": v(119, 5.05) * mm});
            skLineSegment(sketch, "E1266", {"start": v(119, 5.05) * mm, "end": v(119.6, 4.84) * mm});
            skLineSegment(sketch, "E1267", {"start": v(119.6, 4.84) * mm, "end": v(119.66, 3.23) * mm});
            skLineSegment(sketch, "E1268", {"start": v(119.66, 3.23) * mm, "end": v(119.06, 2.98) * mm});
            skLineSegment(sketch, "E1269", {"start": v(119.06, 2.98) * mm, "end": v(117.87, 2.52) * mm});
            skLineSegment(sketch, "E1270", {"start": v(117.87, 2.52) * mm, "end": v(117.28, 2.3) * mm});
            skLineSegment(sketch, "E1271", {"start": v(117.28, 2.3) * mm, "end": v(117.3, 0.66) * mm});
            skLineSegment(sketch, "E1272", {"start": v(19.73, 7.44) * mm, "end": v(101.77, 6.8) * mm});
            skLineSegment(sketch, "E1273", {"start": v(101.77, 6.8) * mm, "end": v(105.3, 10.6) * mm});
            skLineSegment(sketch, "E1274", {"start": v(105.3, 10.6) * mm, "end": v(104.28, 18.54) * mm});
            skLineSegment(sketch, "E1275", {"start": v(104.28, 18.54) * mm, "end": v(102.7, 26.4) * mm});
            skLineSegment(sketch, "E1276", {"start": v(102.7, 26.4) * mm, "end": v(100.57, 34.12) * mm});
            skLineSegment(sketch, "E1277", {"start": v(100.57, 34.12) * mm, "end": v(97.9, 41.68) * mm});
            skLineSegment(sketch, "E1278", {"start": v(97.9, 41.68) * mm, "end": v(94.7, 49.03) * mm});
            skLineSegment(sketch, "E1279", {"start": v(94.7, 49.03) * mm, "end": v(91, 56.13) * mm});
            skLineSegment(sketch, "E1280", {"start": v(91, 56.13) * mm, "end": v(86.8, 62.96) * mm});
            skLineSegment(sketch, "E1281", {"start": v(86.8, 62.96) * mm, "end": v(82.14, 69.48) * mm});
            skLineSegment(sketch, "E1282", {"start": v(82.14, 69.48) * mm, "end": v(77.03, 75.65) * mm});
            skLineSegment(sketch, "E1283", {"start": v(77.03, 75.65) * mm, "end": v(71.5, 81.44) * mm});
            skLineSegment(sketch, "E1284", {"start": v(71.5, 81.44) * mm, "end": v(65.57, 86.84) * mm});
            skLineSegment(sketch, "E1285", {"start": v(65.57, 86.84) * mm, "end": v(59.28, 91.8) * mm});
            skLineSegment(sketch, "E1286", {"start": v(59.28, 91.8) * mm, "end": v(54.2, 90.72) * mm});
            skLineSegment(sketch, "E1287", {"start": v(54.2, 90.72) * mm, "end": v(12.61, 19.99) * mm});
            skLineSegment(sketch, "E1288", {"start": v(12.61, 19.99) * mm, "end": v(13.17, 13.37) * mm});
            skLineSegment(sketch, "E1289", {"start": v(13.17, 13.37) * mm, "end": v(19.73, 7.44) * mm});
            skLineSegment(sketch, "E1290", {"start": v(-0.6, 27.76) * mm, "end": v(40.98, 98.48) * mm});
            skLineSegment(sketch, "E1291", {"start": v(40.98, 98.48) * mm, "end": v(39.46, 103.45) * mm});
            skLineSegment(sketch, "E1292", {"start": v(39.46, 103.45) * mm, "end": v(32.06, 106.54) * mm});
            skLineSegment(sketch, "E1293", {"start": v(32.06, 106.54) * mm, "end": v(24.47, 109.1) * mm});
            skLineSegment(sketch, "E1294", {"start": v(24.47, 109.1) * mm, "end": v(16.71, 111.1) * mm});
            skLineSegment(sketch, "E1295", {"start": v(16.71, 111.1) * mm, "end": v(8.84, 112.57) * mm});
            skLineSegment(sketch, "E1296", {"start": v(8.84, 112.57) * mm, "end": v(0.88, 113.48) * mm});
            skLineSegment(sketch, "E1297", {"start": v(0.88, 113.48) * mm, "end": v(-7.13, 113.83) * mm});
            skLineSegment(sketch, "E1298", {"start": v(-7.13, 113.83) * mm, "end": v(-15.14, 113.6) * mm});
            skLineSegment(sketch, "E1299", {"start": v(-15.14, 113.6) * mm, "end": v(-23.11, 112.83) * mm});
            skLineSegment(sketch, "E1300", {"start": v(-23.11, 112.83) * mm, "end": v(-31.01, 111.48) * mm});
            skLineSegment(sketch, "E1301", {"start": v(-31.01, 111.48) * mm, "end": v(-38.8, 109.6) * mm});
            skLineSegment(sketch, "E1302", {"start": v(-38.8, 109.6) * mm, "end": v(-46.43, 107.16) * mm});
            skLineSegment(sketch, "E1303", {"start": v(-46.43, 107.16) * mm, "end": v(-53.88, 104.19) * mm});
            skLineSegment(sketch, "E1304", {"start": v(-53.88, 104.19) * mm, "end": v(-55.48, 99.25) * mm});
            skLineSegment(sketch, "E1305", {"start": v(-55.48, 99.25) * mm, "end": v(-15.02, 27.87) * mm});
            skLineSegment(sketch, "E1306", {"start": v(-15.02, 27.87) * mm, "end": v(-9.01, 25.04) * mm});
            skLineSegment(sketch, "E1307", {"start": v(-9.01, 25.04) * mm, "end": v(-0.6, 27.76) * mm});
            skLineSegment(sketch, "E1308", {"start": v(-28.36, 20.31) * mm, "end": v(-68.82, 91.69) * mm});
            skLineSegment(sketch, "E1309", {"start": v(-68.82, 91.69) * mm, "end": v(-73.88, 92.85) * mm});
            skLineSegment(sketch, "E1310", {"start": v(-73.88, 92.85) * mm, "end": v(-80.25, 87.99) * mm});
            skLineSegment(sketch, "E1311", {"start": v(-80.25, 87.99) * mm, "end": v(-86.26, 82.69) * mm});
            skLineSegment(sketch, "E1312", {"start": v(-86.26, 82.69) * mm, "end": v(-91.88, 76.98) * mm});
            skLineSegment(sketch, "E1313", {"start": v(-91.88, 76.98) * mm, "end": v(-97.1, 70.9) * mm});
            skLineSegment(sketch, "E1314", {"start": v(-97.1, 70.9) * mm, "end": v(-101.86, 64.45) * mm});
            skLineSegment(sketch, "E1315", {"start": v(-101.86, 64.45) * mm, "end": v(-106.16, 57.7) * mm});
            skLineSegment(sketch, "E1316", {"start": v(-106.16, 57.7) * mm, "end": v(-109.97, 50.64) * mm});
            skLineSegment(sketch, "E1317", {"start": v(-109.97, 50.64) * mm, "end": v(-113.29, 43.35) * mm});
            skLineSegment(sketch, "E1318", {"start": v(-113.29, 43.35) * mm, "end": v(-116.07, 35.83) * mm});
            skLineSegment(sketch, "E1319", {"start": v(-116.07, 35.83) * mm, "end": v(-118.33, 28.15) * mm});
            skLineSegment(sketch, "E1320", {"start": v(-118.33, 28.15) * mm, "end": v(-120.03, 20.32) * mm});
            skLineSegment(sketch, "E1321", {"start": v(-120.03, 20.32) * mm, "end": v(-121.19, 12.39) * mm});
            skLineSegment(sketch, "E1322", {"start": v(-121.19, 12.39) * mm, "end": v(-117.7, 8.53) * mm});
            skLineSegment(sketch, "E1323", {"start": v(-117.7, 8.53) * mm, "end": v(-35.67, 7.88) * mm});
            skLineSegment(sketch, "E1324", {"start": v(-35.67, 7.88) * mm, "end": v(-30.21, 11.67) * mm});
            skLineSegment(sketch, "E1325", {"start": v(-30.21, 11.67) * mm, "end": v(-28.36, 20.31) * mm});
            skLineSegment(sketch, "E1326", {"start": v(-35.79, -7.45) * mm, "end": v(-117.83, -6.8) * mm});
            skLineSegment(sketch, "E1327", {"start": v(-117.83, -6.8) * mm, "end": v(-121.37, -10.6) * mm});
            skLineSegment(sketch, "E1328", {"start": v(-121.37, -10.6) * mm, "end": v(-120.34, -18.55) * mm});
            skLineSegment(sketch, "E1329", {"start": v(-120.34, -18.55) * mm, "end": v(-118.76, -26.4) * mm});
            skLineSegment(sketch, "E1330", {"start": v(-118.76, -26.4) * mm, "end": v(-116.63, -34.13) * mm});
            skLineSegment(sketch, "E1331", {"start": v(-116.63, -34.13) * mm, "end": v(-113.96, -41.69) * mm});
            skLineSegment(sketch, "E1332", {"start": v(-113.96, -41.69) * mm, "end": v(-110.76, -49.03) * mm});
            skLineSegment(sketch, "E1333", {"start": v(-110.76, -49.03) * mm, "end": v(-107.06, -56.14) * mm});
            skLineSegment(sketch, "E1334", {"start": v(-107.06, -56.14) * mm, "end": v(-102.86, -62.97) * mm});
            skLineSegment(sketch, "E1335", {"start": v(-102.86, -62.97) * mm, "end": v(-98.2, -69.48) * mm});
            skLineSegment(sketch, "E1336", {"start": v(-98.2, -69.48) * mm, "end": v(-93.09, -75.65) * mm});
            skLineSegment(sketch, "E1337", {"start": v(-93.09, -75.65) * mm, "end": v(-87.56, -81.45) * mm});
            skLineSegment(sketch, "E1338", {"start": v(-87.56, -81.45) * mm, "end": v(-81.63, -86.84) * mm});
            skLineSegment(sketch, "E1339", {"start": v(-81.63, -86.84) * mm, "end": v(-75.34, -91.8) * mm});
            skLineSegment(sketch, "E1340", {"start": v(-75.34, -91.8) * mm, "end": v(-70.26, -90.72) * mm});
            skLineSegment(sketch, "E1341", {"start": v(-70.26, -90.72) * mm, "end": v(-28.67, -20) * mm});
            skLineSegment(sketch, "E1342", {"start": v(-28.67, -20) * mm, "end": v(-29.23, -13.38) * mm});
            skLineSegment(sketch, "E1343", {"start": v(-29.23, -13.38) * mm, "end": v(-35.79, -7.45) * mm});
            skLineSegment(sketch, "E1344", {"start": v(-15.46, -27.76) * mm, "end": v(-57.04, -98.5) * mm});
            skLineSegment(sketch, "E1345", {"start": v(-57.04, -98.5) * mm, "end": v(-55.52, -103.46) * mm});
            skLineSegment(sketch, "E1346", {"start": v(-55.52, -103.46) * mm, "end": v(-48.12, -106.54) * mm});
            skLineSegment(sketch, "E1347", {"start": v(-48.12, -106.54) * mm, "end": v(-40.53, -109.1) * mm});
            skLineSegment(sketch, "E1348", {"start": v(-40.53, -109.1) * mm, "end": v(-32.77, -111.11) * mm});
            skLineSegment(sketch, "E1349", {"start": v(-32.77, -111.11) * mm, "end": v(-24.9, -112.58) * mm});
            skLineSegment(sketch, "E1350", {"start": v(-24.9, -112.58) * mm, "end": v(-16.93, -113.49) * mm});
            skLineSegment(sketch, "E1351", {"start": v(-16.93, -113.49) * mm, "end": v(-8.93, -113.83) * mm});
            skLineSegment(sketch, "E1352", {"start": v(-8.93, -113.83) * mm, "end": v(-0.92, -113.61) * mm});
            skLineSegment(sketch, "E1353", {"start": v(-0.92, -113.61) * mm, "end": v(7.06, -112.83) * mm});
            skLineSegment(sketch, "E1354", {"start": v(7.06, -112.83) * mm, "end": v(14.96, -111.5) * mm});
            skLineSegment(sketch, "E1355", {"start": v(14.96, -111.5) * mm, "end": v(22.74, -109.6) * mm});
            skLineSegment(sketch, "E1356", {"start": v(22.74, -109.6) * mm, "end": v(30.38, -107.16) * mm});
            skLineSegment(sketch, "E1357", {"start": v(30.38, -107.16) * mm, "end": v(37.82, -104.2) * mm});
            skLineSegment(sketch, "E1358", {"start": v(37.82, -104.2) * mm, "end": v(39.42, -99.25) * mm});
            skLineSegment(sketch, "E1359", {"start": v(39.42, -99.25) * mm, "end": v(-1.04, -27.88) * mm});
            skLineSegment(sketch, "E1360", {"start": v(-1.04, -27.88) * mm, "end": v(-7.05, -25.05) * mm});
            skLineSegment(sketch, "E1361", {"start": v(-7.05, -25.05) * mm, "end": v(-15.46, -27.76) * mm});
            skLineSegment(sketch, "E1362", {"start": v(12.3, -20.32) * mm, "end": v(52.76, -91.7) * mm});
            skLineSegment(sketch, "E1363", {"start": v(52.76, -91.7) * mm, "end": v(57.82, -92.86) * mm});
            skLineSegment(sketch, "E1364", {"start": v(57.82, -92.86) * mm, "end": v(64.19, -88) * mm});
            skLineSegment(sketch, "E1365", {"start": v(64.19, -88) * mm, "end": v(70.2, -82.7) * mm});
            skLineSegment(sketch, "E1366", {"start": v(70.2, -82.7) * mm, "end": v(75.82, -76.99) * mm});
            skLineSegment(sketch, "E1367", {"start": v(75.82, -76.99) * mm, "end": v(81.03, -70.9) * mm});
            skLineSegment(sketch, "E1368", {"start": v(81.03, -70.9) * mm, "end": v(85.8, -64.46) * mm});
            skLineSegment(sketch, "E1369", {"start": v(85.8, -64.46) * mm, "end": v(90.1, -57.7) * mm});
            skLineSegment(sketch, "E1370", {"start": v(90.1, -57.7) * mm, "end": v(93.92, -50.65) * mm});
            skLineSegment(sketch, "E1371", {"start": v(93.92, -50.65) * mm, "end": v(97.23, -43.35) * mm});
            skLineSegment(sketch, "E1372", {"start": v(97.23, -43.35) * mm, "end": v(100.01, -35.84) * mm});
            skLineSegment(sketch, "E1373", {"start": v(100.01, -35.84) * mm, "end": v(102.27, -28.15) * mm});
            skLineSegment(sketch, "E1374", {"start": v(102.27, -28.15) * mm, "end": v(103.98, -20.32) * mm});
            skLineSegment(sketch, "E1375", {"start": v(103.98, -20.32) * mm, "end": v(105.13, -12.4) * mm});
            skLineSegment(sketch, "E1376", {"start": v(105.13, -12.4) * mm, "end": v(101.65, -8.53) * mm});
            skLineSegment(sketch, "E1377", {"start": v(101.65, -8.53) * mm, "end": v(19.6, -7.89) * mm});
            skLineSegment(sketch, "E1378", {"start": v(19.6, -7.89) * mm, "end": v(14.15, -11.67) * mm});
            skLineSegment(sketch, "E1379", {"start": v(14.15, -11.67) * mm, "end": v(12.3, -20.32) * mm});
            skLineSegment(sketch, "E1380", {"start": v(-7.03, 0) * mm, "end": v(-7.06, 0.26) * mm});
            skLineSegment(sketch, "E1381", {"start": v(-7.06, 0.26) * mm, "end": v(-7.16, 0.5) * mm});
            skLineSegment(sketch, "E1382", {"start": v(-7.16, 0.5) * mm, "end": v(-7.32, 0.7) * mm});
            skLineSegment(sketch, "E1383", {"start": v(-7.32, 0.7) * mm, "end": v(-7.53, 0.86) * mm});
            skLineSegment(sketch, "E1384", {"start": v(-7.53, 0.86) * mm, "end": v(-7.77, 0.96) * mm});
            skLineSegment(sketch, "E1385", {"start": v(-7.77, 0.96) * mm, "end": v(-8.03, 1) * mm});
            skLineSegment(sketch, "E1386", {"start": v(-8.03, 1) * mm, "end": v(-8.29, 0.96) * mm});
            skLineSegment(sketch, "E1387", {"start": v(-8.29, 0.96) * mm, "end": v(-8.53, 0.86) * mm});
            skLineSegment(sketch, "E1388", {"start": v(-8.53, 0.86) * mm, "end": v(-8.74, 0.7) * mm});
            skLineSegment(sketch, "E1389", {"start": v(-8.74, 0.7) * mm, "end": v(-8.9, 0.5) * mm});
            skLineSegment(sketch, "E1390", {"start": v(-8.9, 0.5) * mm, "end": v(-9, 0.26) * mm});
            skLineSegment(sketch, "E1391", {"start": v(-9, 0.26) * mm, "end": v(-9.03, 0) * mm});
            skLineSegment(sketch, "E1392", {"start": v(-9.03, 0) * mm, "end": v(-9, -0.26) * mm});
            skLineSegment(sketch, "E1393", {"start": v(-9, -0.26) * mm, "end": v(-8.9, -0.5) * mm});
            skLineSegment(sketch, "E1394", {"start": v(-8.9, -0.5) * mm, "end": v(-8.74, -0.71) * mm});
            skLineSegment(sketch, "E1395", {"start": v(-8.74, -0.71) * mm, "end": v(-8.53, -0.87) * mm});
            skLineSegment(sketch, "E1396", {"start": v(-8.53, -0.87) * mm, "end": v(-8.29, -0.97) * mm});
            skLineSegment(sketch, "E1397", {"start": v(-8.29, -0.97) * mm, "end": v(-8.03, -1) * mm});
            skLineSegment(sketch, "E1398", {"start": v(-8.03, -1) * mm, "end": v(-7.77, -0.97) * mm});
            skLineSegment(sketch, "E1399", {"start": v(-7.77, -0.97) * mm, "end": v(-7.53, -0.87) * mm});
            skLineSegment(sketch, "E1400", {"start": v(-7.53, -0.87) * mm, "end": v(-7.32, -0.71) * mm});
            skLineSegment(sketch, "E1401", {"start": v(-7.32, -0.71) * mm, "end": v(-7.16, -0.5) * mm});
            skLineSegment(sketch, "E1402", {"start": v(-7.16, -0.5) * mm, "end": v(-7.06, -0.26) * mm});
            skLineSegment(sketch, "E1403", {"start": v(-7.06, -0.26) * mm, "end": v(-7.03, 0) * mm});
            skLineSegment(sketch, "E1404", {"start": v(-13.2, -0.17) * mm, "end": v(-13.28, 0) * mm});
            skLineSegment(sketch, "E1405", {"start": v(-13.28, 0) * mm, "end": v(-13.36, 0.05) * mm});
            skLineSegment(sketch, "E1406", {"start": v(-13.36, 0.05) * mm, "end": v(-13.51, 0.12) * mm});
            skLineSegment(sketch, "E1407", {"start": v(-13.51, 0.12) * mm, "end": v(-13.67, 0.15) * mm});
            skLineSegment(sketch, "E1408", {"start": v(-13.67, 0.15) * mm, "end": v(-14, 0.14) * mm});
            skLineSegment(sketch, "E1409", {"start": v(-14, 0.14) * mm, "end": v(-14.31, 0.21) * mm});
            skLineSegment(sketch, "E1410", {"start": v(-14.31, 0.21) * mm, "end": v(-14.63, 0.35) * mm});
            skLineSegment(sketch, "E1411", {"start": v(-14.63, 0.35) * mm, "end": v(-14.93, 0.54) * mm});
            skLineSegment(sketch, "E1412", {"start": v(-14.93, 0.54) * mm, "end": v(-15.23, 0.78) * mm});
            skLineSegment(sketch, "E1413", {"start": v(-15.23, 0.78) * mm, "end": v(-15.52, 1.05) * mm});
            skLineSegment(sketch, "E1414", {"start": v(-15.52, 1.05) * mm, "end": v(-15.39, 1.76) * mm});
            skLineSegment(sketch, "E1415", {"start": v(-15.39, 1.76) * mm, "end": v(-15.18, 2.45) * mm});
            skLineSegment(sketch, "E1416", {"start": v(-15.18, 2.45) * mm, "end": v(-14.8, 2.57) * mm});
            skLineSegment(sketch, "E1417", {"start": v(-14.8, 2.57) * mm, "end": v(-14.43, 2.64) * mm});
            skLineSegment(sketch, "E1418", {"start": v(-14.43, 2.64) * mm, "end": v(-14.07, 2.67) * mm});
            skLineSegment(sketch, "E1419", {"start": v(-14.07, 2.67) * mm, "end": v(-13.73, 2.65) * mm});
            skLineSegment(sketch, "E1420", {"start": v(-13.73, 2.65) * mm, "end": v(-13.41, 2.57) * mm});
            skLineSegment(sketch, "E1421", {"start": v(-13.41, 2.57) * mm, "end": v(-13.13, 2.42) * mm});
            skLineSegment(sketch, "E1422", {"start": v(-13.13, 2.42) * mm, "end": v(-12.97, 2.37) * mm});
            skLineSegment(sketch, "E1423", {"start": v(-12.97, 2.37) * mm, "end": v(-12.8, 2.36) * mm});
            skLineSegment(sketch, "E1424", {"start": v(-12.8, 2.36) * mm, "end": v(-12.7, 2.37) * mm});
            skLineSegment(sketch, "E1425", {"start": v(-12.7, 2.37) * mm, "end": v(-12.56, 2.48) * mm});
            skLineSegment(sketch, "E1426", {"start": v(-12.56, 2.48) * mm, "end": v(-12.2, 3.03) * mm});
            skLineSegment(sketch, "E1427", {"start": v(-12.2, 3.03) * mm, "end": v(-11.8, 3.53) * mm});
            skLineSegment(sketch, "E1428", {"start": v(-11.8, 3.53) * mm, "end": v(-11.74, 3.7) * mm});
            skLineSegment(sketch, "E1429", {"start": v(-11.74, 3.7) * mm, "end": v(-11.75, 3.8) * mm});
            skLineSegment(sketch, "E1430", {"start": v(-11.75, 3.8) * mm, "end": v(-11.82, 3.96) * mm});
            skLineSegment(sketch, "E1431", {"start": v(-11.82, 3.96) * mm, "end": v(-11.91, 4.1) * mm});
            skLineSegment(sketch, "E1432", {"start": v(-11.91, 4.1) * mm, "end": v(-12.14, 4.32) * mm});
            skLineSegment(sketch, "E1433", {"start": v(-12.14, 4.32) * mm, "end": v(-12.32, 4.6) * mm});
            skLineSegment(sketch, "E1434", {"start": v(-12.32, 4.6) * mm, "end": v(-12.44, 4.91) * mm});
            skLineSegment(sketch, "E1435", {"start": v(-12.44, 4.91) * mm, "end": v(-12.52, 5.26) * mm});
            skLineSegment(sketch, "E1436", {"start": v(-12.52, 5.26) * mm, "end": v(-12.57, 5.64) * mm});
            skLineSegment(sketch, "E1437", {"start": v(-12.57, 5.64) * mm, "end": v(-12.58, 6.04) * mm});
            skLineSegment(sketch, "E1438", {"start": v(-12.58, 6.04) * mm, "end": v(-11.98, 6.44) * mm});
            skLineSegment(sketch, "E1439", {"start": v(-11.98, 6.44) * mm, "end": v(-11.35, 6.8) * mm});
            skLineSegment(sketch, "E1440", {"start": v(-11.35, 6.8) * mm, "end": v(-11, 6.6) * mm});
            skLineSegment(sketch, "E1441", {"start": v(-11, 6.6) * mm, "end": v(-10.69, 6.39) * mm});
            skLineSegment(sketch, "E1442", {"start": v(-10.69, 6.39) * mm, "end": v(-10.41, 6.15) * mm});
            skLineSegment(sketch, "E1443", {"start": v(-10.41, 6.15) * mm, "end": v(-10.18, 5.9) * mm});
            skLineSegment(sketch, "E1444", {"start": v(-10.18, 5.9) * mm, "end": v(-10.02, 5.62) * mm});
            skLineSegment(sketch, "E1445", {"start": v(-10.02, 5.62) * mm, "end": v(-9.92, 5.31) * mm});
            skLineSegment(sketch, "E1446", {"start": v(-9.92, 5.31) * mm, "end": v(-9.84, 5.17) * mm});
            skLineSegment(sketch, "E1447", {"start": v(-9.84, 5.17) * mm, "end": v(-9.73, 5.04) * mm});
            skLineSegment(sketch, "E1448", {"start": v(-9.73, 5.04) * mm, "end": v(-9.65, 4.98) * mm});
            skLineSegment(sketch, "E1449", {"start": v(-9.65, 4.98) * mm, "end": v(-9.47, 4.95) * mm});
            skLineSegment(sketch, "E1450", {"start": v(-9.47, 4.95) * mm, "end": v(-8.84, 5.1) * mm});
            skLineSegment(sketch, "E1451", {"start": v(-8.84, 5.1) * mm, "end": v(-8.2, 5.16) * mm});
            skLineSegment(sketch, "E1452", {"start": v(-8.2, 5.16) * mm, "end": v(-8.03, 5.24) * mm});
            skLineSegment(sketch, "E1453", {"start": v(-8.03, 5.24) * mm, "end": v(-7.97, 5.32) * mm});
            skLineSegment(sketch, "E1454", {"start": v(-7.97, 5.32) * mm, "end": v(-7.9, 5.48) * mm});
            skLineSegment(sketch, "E1455", {"start": v(-7.9, 5.48) * mm, "end": v(-7.88, 5.64) * mm});
            skLineSegment(sketch, "E1456", {"start": v(-7.88, 5.64) * mm, "end": v(-7.88, 5.96) * mm});
            skLineSegment(sketch, "E1457", {"start": v(-7.88, 5.96) * mm, "end": v(-7.81, 6.28) * mm});
            skLineSegment(sketch, "E1458", {"start": v(-7.81, 6.28) * mm, "end": v(-7.67, 6.59) * mm});
            skLineSegment(sketch, "E1459", {"start": v(-7.67, 6.59) * mm, "end": v(-7.48, 6.9) * mm});
            skLineSegment(sketch, "E1460", {"start": v(-7.48, 6.9) * mm, "end": v(-7.25, 7.2) * mm});
            skLineSegment(sketch, "E1461", {"start": v(-7.25, 7.2) * mm, "end": v(-6.98, 7.48) * mm});
            skLineSegment(sketch, "E1462", {"start": v(-6.98, 7.48) * mm, "end": v(-6.26, 7.35) * mm});
            skLineSegment(sketch, "E1463", {"start": v(-6.26, 7.35) * mm, "end": v(-5.57, 7.15) * mm});
            skLineSegment(sketch, "E1464", {"start": v(-5.57, 7.15) * mm, "end": v(-5.46, 6.77) * mm});
            skLineSegment(sketch, "E1465", {"start": v(-5.46, 6.77) * mm, "end": v(-5.39, 6.4) * mm});
            skLineSegment(sketch, "E1466", {"start": v(-5.39, 6.4) * mm, "end": v(-5.36, 6.03) * mm});
            skLineSegment(sketch, "E1467", {"start": v(-5.36, 6.03) * mm, "end": v(-5.37, 5.7) * mm});
            skLineSegment(sketch, "E1468", {"start": v(-5.37, 5.7) * mm, "end": v(-5.46, 5.38) * mm});
            skLineSegment(sketch, "E1469", {"start": v(-5.46, 5.38) * mm, "end": v(-5.6, 5.1) * mm});
            skLineSegment(sketch, "E1470", {"start": v(-5.6, 5.1) * mm, "end": v(-5.65, 4.94) * mm});
            skLineSegment(sketch, "E1471", {"start": v(-5.65, 4.94) * mm, "end": v(-5.67, 4.77) * mm});
            skLineSegment(sketch, "E1472", {"start": v(-5.67, 4.77) * mm, "end": v(-5.65, 4.67) * mm});
            skLineSegment(sketch, "E1473", {"start": v(-5.65, 4.67) * mm, "end": v(-5.54, 4.52) * mm});
            skLineSegment(sketch, "E1474", {"start": v(-5.54, 4.52) * mm, "end": v(-5, 4.17) * mm});
            skLineSegment(sketch, "E1475", {"start": v(-5, 4.17) * mm, "end": v(-4.5, 3.76) * mm});
            skLineSegment(sketch, "E1476", {"start": v(-4.5, 3.76) * mm, "end": v(-4.32, 3.7) * mm});
            skLineSegment(sketch, "E1477", {"start": v(-4.32, 3.7) * mm, "end": v(-4.22, 3.72) * mm});
            skLineSegment(sketch, "E1478", {"start": v(-4.22, 3.72) * mm, "end": v(-4.06, 3.78) * mm});
            skLineSegment(sketch, "E1479", {"start": v(-4.06, 3.78) * mm, "end": v(-3.93, 3.87) * mm});
            skLineSegment(sketch, "E1480", {"start": v(-3.93, 3.87) * mm, "end": v(-3.7, 4.1) * mm});
            skLineSegment(sketch, "E1481", {"start": v(-3.7, 4.1) * mm, "end": v(-3.43, 4.28) * mm});
            skLineSegment(sketch, "E1482", {"start": v(-3.43, 4.28) * mm, "end": v(-3.11, 4.4) * mm});
            skLineSegment(sketch, "E1483", {"start": v(-3.11, 4.4) * mm, "end": v(-2.76, 4.49) * mm});
            skLineSegment(sketch, "E1484", {"start": v(-2.76, 4.49) * mm, "end": v(-2.38, 4.53) * mm});
            skLineSegment(sketch, "E1485", {"start": v(-2.38, 4.53) * mm, "end": v(-1.99, 4.55) * mm});
            skLineSegment(sketch, "E1486", {"start": v(-1.99, 4.55) * mm, "end": v(-1.58, 3.95) * mm});
            skLineSegment(sketch, "E1487", {"start": v(-1.58, 3.95) * mm, "end": v(-1.23, 3.31) * mm});
            skLineSegment(sketch, "E1488", {"start": v(-1.23, 3.31) * mm, "end": v(-1.42, 2.96) * mm});
            skLineSegment(sketch, "E1489", {"start": v(-1.42, 2.96) * mm, "end": v(-1.63, 2.65) * mm});
            skLineSegment(sketch, "E1490", {"start": v(-1.63, 2.65) * mm, "end": v(-1.87, 2.37) * mm});
            skLineSegment(sketch, "E1491", {"start": v(-1.87, 2.37) * mm, "end": v(-2.12, 2.14) * mm});
            skLineSegment(sketch, "E1492", {"start": v(-2.12, 2.14) * mm, "end": v(-2.4, 1.98) * mm});
            skLineSegment(sketch, "E1493", {"start": v(-2.4, 1.98) * mm, "end": v(-2.7, 1.88) * mm});
            skLineSegment(sketch, "E1494", {"start": v(-2.7, 1.88) * mm, "end": v(-2.85, 1.8) * mm});
            skLineSegment(sketch, "E1495", {"start": v(-2.85, 1.8) * mm, "end": v(-2.98, 1.7) * mm});
            skLineSegment(sketch, "E1496", {"start": v(-2.98, 1.7) * mm, "end": v(-3.04, 1.62) * mm});
            skLineSegment(sketch, "E1497", {"start": v(-3.04, 1.62) * mm, "end": v(-3.07, 1.43) * mm});
            skLineSegment(sketch, "E1498", {"start": v(-3.07, 1.43) * mm, "end": v(-2.93, 0.8) * mm});
            skLineSegment(sketch, "E1499", {"start": v(-2.93, 0.8) * mm, "end": v(-2.87, 0.16) * mm});
            skLineSegment(sketch, "E1500", {"start": v(-2.87, 0.16) * mm, "end": v(-2.78, 0) * mm});
            skLineSegment(sketch, "E1501", {"start": v(-2.78, 0) * mm, "end": v(-2.7, -0.07) * mm});
            skLineSegment(sketch, "E1502", {"start": v(-2.7, -0.07) * mm, "end": v(-2.54, -0.13) * mm});
            skLineSegment(sketch, "E1503", {"start": v(-2.54, -0.13) * mm, "end": v(-2.39, -0.16) * mm});
            skLineSegment(sketch, "E1504", {"start": v(-2.39, -0.16) * mm, "end": v(-2.07, -0.16) * mm});
            skLineSegment(sketch, "E1505", {"start": v(-2.07, -0.16) * mm, "end": v(-1.75, -0.23) * mm});
            skLineSegment(sketch, "E1506", {"start": v(-1.75, -0.23) * mm, "end": v(-1.43, -0.37) * mm});
            skLineSegment(sketch, "E1507", {"start": v(-1.43, -0.37) * mm, "end": v(-1.13, -0.56) * mm});
            skLineSegment(sketch, "E1508", {"start": v(-1.13, -0.56) * mm, "end": v(-0.83, -0.8) * mm});
            skLineSegment(sketch, "E1509", {"start": v(-0.83, -0.8) * mm, "end": v(-0.54, -1.06) * mm});
            skLineSegment(sketch, "E1510", {"start": v(-0.54, -1.06) * mm, "end": v(-0.67, -1.77) * mm});
            skLineSegment(sketch, "E1511", {"start": v(-0.67, -1.77) * mm, "end": v(-0.88, -2.47) * mm});
            skLineSegment(sketch, "E1512", {"start": v(-0.88, -2.47) * mm, "end": v(-1.26, -2.58) * mm});
            skLineSegment(sketch, "E1513", {"start": v(-1.26, -2.58) * mm, "end": v(-1.63, -2.65) * mm});
            skLineSegment(sketch, "E1514", {"start": v(-1.63, -2.65) * mm, "end": v(-1.99, -2.68) * mm});
            skLineSegment(sketch, "E1515", {"start": v(-1.99, -2.68) * mm, "end": v(-2.33, -2.66) * mm});
            skLineSegment(sketch, "E1516", {"start": v(-2.33, -2.66) * mm, "end": v(-2.65, -2.58) * mm});
            skLineSegment(sketch, "E1517", {"start": v(-2.65, -2.58) * mm, "end": v(-2.93, -2.43) * mm});
            skLineSegment(sketch, "E1518", {"start": v(-2.93, -2.43) * mm, "end": v(-3.09, -2.39) * mm});
            skLineSegment(sketch, "E1519", {"start": v(-3.09, -2.39) * mm, "end": v(-3.26, -2.37) * mm});
            skLineSegment(sketch, "E1520", {"start": v(-3.26, -2.37) * mm, "end": v(-3.35, -2.39) * mm});
            skLineSegment(sketch, "E1521", {"start": v(-3.35, -2.39) * mm, "end": v(-3.5, -2.5) * mm});
            skLineSegment(sketch, "E1522", {"start": v(-3.5, -2.5) * mm, "end": v(-3.85, -3.04) * mm});
            skLineSegment(sketch, "E1523", {"start": v(-3.85, -3.04) * mm, "end": v(-4.26, -3.54) * mm});
            skLineSegment(sketch, "E1524", {"start": v(-4.26, -3.54) * mm, "end": v(-4.32, -3.72) * mm});
            skLineSegment(sketch, "E1525", {"start": v(-4.32, -3.72) * mm, "end": v(-4.3, -3.82) * mm});
            skLineSegment(sketch, "E1526", {"start": v(-4.3, -3.82) * mm, "end": v(-4.24, -3.97) * mm});
            skLineSegment(sketch, "E1527", {"start": v(-4.24, -3.97) * mm, "end": v(-4.15, -4.1) * mm});
            skLineSegment(sketch, "E1528", {"start": v(-4.15, -4.1) * mm, "end": v(-3.92, -4.33) * mm});
            skLineSegment(sketch, "E1529", {"start": v(-3.92, -4.33) * mm, "end": v(-3.74, -4.6) * mm});
            skLineSegment(sketch, "E1530", {"start": v(-3.74, -4.6) * mm, "end": v(-3.62, -4.93) * mm});
            skLineSegment(sketch, "E1531", {"start": v(-3.62, -4.93) * mm, "end": v(-3.54, -5.28) * mm});
            skLineSegment(sketch, "E1532", {"start": v(-3.54, -5.28) * mm, "end": v(-3.49, -5.65) * mm});
            skLineSegment(sketch, "E1533", {"start": v(-3.49, -5.65) * mm, "end": v(-3.48, -6.05) * mm});
            skLineSegment(sketch, "E1534", {"start": v(-3.48, -6.05) * mm, "end": v(-4.08, -6.46) * mm});
            skLineSegment(sketch, "E1535", {"start": v(-4.08, -6.46) * mm, "end": v(-4.71, -6.8) * mm});
            skLineSegment(sketch, "E1536", {"start": v(-4.71, -6.8) * mm, "end": v(-5.06, -6.62) * mm});
            skLineSegment(sketch, "E1537", {"start": v(-5.06, -6.62) * mm, "end": v(-5.37, -6.4) * mm});
            skLineSegment(sketch, "E1538", {"start": v(-5.37, -6.4) * mm, "end": v(-5.65, -6.17) * mm});
            skLineSegment(sketch, "E1539", {"start": v(-5.65, -6.17) * mm, "end": v(-5.88, -5.91) * mm});
            skLineSegment(sketch, "E1540", {"start": v(-5.88, -5.91) * mm, "end": v(-6.04, -5.63) * mm});
            skLineSegment(sketch, "E1541", {"start": v(-6.04, -5.63) * mm, "end": v(-6.14, -5.33) * mm});
            skLineSegment(sketch, "E1542", {"start": v(-6.14, -5.33) * mm, "end": v(-6.22, -5.19) * mm});
            skLineSegment(sketch, "E1543", {"start": v(-6.22, -5.19) * mm, "end": v(-6.33, -5.05) * mm});
            skLineSegment(sketch, "E1544", {"start": v(-6.33, -5.05) * mm, "end": v(-6.4, -5) * mm});
            skLineSegment(sketch, "E1545", {"start": v(-6.4, -5) * mm, "end": v(-6.59, -4.97) * mm});
            skLineSegment(sketch, "E1546", {"start": v(-6.59, -4.97) * mm, "end": v(-7.22, -5.11) * mm});
            skLineSegment(sketch, "E1547", {"start": v(-7.22, -5.11) * mm, "end": v(-7.87, -5.17) * mm});
            skLineSegment(sketch, "E1548", {"start": v(-7.87, -5.17) * mm, "end": v(-8.03, -5.25) * mm});
            skLineSegment(sketch, "E1549", {"start": v(-8.03, -5.25) * mm, "end": v(-8.1, -5.33) * mm});
            skLineSegment(sketch, "E1550", {"start": v(-8.1, -5.33) * mm, "end": v(-8.16, -5.5) * mm});
            skLineSegment(sketch, "E1551", {"start": v(-8.16, -5.5) * mm, "end": v(-8.18, -5.65) * mm});
            skLineSegment(sketch, "E1552", {"start": v(-8.18, -5.65) * mm, "end": v(-8.18, -5.97) * mm});
            skLineSegment(sketch, "E1553", {"start": v(-8.18, -5.97) * mm, "end": v(-8.25, -6.29) * mm});
            skLineSegment(sketch, "E1554", {"start": v(-8.25, -6.29) * mm, "end": v(-8.4, -6.6) * mm});
            skLineSegment(sketch, "E1555", {"start": v(-8.4, -6.6) * mm, "end": v(-8.58, -6.91) * mm});
            skLineSegment(sketch, "E1556", {"start": v(-8.58, -6.91) * mm, "end": v(-8.81, -7.21) * mm});
            skLineSegment(sketch, "E1557", {"start": v(-8.81, -7.21) * mm, "end": v(-9.08, -7.5) * mm});
            skLineSegment(sketch, "E1558", {"start": v(-9.08, -7.5) * mm, "end": v(-9.8, -7.36) * mm});
            skLineSegment(sketch, "E1559", {"start": v(-9.8, -7.36) * mm, "end": v(-10.5, -7.16) * mm});
            skLineSegment(sketch, "E1560", {"start": v(-10.5, -7.16) * mm, "end": v(-10.6, -6.78) * mm});
            skLineSegment(sketch, "E1561", {"start": v(-10.6, -6.78) * mm, "end": v(-10.67, -6.4) * mm});
            skLineSegment(sketch, "E1562", {"start": v(-10.67, -6.4) * mm, "end": v(-10.7, -6.05) * mm});
            skLineSegment(sketch, "E1563", {"start": v(-10.7, -6.05) * mm, "end": v(-10.69, -5.7) * mm});
            skLineSegment(sketch, "E1564", {"start": v(-10.69, -5.7) * mm, "end": v(-10.6, -5.4) * mm});
            skLineSegment(sketch, "E1565", {"start": v(-10.6, -5.4) * mm, "end": v(-10.45, -5.1) * mm});
            skLineSegment(sketch, "E1566", {"start": v(-10.45, -5.1) * mm, "end": v(-10.4, -4.95) * mm});
            skLineSegment(sketch, "E1567", {"start": v(-10.4, -4.95) * mm, "end": v(-10.4, -4.78) * mm});
            skLineSegment(sketch, "E1568", {"start": v(-10.4, -4.78) * mm, "end": v(-10.4, -4.68) * mm});
            skLineSegment(sketch, "E1569", {"start": v(-10.4, -4.68) * mm, "end": v(-10.52, -4.53) * mm});
            skLineSegment(sketch, "E1570", {"start": v(-10.52, -4.53) * mm, "end": v(-11.07, -4.19) * mm});
            skLineSegment(sketch, "E1571", {"start": v(-11.07, -4.19) * mm, "end": v(-11.57, -3.77) * mm});
            skLineSegment(sketch, "E1572", {"start": v(-11.57, -3.77) * mm, "end": v(-11.74, -3.72) * mm});
            skLineSegment(sketch, "E1573", {"start": v(-11.74, -3.72) * mm, "end": v(-11.84, -3.73) * mm});
            skLineSegment(sketch, "E1574", {"start": v(-11.84, -3.73) * mm, "end": v(-12, -3.8) * mm});
            skLineSegment(sketch, "E1575", {"start": v(-12, -3.8) * mm, "end": v(-12.13, -3.89) * mm});
            skLineSegment(sketch, "E1576", {"start": v(-12.13, -3.89) * mm, "end": v(-12.35, -4.12) * mm});
            skLineSegment(sketch, "E1577", {"start": v(-12.35, -4.12) * mm, "end": v(-12.63, -4.3) * mm});
            skLineSegment(sketch, "E1578", {"start": v(-12.63, -4.3) * mm, "end": v(-12.95, -4.42) * mm});
            skLineSegment(sketch, "E1579", {"start": v(-12.95, -4.42) * mm, "end": v(-13.3, -4.5) * mm});
            skLineSegment(sketch, "E1580", {"start": v(-13.3, -4.5) * mm, "end": v(-13.68, -4.55) * mm});
            skLineSegment(sketch, "E1581", {"start": v(-13.68, -4.55) * mm, "end": v(-14.07, -4.56) * mm});
            skLineSegment(sketch, "E1582", {"start": v(-14.07, -4.56) * mm, "end": v(-14.48, -3.96) * mm});
            skLineSegment(sketch, "E1583", {"start": v(-14.48, -3.96) * mm, "end": v(-14.83, -3.32) * mm});
            skLineSegment(sketch, "E1584", {"start": v(-14.83, -3.32) * mm, "end": v(-14.64, -2.98) * mm});
            skLineSegment(sketch, "E1585", {"start": v(-14.64, -2.98) * mm, "end": v(-14.43, -2.66) * mm});
            skLineSegment(sketch, "E1586", {"start": v(-14.43, -2.66) * mm, "end": v(-14.2, -2.39) * mm});
            skLineSegment(sketch, "E1587", {"start": v(-14.2, -2.39) * mm, "end": v(-13.94, -2.16) * mm});
            skLineSegment(sketch, "E1588", {"start": v(-13.94, -2.16) * mm, "end": v(-13.66, -2) * mm});
            skLineSegment(sketch, "E1589", {"start": v(-13.66, -2) * mm, "end": v(-13.35, -1.9) * mm});
            skLineSegment(sketch, "E1590", {"start": v(-13.35, -1.9) * mm, "end": v(-13.2, -1.82) * mm});
            skLineSegment(sketch, "E1591", {"start": v(-13.2, -1.82) * mm, "end": v(-13.08, -1.71) * mm});
            skLineSegment(sketch, "E1592", {"start": v(-13.08, -1.71) * mm, "end": v(-13.02, -1.63) * mm});
            skLineSegment(sketch, "E1593", {"start": v(-13.02, -1.63) * mm, "end": v(-13, -1.45) * mm});
            skLineSegment(sketch, "E1594", {"start": v(-13, -1.45) * mm, "end": v(-13.13, -0.82) * mm});
            skLineSegment(sketch, "E1595", {"start": v(-13.13, -0.82) * mm, "end": v(-13.2, -0.17) * mm});
            skLineSegment(sketch, "E1596", {"start": v(-7.28, 0) * mm, "end": v(-7.3, 0.19) * mm});
            skLineSegment(sketch, "E1597", {"start": v(-7.3, 0.19) * mm, "end": v(-7.38, 0.37) * mm});
            skLineSegment(sketch, "E1598", {"start": v(-7.38, 0.37) * mm, "end": v(-7.5, 0.52) * mm});
            skLineSegment(sketch, "E1599", {"start": v(-7.5, 0.52) * mm, "end": v(-7.65, 0.64) * mm});
            skLineSegment(sketch, "E1600", {"start": v(-7.65, 0.64) * mm, "end": v(-7.84, 0.72) * mm});
            skLineSegment(sketch, "E1601", {"start": v(-7.84, 0.72) * mm, "end": v(-8.03, 0.74) * mm});
            skLineSegment(sketch, "E1602", {"start": v(-8.03, 0.74) * mm, "end": v(-8.22, 0.72) * mm});
            skLineSegment(sketch, "E1603", {"start": v(-8.22, 0.72) * mm, "end": v(-8.4, 0.64) * mm});
            skLineSegment(sketch, "E1604", {"start": v(-8.4, 0.64) * mm, "end": v(-8.56, 0.52) * mm});
            skLineSegment(sketch, "E1605", {"start": v(-8.56, 0.52) * mm, "end": v(-8.68, 0.37) * mm});
            skLineSegment(sketch, "E1606", {"start": v(-8.68, 0.37) * mm, "end": v(-8.75, 0.19) * mm});
            skLineSegment(sketch, "E1607", {"start": v(-8.75, 0.19) * mm, "end": v(-8.78, 0) * mm});
            skLineSegment(sketch, "E1608", {"start": v(-8.78, 0) * mm, "end": v(-8.75, -0.2) * mm});
            skLineSegment(sketch, "E1609", {"start": v(-8.75, -0.2) * mm, "end": v(-8.68, -0.38) * mm});
            skLineSegment(sketch, "E1610", {"start": v(-8.68, -0.38) * mm, "end": v(-8.56, -0.54) * mm});
            skLineSegment(sketch, "E1611", {"start": v(-8.56, -0.54) * mm, "end": v(-8.4, -0.66) * mm});
            skLineSegment(sketch, "E1612", {"start": v(-8.4, -0.66) * mm, "end": v(-8.22, -0.73) * mm});
            skLineSegment(sketch, "E1613", {"start": v(-8.22, -0.73) * mm, "end": v(-8.03, -0.76) * mm});
            skLineSegment(sketch, "E1614", {"start": v(-8.03, -0.76) * mm, "end": v(-7.84, -0.73) * mm});
            skLineSegment(sketch, "E1615", {"start": v(-7.84, -0.73) * mm, "end": v(-7.65, -0.66) * mm});
            skLineSegment(sketch, "E1616", {"start": v(-7.65, -0.66) * mm, "end": v(-7.5, -0.54) * mm});
            skLineSegment(sketch, "E1617", {"start": v(-7.5, -0.54) * mm, "end": v(-7.38, -0.38) * mm});
            skLineSegment(sketch, "E1618", {"start": v(-7.38, -0.38) * mm, "end": v(-7.3, -0.2) * mm});
            skLineSegment(sketch, "E1619", {"start": v(-7.3, -0.2) * mm, "end": v(-7.28, 0) * mm});
            skLineSegment(sketch, "E1620", {"start": v(-8.03, 0.74) * mm, "end": v(-8.03, -0.76) * mm, "construction": true});
            skLineSegment(sketch, "E1621", {"start": v(-8.78, 0) * mm, "end": v(-7.28, 0) * mm, "construction": true});
            skLineSegment(sketch, "E1622", {"start": v(-8.03, 1) * mm, "end": v(-8.03, -1) * mm, "construction": true});
            skLineSegment(sketch, "E1623", {"start": v(-9.03, 0) * mm, "end": v(-7.03, 0) * mm, "construction": true});
            skSolve(sketch);
        }
        {
            var Q0;
            Q0=makeQuery(id+"F0.imprint","IMPRINT",FACE,{"disambiguationData":[TD([[makeQuery(id+"F0.imprint","IMPRINT",EDGE,{"derivedFrom":sQuery(id+"F0.wireOp",EDGE,"E1380")}),-1.0]])]});
            extrude(context, id + "F1", {"entities" : qUnion([Q0]), "depth" : 10 * mm, "offsetDistance" : 25 * mm});
        }
        {
            var Q0;
            Q0=makeQuery(id+"F0.imprint","IMPRINT",FACE,{"disambiguationData":[TD([[makeQuery(id+"F0.imprint","IMPRINT",EDGE,{"derivedFrom":sQuery(id+"F0.wireOp",EDGE,"E0")}),-1.0]])]});
            extrude(context, id + "F2", {"entities" : qUnion([Q0]), "operationType" : NewBodyOperationType.ADD, "depth" : 4 * mm, "offsetDistance" : 25 * mm});
        }
    });
